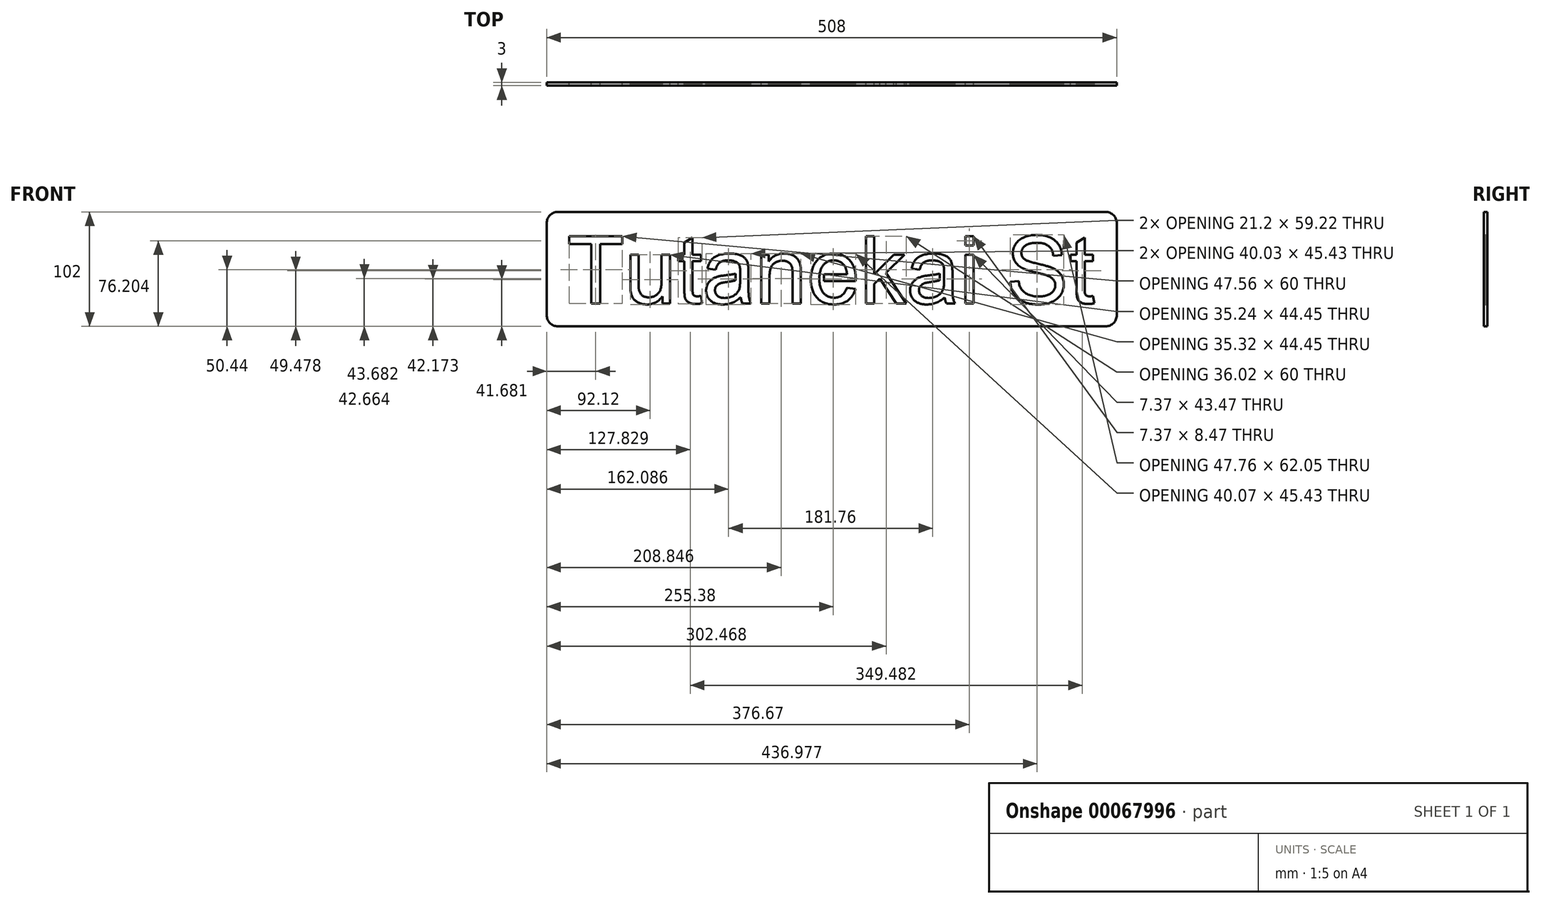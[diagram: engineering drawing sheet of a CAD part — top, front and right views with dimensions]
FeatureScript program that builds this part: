
annotation { "Feature Type Name" : "Feature", "Feature Type Description" : "" }
export const myFeature = defineFeature(function(context is Context, id is Id, definition is map)
    precondition{}
    {
        {
            var Q0;
            Q0=qCreatedBy(makeId("Front.planeOp"),FACE);
            var sketch = newSketch(context, id + "F0", { "sketchPlane" : qUnion([Q0])});
            skLineSegment(sketch, "E0", {"start": v(-254, -41) * mm, "end": v(-254, 41) * mm});
            skArc(sketch, "E1", {"start": v(-244, -51) * mm, "mid": v(-251.07, -48.07) * mm, "end": v(-254, -41) * mm});
            skLineSegment(sketch, "E2", {"start": v(244, -51) * mm, "end": v(-244, -51) * mm});
            skArc(sketch, "E3", {"start": v(254, -41) * mm, "mid": v(251.07, -48.07) * mm, "end": v(244, -51) * mm});
            skLineSegment(sketch, "E4", {"start": v(254, 41) * mm, "end": v(254, -41) * mm});
            skArc(sketch, "E5", {"start": v(244, 51) * mm, "mid": v(251.07, 48.07) * mm, "end": v(254, 41) * mm});
            skLineSegment(sketch, "E6", {"start": v(-244, 51) * mm, "end": v(244, 51) * mm});
            skArc(sketch, "E7", {"start": v(-254, 41) * mm, "mid": v(-251.07, 48.07) * mm, "end": v(-244, 51) * mm});
            skLineSegment(sketch, "E8", {"start": v(89.64, 7.79) * mm, "end": v(89, 7.78) * mm});
            skLineSegment(sketch, "E9", {"start": v(89, 7.78) * mm, "end": v(88.38, 7.76) * mm});
            skLineSegment(sketch, "E10", {"start": v(88.38, 7.76) * mm, "end": v(87.79, 7.73) * mm});
            skLineSegment(sketch, "E11", {"start": v(87.79, 7.73) * mm, "end": v(87.21, 7.68) * mm});
            skLineSegment(sketch, "E12", {"start": v(87.21, 7.68) * mm, "end": v(86.66, 7.61) * mm});
            skLineSegment(sketch, "E13", {"start": v(86.66, 7.61) * mm, "end": v(86.13, 7.53) * mm});
            skLineSegment(sketch, "E14", {"start": v(86.13, 7.53) * mm, "end": v(85.61, 7.44) * mm});
            skLineSegment(sketch, "E15", {"start": v(85.61, 7.44) * mm, "end": v(85.12, 7.33) * mm});
            skLineSegment(sketch, "E16", {"start": v(85.12, 7.33) * mm, "end": v(84.65, 7.21) * mm});
            skLineSegment(sketch, "E17", {"start": v(84.65, 7.21) * mm, "end": v(84.2, 7.08) * mm});
            skLineSegment(sketch, "E18", {"start": v(84.2, 7.08) * mm, "end": v(83.78, 6.93) * mm});
            skLineSegment(sketch, "E19", {"start": v(83.78, 6.93) * mm, "end": v(83.38, 6.76) * mm});
            skLineSegment(sketch, "E20", {"start": v(83.38, 6.76) * mm, "end": v(83, 6.59) * mm});
            skLineSegment(sketch, "E21", {"start": v(83, 6.59) * mm, "end": v(82.63, 6.4) * mm});
            skLineSegment(sketch, "E22", {"start": v(82.63, 6.4) * mm, "end": v(82.29, 6.19) * mm});
            skLineSegment(sketch, "E23", {"start": v(82.29, 6.19) * mm, "end": v(81.97, 5.97) * mm});
            skLineSegment(sketch, "E24", {"start": v(81.97, 5.97) * mm, "end": v(81.66, 5.73) * mm});
            skLineSegment(sketch, "E25", {"start": v(81.66, 5.73) * mm, "end": v(81.37, 5.47) * mm});
            skLineSegment(sketch, "E26", {"start": v(81.37, 5.47) * mm, "end": v(81.08, 5.19) * mm});
            skLineSegment(sketch, "E27", {"start": v(81.08, 5.19) * mm, "end": v(80.8, 4.88) * mm});
            skLineSegment(sketch, "E28", {"start": v(80.8, 4.88) * mm, "end": v(80.55, 4.56) * mm});
            skLineSegment(sketch, "E29", {"start": v(80.55, 4.56) * mm, "end": v(80.3, 4.2) * mm});
            skLineSegment(sketch, "E30", {"start": v(80.3, 4.2) * mm, "end": v(80.05, 3.84) * mm});
            skLineSegment(sketch, "E31", {"start": v(80.05, 3.84) * mm, "end": v(79.81, 3.45) * mm});
            skLineSegment(sketch, "E32", {"start": v(79.81, 3.45) * mm, "end": v(79.59, 3.03) * mm});
            skLineSegment(sketch, "E33", {"start": v(79.59, 3.03) * mm, "end": v(79.38, 2.6) * mm});
            skLineSegment(sketch, "E34", {"start": v(79.38, 2.6) * mm, "end": v(79.17, 2.14) * mm});
            skLineSegment(sketch, "E35", {"start": v(79.17, 2.14) * mm, "end": v(78.98, 1.66) * mm});
            skLineSegment(sketch, "E36", {"start": v(78.98, 1.66) * mm, "end": v(78.8, 1.16) * mm});
            skLineSegment(sketch, "E37", {"start": v(78.8, 1.16) * mm, "end": v(78.62, 0.63) * mm});
            skLineSegment(sketch, "E38", {"start": v(78.62, 0.63) * mm, "end": v(78.46, 0.09) * mm});
            skLineSegment(sketch, "E39", {"start": v(78.46, 0.09) * mm, "end": v(78.3, -0.48) * mm});
            skLineSegment(sketch, "E40", {"start": v(78.3, -0.48) * mm, "end": v(71.1, 0.5) * mm});
            skLineSegment(sketch, "E41", {"start": v(71.1, 0.5) * mm, "end": v(71.37, 1.63) * mm});
            skLineSegment(sketch, "E42", {"start": v(71.37, 1.63) * mm, "end": v(71.67, 2.7) * mm});
            skLineSegment(sketch, "E43", {"start": v(71.67, 2.7) * mm, "end": v(72.02, 3.72) * mm});
            skLineSegment(sketch, "E44", {"start": v(72.02, 3.72) * mm, "end": v(72.4, 4.68) * mm});
            skLineSegment(sketch, "E45", {"start": v(72.4, 4.68) * mm, "end": v(72.82, 5.59) * mm});
            skLineSegment(sketch, "E46", {"start": v(72.82, 5.59) * mm, "end": v(73.29, 6.44) * mm});
            skLineSegment(sketch, "E47", {"start": v(73.29, 6.44) * mm, "end": v(73.8, 7.23) * mm});
            skLineSegment(sketch, "E48", {"start": v(73.8, 7.23) * mm, "end": v(74.33, 7.97) * mm});
            skLineSegment(sketch, "E49", {"start": v(74.33, 7.97) * mm, "end": v(74.93, 8.66) * mm});
            skLineSegment(sketch, "E50", {"start": v(74.93, 8.66) * mm, "end": v(75.58, 9.31) * mm});
            skLineSegment(sketch, "E51", {"start": v(75.58, 9.31) * mm, "end": v(76.3, 9.92) * mm});
            skLineSegment(sketch, "E52", {"start": v(76.3, 9.92) * mm, "end": v(77.09, 10.5) * mm});
            skLineSegment(sketch, "E53", {"start": v(77.09, 10.5) * mm, "end": v(77.93, 11.02) * mm});
            skLineSegment(sketch, "E54", {"start": v(77.93, 11.02) * mm, "end": v(78.84, 11.5) * mm});
            skLineSegment(sketch, "E55", {"start": v(78.84, 11.5) * mm, "end": v(79.8, 11.95) * mm});
            skLineSegment(sketch, "E56", {"start": v(79.8, 11.95) * mm, "end": v(80.84, 12.35) * mm});
            skLineSegment(sketch, "E57", {"start": v(80.84, 12.35) * mm, "end": v(81.93, 12.71) * mm});
            skLineSegment(sketch, "E58", {"start": v(81.93, 12.71) * mm, "end": v(83.05, 13.02) * mm});
            skLineSegment(sketch, "E59", {"start": v(83.05, 13.02) * mm, "end": v(84.22, 13.29) * mm});
            skLineSegment(sketch, "E60", {"start": v(84.22, 13.29) * mm, "end": v(85.44, 13.5) * mm});
            skLineSegment(sketch, "E61", {"start": v(85.44, 13.5) * mm, "end": v(86.69, 13.67) * mm});
            skLineSegment(sketch, "E62", {"start": v(86.69, 13.67) * mm, "end": v(87.99, 13.8) * mm});
            skLineSegment(sketch, "E63", {"start": v(87.99, 13.8) * mm, "end": v(89.32, 13.86) * mm});
            skLineSegment(sketch, "E64", {"start": v(89.32, 13.86) * mm, "end": v(90.7, 13.89) * mm});
            skLineSegment(sketch, "E65", {"start": v(90.7, 13.89) * mm, "end": v(92.06, 13.87) * mm});
            skLineSegment(sketch, "E66", {"start": v(92.06, 13.87) * mm, "end": v(93.36, 13.8) * mm});
            skLineSegment(sketch, "E67", {"start": v(93.36, 13.8) * mm, "end": v(94.59, 13.7) * mm});
            skLineSegment(sketch, "E68", {"start": v(94.59, 13.7) * mm, "end": v(95.75, 13.56) * mm});
            skLineSegment(sketch, "E69", {"start": v(95.75, 13.56) * mm, "end": v(96.85, 13.38) * mm});
            skLineSegment(sketch, "E70", {"start": v(96.85, 13.38) * mm, "end": v(97.88, 13.15) * mm});
            skLineSegment(sketch, "E71", {"start": v(97.88, 13.15) * mm, "end": v(98.85, 12.88) * mm});
            skLineSegment(sketch, "E72", {"start": v(98.85, 12.88) * mm, "end": v(99.75, 12.58) * mm});
            skLineSegment(sketch, "E73", {"start": v(99.75, 12.58) * mm, "end": v(100.6, 12.24) * mm});
            skLineSegment(sketch, "E74", {"start": v(100.6, 12.24) * mm, "end": v(101.37, 11.88) * mm});
            skLineSegment(sketch, "E75", {"start": v(101.37, 11.88) * mm, "end": v(102.1, 11.5) * mm});
            skLineSegment(sketch, "E76", {"start": v(102.1, 11.5) * mm, "end": v(102.77, 11.1) * mm});
            skLineSegment(sketch, "E77", {"start": v(102.77, 11.1) * mm, "end": v(103.38, 10.68) * mm});
            skLineSegment(sketch, "E78", {"start": v(103.38, 10.68) * mm, "end": v(103.93, 10.23) * mm});
            skLineSegment(sketch, "E79", {"start": v(103.93, 10.23) * mm, "end": v(104.43, 9.77) * mm});
            skLineSegment(sketch, "E80", {"start": v(104.43, 9.77) * mm, "end": v(104.87, 9.28) * mm});
            skLineSegment(sketch, "E81", {"start": v(104.87, 9.28) * mm, "end": v(105.26, 8.77) * mm});
            skLineSegment(sketch, "E82", {"start": v(105.26, 8.77) * mm, "end": v(105.62, 8.23) * mm});
            skLineSegment(sketch, "E83", {"start": v(105.62, 8.23) * mm, "end": v(105.96, 7.65) * mm});
            skLineSegment(sketch, "E84", {"start": v(105.96, 7.65) * mm, "end": v(106.26, 7.04) * mm});
            skLineSegment(sketch, "E85", {"start": v(106.26, 7.04) * mm, "end": v(106.53, 6.4) * mm});
            skLineSegment(sketch, "E86", {"start": v(106.53, 6.4) * mm, "end": v(106.77, 5.72) * mm});
            skLineSegment(sketch, "E87", {"start": v(106.77, 5.72) * mm, "end": v(106.98, 5.01) * mm});
            skLineSegment(sketch, "E88", {"start": v(106.98, 5.01) * mm, "end": v(107.16, 4.27) * mm});
            skLineSegment(sketch, "E89", {"start": v(107.16, 4.27) * mm, "end": v(107.24, 3.75) * mm});
            skLineSegment(sketch, "E90", {"start": v(107.24, 3.75) * mm, "end": v(107.32, 3.14) * mm});
            skLineSegment(sketch, "E91", {"start": v(107.32, 3.14) * mm, "end": v(107.38, 2.43) * mm});
            skLineSegment(sketch, "E92", {"start": v(107.38, 2.43) * mm, "end": v(107.43, 1.63) * mm});
            skLineSegment(sketch, "E93", {"start": v(107.43, 1.63) * mm, "end": v(107.47, 0.73) * mm});
            skLineSegment(sketch, "E94", {"start": v(107.47, 0.73) * mm, "end": v(107.5, -0.26) * mm});
            skLineSegment(sketch, "E95", {"start": v(107.5, -0.26) * mm, "end": v(107.52, -1.34) * mm});
            skLineSegment(sketch, "E96", {"start": v(107.52, -1.34) * mm, "end": v(107.53, -2.52) * mm});
            skLineSegment(sketch, "E97", {"start": v(107.53, -2.52) * mm, "end": v(107.53, -12.35) * mm});
            skLineSegment(sketch, "E98", {"start": v(107.53, -12.35) * mm, "end": v(107.53, -13.6) * mm});
            skLineSegment(sketch, "E99", {"start": v(107.53, -13.6) * mm, "end": v(107.53, -14.8) * mm});
            skLineSegment(sketch, "E100", {"start": v(107.53, -14.8) * mm, "end": v(107.54, -15.93) * mm});
            skLineSegment(sketch, "E101", {"start": v(107.54, -15.93) * mm, "end": v(107.56, -17.01) * mm});
            skLineSegment(sketch, "E102", {"start": v(107.56, -17.01) * mm, "end": v(107.57, -18.03) * mm});
            skLineSegment(sketch, "E103", {"start": v(107.57, -18.03) * mm, "end": v(107.6, -18.99) * mm});
            skLineSegment(sketch, "E104", {"start": v(107.6, -18.99) * mm, "end": v(107.62, -19.9) * mm});
            skLineSegment(sketch, "E105", {"start": v(107.62, -19.9) * mm, "end": v(107.64, -20.73) * mm});
            skLineSegment(sketch, "E106", {"start": v(107.64, -20.73) * mm, "end": v(107.68, -21.51) * mm});
            skLineSegment(sketch, "E107", {"start": v(107.68, -21.51) * mm, "end": v(107.71, -22.24) * mm});
            skLineSegment(sketch, "E108", {"start": v(107.71, -22.24) * mm, "end": v(107.75, -22.9) * mm});
            skLineSegment(sketch, "E109", {"start": v(107.75, -22.9) * mm, "end": v(107.8, -23.5) * mm});
            skLineSegment(sketch, "E110", {"start": v(107.8, -23.5) * mm, "end": v(107.84, -24.06) * mm});
            skLineSegment(sketch, "E111", {"start": v(107.84, -24.06) * mm, "end": v(107.89, -24.54) * mm});
            skLineSegment(sketch, "E112", {"start": v(107.89, -24.54) * mm, "end": v(107.94, -24.97) * mm});
            skLineSegment(sketch, "E113", {"start": v(107.94, -24.97) * mm, "end": v(108, -25.34) * mm});
            skLineSegment(sketch, "E114", {"start": v(108, -25.34) * mm, "end": v(108.13, -26.02) * mm});
            skLineSegment(sketch, "E115", {"start": v(108.13, -26.02) * mm, "end": v(108.29, -26.69) * mm});
            skLineSegment(sketch, "E116", {"start": v(108.29, -26.69) * mm, "end": v(108.48, -27.35) * mm});
            skLineSegment(sketch, "E117", {"start": v(108.48, -27.35) * mm, "end": v(108.7, -28) * mm});
            skLineSegment(sketch, "E118", {"start": v(108.7, -28) * mm, "end": v(108.95, -28.66) * mm});
            skLineSegment(sketch, "E119", {"start": v(108.95, -28.66) * mm, "end": v(109.22, -29.3) * mm});
            skLineSegment(sketch, "E120", {"start": v(109.22, -29.3) * mm, "end": v(109.53, -29.93) * mm});
            skLineSegment(sketch, "E121", {"start": v(109.53, -29.93) * mm, "end": v(109.86, -30.56) * mm});
            skLineSegment(sketch, "E122", {"start": v(109.86, -30.56) * mm, "end": v(102.16, -30.56) * mm});
            skLineSegment(sketch, "E123", {"start": v(102.16, -30.56) * mm, "end": v(101.9, -29.97) * mm});
            skLineSegment(sketch, "E124", {"start": v(101.9, -29.97) * mm, "end": v(101.64, -29.37) * mm});
            skLineSegment(sketch, "E125", {"start": v(101.64, -29.37) * mm, "end": v(101.42, -28.73) * mm});
            skLineSegment(sketch, "E126", {"start": v(101.42, -28.73) * mm, "end": v(101.22, -28.07) * mm});
            skLineSegment(sketch, "E127", {"start": v(101.22, -28.07) * mm, "end": v(101.05, -27.4) * mm});
            skLineSegment(sketch, "E128", {"start": v(101.05, -27.4) * mm, "end": v(100.9, -26.68) * mm});
            skLineSegment(sketch, "E129", {"start": v(100.9, -26.68) * mm, "end": v(100.79, -25.95) * mm});
            skLineSegment(sketch, "E130", {"start": v(100.79, -25.95) * mm, "end": v(100.7, -25.2) * mm});
            skLineSegment(sketch, "E131", {"start": v(100.7, -25.2) * mm, "end": v(99.67, -26.04) * mm});
            skLineSegment(sketch, "E132", {"start": v(99.67, -26.04) * mm, "end": v(98.66, -26.8) * mm});
            skLineSegment(sketch, "E133", {"start": v(98.66, -26.8) * mm, "end": v(97.67, -27.52) * mm});
            skLineSegment(sketch, "E134", {"start": v(97.67, -27.52) * mm, "end": v(96.68, -28.17) * mm});
            skLineSegment(sketch, "E135", {"start": v(96.68, -28.17) * mm, "end": v(95.7, -28.75) * mm});
            skLineSegment(sketch, "E136", {"start": v(95.7, -28.75) * mm, "end": v(94.73, -29.27) * mm});
            skLineSegment(sketch, "E137", {"start": v(94.73, -29.27) * mm, "end": v(93.76, -29.72) * mm});
            skLineSegment(sketch, "E138", {"start": v(93.76, -29.72) * mm, "end": v(92.81, -30.1) * mm});
            skLineSegment(sketch, "E139", {"start": v(92.81, -30.1) * mm, "end": v(91.86, -30.45) * mm});
            skLineSegment(sketch, "E140", {"start": v(91.86, -30.45) * mm, "end": v(90.89, -30.74) * mm});
            skLineSegment(sketch, "E141", {"start": v(90.89, -30.74) * mm, "end": v(89.9, -30.98) * mm});
            skLineSegment(sketch, "E142", {"start": v(89.9, -30.98) * mm, "end": v(88.89, -31.18) * mm});
            skLineSegment(sketch, "E143", {"start": v(88.89, -31.18) * mm, "end": v(87.86, -31.34) * mm});
            skLineSegment(sketch, "E144", {"start": v(87.86, -31.34) * mm, "end": v(86.82, -31.45) * mm});
            skLineSegment(sketch, "E145", {"start": v(86.82, -31.45) * mm, "end": v(85.76, -31.52) * mm});
            skLineSegment(sketch, "E146", {"start": v(85.76, -31.52) * mm, "end": v(84.69, -31.54) * mm});
            skLineSegment(sketch, "E147", {"start": v(84.69, -31.54) * mm, "end": v(83.8, -31.53) * mm});
            skLineSegment(sketch, "E148", {"start": v(83.8, -31.53) * mm, "end": v(82.95, -31.49) * mm});
            skLineSegment(sketch, "E149", {"start": v(82.95, -31.49) * mm, "end": v(82.12, -31.42) * mm});
            skLineSegment(sketch, "E150", {"start": v(82.12, -31.42) * mm, "end": v(81.31, -31.32) * mm});
            skLineSegment(sketch, "E151", {"start": v(81.31, -31.32) * mm, "end": v(80.54, -31.2) * mm});
            skLineSegment(sketch, "E152", {"start": v(80.54, -31.2) * mm, "end": v(79.78, -31.05) * mm});
            skLineSegment(sketch, "E153", {"start": v(79.78, -31.05) * mm, "end": v(79.06, -30.87) * mm});
            skLineSegment(sketch, "E154", {"start": v(79.06, -30.87) * mm, "end": v(78.36, -30.67) * mm});
            skLineSegment(sketch, "E155", {"start": v(78.36, -30.67) * mm, "end": v(77.68, -30.44) * mm});
            skLineSegment(sketch, "E156", {"start": v(77.68, -30.44) * mm, "end": v(77.03, -30.18) * mm});
            skLineSegment(sketch, "E157", {"start": v(77.03, -30.18) * mm, "end": v(76.4, -29.89) * mm});
            skLineSegment(sketch, "E158", {"start": v(76.4, -29.89) * mm, "end": v(75.81, -29.57) * mm});
            skLineSegment(sketch, "E159", {"start": v(75.81, -29.57) * mm, "end": v(75.24, -29.23) * mm});
            skLineSegment(sketch, "E160", {"start": v(75.24, -29.23) * mm, "end": v(74.7, -28.86) * mm});
            skLineSegment(sketch, "E161", {"start": v(74.7, -28.86) * mm, "end": v(74.17, -28.47) * mm});
            skLineSegment(sketch, "E162", {"start": v(74.17, -28.47) * mm, "end": v(73.68, -28.04) * mm});
            skLineSegment(sketch, "E163", {"start": v(73.68, -28.04) * mm, "end": v(73.21, -27.6) * mm});
            skLineSegment(sketch, "E164", {"start": v(73.21, -27.6) * mm, "end": v(72.78, -27.14) * mm});
            skLineSegment(sketch, "E165", {"start": v(72.78, -27.14) * mm, "end": v(72.37, -26.66) * mm});
            skLineSegment(sketch, "E166", {"start": v(72.37, -26.66) * mm, "end": v(72, -26.17) * mm});
            skLineSegment(sketch, "E167", {"start": v(72, -26.17) * mm, "end": v(71.65, -25.67) * mm});
            skLineSegment(sketch, "E168", {"start": v(71.65, -25.67) * mm, "end": v(71.33, -25.15) * mm});
            skLineSegment(sketch, "E169", {"start": v(71.33, -25.15) * mm, "end": v(71.05, -24.6) * mm});
            skLineSegment(sketch, "E170", {"start": v(71.05, -24.6) * mm, "end": v(70.8, -24.06) * mm});
            skLineSegment(sketch, "E171", {"start": v(70.8, -24.06) * mm, "end": v(70.57, -23.5) * mm});
            skLineSegment(sketch, "E172", {"start": v(70.57, -23.5) * mm, "end": v(70.37, -22.9) * mm});
            skLineSegment(sketch, "E173", {"start": v(70.37, -22.9) * mm, "end": v(70.2, -22.31) * mm});
            skLineSegment(sketch, "E174", {"start": v(70.2, -22.31) * mm, "end": v(70.07, -21.7) * mm});
            skLineSegment(sketch, "E175", {"start": v(70.07, -21.7) * mm, "end": v(69.97, -21.07) * mm});
            skLineSegment(sketch, "E176", {"start": v(69.97, -21.07) * mm, "end": v(69.9, -20.43) * mm});
            skLineSegment(sketch, "E177", {"start": v(69.9, -20.43) * mm, "end": v(69.85, -19.77) * mm});
            skLineSegment(sketch, "E178", {"start": v(69.85, -19.77) * mm, "end": v(69.83, -19.1) * mm});
            skLineSegment(sketch, "E179", {"start": v(69.83, -19.1) * mm, "end": v(69.85, -18.31) * mm});
            skLineSegment(sketch, "E180", {"start": v(69.85, -18.31) * mm, "end": v(69.92, -17.54) * mm});
            skLineSegment(sketch, "E181", {"start": v(69.92, -17.54) * mm, "end": v(70.04, -16.78) * mm});
            skLineSegment(sketch, "E182", {"start": v(70.04, -16.78) * mm, "end": v(70.2, -16.05) * mm});
            skLineSegment(sketch, "E183", {"start": v(70.2, -16.05) * mm, "end": v(70.4, -15.33) * mm});
            skLineSegment(sketch, "E184", {"start": v(70.4, -15.33) * mm, "end": v(70.65, -14.62) * mm});
            skLineSegment(sketch, "E185", {"start": v(70.65, -14.62) * mm, "end": v(70.94, -13.94) * mm});
            skLineSegment(sketch, "E186", {"start": v(70.94, -13.94) * mm, "end": v(71.28, -13.27) * mm});
            skLineSegment(sketch, "E187", {"start": v(71.28, -13.27) * mm, "end": v(71.66, -12.62) * mm});
            skLineSegment(sketch, "E188", {"start": v(71.66, -12.62) * mm, "end": v(72.07, -12.01) * mm});
            skLineSegment(sketch, "E189", {"start": v(72.07, -12.01) * mm, "end": v(72.5, -11.43) * mm});
            skLineSegment(sketch, "E190", {"start": v(72.5, -11.43) * mm, "end": v(72.96, -10.89) * mm});
            skLineSegment(sketch, "E191", {"start": v(72.96, -10.89) * mm, "end": v(73.45, -10.38) * mm});
            skLineSegment(sketch, "E192", {"start": v(73.45, -10.38) * mm, "end": v(73.97, -9.9) * mm});
            skLineSegment(sketch, "E193", {"start": v(73.97, -9.9) * mm, "end": v(74.52, -9.45) * mm});
            skLineSegment(sketch, "E194", {"start": v(74.52, -9.45) * mm, "end": v(75.1, -9.03) * mm});
            skLineSegment(sketch, "E195", {"start": v(75.1, -9.03) * mm, "end": v(75.69, -8.65) * mm});
            skLineSegment(sketch, "E196", {"start": v(75.69, -8.65) * mm, "end": v(76.3, -8.28) * mm});
            skLineSegment(sketch, "E197", {"start": v(76.3, -8.28) * mm, "end": v(76.94, -7.94) * mm});
            skLineSegment(sketch, "E198", {"start": v(76.94, -7.94) * mm, "end": v(77.6, -7.63) * mm});
            skLineSegment(sketch, "E199", {"start": v(77.6, -7.63) * mm, "end": v(78.26, -7.34) * mm});
            skLineSegment(sketch, "E200", {"start": v(78.26, -7.34) * mm, "end": v(78.96, -7.08) * mm});
            skLineSegment(sketch, "E201", {"start": v(78.96, -7.08) * mm, "end": v(79.66, -6.83) * mm});
            skLineSegment(sketch, "E202", {"start": v(79.66, -6.83) * mm, "end": v(80.4, -6.62) * mm});
            skLineSegment(sketch, "E203", {"start": v(80.4, -6.62) * mm, "end": v(80.97, -6.47) * mm});
            skLineSegment(sketch, "E204", {"start": v(80.97, -6.47) * mm, "end": v(81.61, -6.33) * mm});
            skLineSegment(sketch, "E205", {"start": v(81.61, -6.33) * mm, "end": v(82.33, -6.2) * mm});
            skLineSegment(sketch, "E206", {"start": v(82.33, -6.2) * mm, "end": v(83.11, -6.05) * mm});
            skLineSegment(sketch, "E207", {"start": v(83.11, -6.05) * mm, "end": v(83.97, -5.92) * mm});
            skLineSegment(sketch, "E208", {"start": v(83.97, -5.92) * mm, "end": v(84.89, -5.78) * mm});
            skLineSegment(sketch, "E209", {"start": v(84.89, -5.78) * mm, "end": v(85.88, -5.65) * mm});
            skLineSegment(sketch, "E210", {"start": v(85.88, -5.65) * mm, "end": v(86.94, -5.51) * mm});
            skLineSegment(sketch, "E211", {"start": v(86.94, -5.51) * mm, "end": v(88.04, -5.38) * mm});
            skLineSegment(sketch, "E212", {"start": v(88.04, -5.38) * mm, "end": v(89.1, -5.24) * mm});
            skLineSegment(sketch, "E213", {"start": v(89.1, -5.24) * mm, "end": v(90.12, -5.1) * mm});
            skLineSegment(sketch, "E214", {"start": v(90.12, -5.1) * mm, "end": v(91.1, -4.95) * mm});
            skLineSegment(sketch, "E215", {"start": v(91.1, -4.95) * mm, "end": v(92.06, -4.8) * mm});
            skLineSegment(sketch, "E216", {"start": v(92.06, -4.8) * mm, "end": v(92.97, -4.66) * mm});
            skLineSegment(sketch, "E217", {"start": v(92.97, -4.66) * mm, "end": v(93.85, -4.5) * mm});
            skLineSegment(sketch, "E218", {"start": v(93.85, -4.5) * mm, "end": v(94.69, -4.35) * mm});
            skLineSegment(sketch, "E219", {"start": v(94.69, -4.35) * mm, "end": v(95.49, -4.19) * mm});
            skLineSegment(sketch, "E220", {"start": v(95.49, -4.19) * mm, "end": v(96.09, -4.06) * mm});
            skLineSegment(sketch, "E221", {"start": v(96.08, -10.01) * mm, "end": v(96.09, -4.06) * mm});
            skLineSegment(sketch, "E222", {"start": v(96.08, -10.01) * mm, "end": v(95.8, -10.08) * mm});
            skLineSegment(sketch, "E223", {"start": v(95.8, -10.08) * mm, "end": v(95.06, -10.26) * mm});
            skLineSegment(sketch, "E224", {"start": v(95.06, -10.26) * mm, "end": v(94.3, -10.43) * mm});
            skLineSegment(sketch, "E225", {"start": v(94.3, -10.43) * mm, "end": v(93.5, -10.6) * mm});
            skLineSegment(sketch, "E226", {"start": v(93.5, -10.6) * mm, "end": v(92.67, -10.76) * mm});
            skLineSegment(sketch, "E227", {"start": v(92.67, -10.76) * mm, "end": v(91.8, -10.92) * mm});
            skLineSegment(sketch, "E228", {"start": v(91.8, -10.92) * mm, "end": v(90.91, -11.08) * mm});
            skLineSegment(sketch, "E229", {"start": v(90.91, -11.08) * mm, "end": v(89.99, -11.23) * mm});
            skLineSegment(sketch, "E230", {"start": v(89.99, -11.23) * mm, "end": v(89.03, -11.38) * mm});
            skLineSegment(sketch, "E231", {"start": v(89.03, -11.38) * mm, "end": v(88.04, -11.53) * mm});
            skLineSegment(sketch, "E232", {"start": v(88.04, -11.53) * mm, "end": v(86.95, -11.7) * mm});
            skLineSegment(sketch, "E233", {"start": v(86.95, -11.7) * mm, "end": v(85.94, -11.87) * mm});
            skLineSegment(sketch, "E234", {"start": v(85.94, -11.87) * mm, "end": v(85.01, -12.04) * mm});
            skLineSegment(sketch, "E235", {"start": v(85.01, -12.04) * mm, "end": v(84.17, -12.22) * mm});
            skLineSegment(sketch, "E236", {"start": v(84.17, -12.22) * mm, "end": v(83.4, -12.41) * mm});
            skLineSegment(sketch, "E237", {"start": v(83.4, -12.41) * mm, "end": v(82.73, -12.6) * mm});
            skLineSegment(sketch, "E238", {"start": v(82.73, -12.6) * mm, "end": v(82.13, -12.8) * mm});
            skLineSegment(sketch, "E239", {"start": v(82.13, -12.8) * mm, "end": v(81.62, -13) * mm});
            skLineSegment(sketch, "E240", {"start": v(81.62, -13) * mm, "end": v(81.16, -13.22) * mm});
            skLineSegment(sketch, "E241", {"start": v(81.16, -13.22) * mm, "end": v(80.73, -13.46) * mm});
            skLineSegment(sketch, "E242", {"start": v(80.73, -13.46) * mm, "end": v(80.33, -13.72) * mm});
            skLineSegment(sketch, "E243", {"start": v(80.33, -13.72) * mm, "end": v(79.95, -14) * mm});
            skLineSegment(sketch, "E244", {"start": v(79.95, -14) * mm, "end": v(79.6, -14.32) * mm});
            skLineSegment(sketch, "E245", {"start": v(79.6, -14.32) * mm, "end": v(79.28, -14.66) * mm});
            skLineSegment(sketch, "E246", {"start": v(79.28, -14.66) * mm, "end": v(78.98, -15.01) * mm});
            skLineSegment(sketch, "E247", {"start": v(78.98, -15.01) * mm, "end": v(78.71, -15.4) * mm});
            skLineSegment(sketch, "E248", {"start": v(78.71, -15.4) * mm, "end": v(78.47, -15.8) * mm});
            skLineSegment(sketch, "E249", {"start": v(78.47, -15.8) * mm, "end": v(78.27, -16.2) * mm});
            skLineSegment(sketch, "E250", {"start": v(78.27, -16.2) * mm, "end": v(78.09, -16.63) * mm});
            skLineSegment(sketch, "E251", {"start": v(78.09, -16.63) * mm, "end": v(77.95, -17.06) * mm});
            skLineSegment(sketch, "E252", {"start": v(77.95, -17.06) * mm, "end": v(77.83, -17.5) * mm});
            skLineSegment(sketch, "E253", {"start": v(77.83, -17.5) * mm, "end": v(77.75, -17.96) * mm});
            skLineSegment(sketch, "E254", {"start": v(77.75, -17.96) * mm, "end": v(77.7, -18.42) * mm});
            skLineSegment(sketch, "E255", {"start": v(77.7, -18.42) * mm, "end": v(77.7, -18.9) * mm});
            skLineSegment(sketch, "E256", {"start": v(77.7, -18.9) * mm, "end": v(77.72, -19.62) * mm});
            skLineSegment(sketch, "E257", {"start": v(77.72, -19.62) * mm, "end": v(77.83, -20.3) * mm});
            skLineSegment(sketch, "E258", {"start": v(77.83, -20.3) * mm, "end": v(78, -20.97) * mm});
            skLineSegment(sketch, "E259", {"start": v(78, -20.97) * mm, "end": v(78.25, -21.6) * mm});
            skLineSegment(sketch, "E260", {"start": v(78.25, -21.6) * mm, "end": v(78.56, -22.2) * mm});
            skLineSegment(sketch, "E261", {"start": v(78.56, -22.2) * mm, "end": v(78.94, -22.76) * mm});
            skLineSegment(sketch, "E262", {"start": v(78.94, -22.76) * mm, "end": v(79.4, -23.3) * mm});
            skLineSegment(sketch, "E263", {"start": v(79.4, -23.3) * mm, "end": v(79.92, -23.8) * mm});
            skLineSegment(sketch, "E264", {"start": v(79.92, -23.8) * mm, "end": v(80.51, -24.27) * mm});
            skLineSegment(sketch, "E265", {"start": v(80.51, -24.27) * mm, "end": v(81.17, -24.67) * mm});
            skLineSegment(sketch, "E266", {"start": v(81.17, -24.67) * mm, "end": v(81.88, -25) * mm});
            skLineSegment(sketch, "E267", {"start": v(81.88, -25) * mm, "end": v(82.67, -25.28) * mm});
            skLineSegment(sketch, "E268", {"start": v(82.67, -25.28) * mm, "end": v(83.52, -25.5) * mm});
            skLineSegment(sketch, "E269", {"start": v(83.52, -25.5) * mm, "end": v(84.43, -25.65) * mm});
            skLineSegment(sketch, "E270", {"start": v(84.43, -25.65) * mm, "end": v(85.4, -25.74) * mm});
            skLineSegment(sketch, "E271", {"start": v(85.4, -25.74) * mm, "end": v(86.45, -25.77) * mm});
            skLineSegment(sketch, "E272", {"start": v(86.45, -25.77) * mm, "end": v(87.5, -25.74) * mm});
            skLineSegment(sketch, "E273", {"start": v(87.5, -25.74) * mm, "end": v(88.52, -25.66) * mm});
            skLineSegment(sketch, "E274", {"start": v(88.52, -25.66) * mm, "end": v(89.5, -25.5) * mm});
            skLineSegment(sketch, "E275", {"start": v(89.5, -25.5) * mm, "end": v(90.47, -25.3) * mm});
            skLineSegment(sketch, "E276", {"start": v(90.47, -25.3) * mm, "end": v(91.4, -25.04) * mm});
            skLineSegment(sketch, "E277", {"start": v(91.4, -25.04) * mm, "end": v(92.3, -24.72) * mm});
            skLineSegment(sketch, "E278", {"start": v(92.3, -24.72) * mm, "end": v(93.18, -24.35) * mm});
            skLineSegment(sketch, "E279", {"start": v(93.18, -24.35) * mm, "end": v(94.02, -23.9) * mm});
            skLineSegment(sketch, "E280", {"start": v(94.02, -23.9) * mm, "end": v(94.82, -23.42) * mm});
            skLineSegment(sketch, "E281", {"start": v(94.82, -23.42) * mm, "end": v(95.57, -22.9) * mm});
            skLineSegment(sketch, "E282", {"start": v(95.57, -22.9) * mm, "end": v(96.26, -22.32) * mm});
            skLineSegment(sketch, "E283", {"start": v(96.26, -22.32) * mm, "end": v(96.9, -21.7) * mm});
            skLineSegment(sketch, "E284", {"start": v(96.9, -21.7) * mm, "end": v(97.48, -21.05) * mm});
            skLineSegment(sketch, "E285", {"start": v(97.48, -21.05) * mm, "end": v(98, -20.34) * mm});
            skLineSegment(sketch, "E286", {"start": v(98, -20.34) * mm, "end": v(98.47, -19.6) * mm});
            skLineSegment(sketch, "E287", {"start": v(98.47, -19.6) * mm, "end": v(98.9, -18.81) * mm});
            skLineSegment(sketch, "E288", {"start": v(98.9, -18.81) * mm, "end": v(99.17, -18.15) * mm});
            skLineSegment(sketch, "E289", {"start": v(99.17, -18.15) * mm, "end": v(99.4, -17.42) * mm});
            skLineSegment(sketch, "E290", {"start": v(99.4, -17.42) * mm, "end": v(99.61, -16.6) * mm});
            skLineSegment(sketch, "E291", {"start": v(99.61, -16.6) * mm, "end": v(99.78, -15.72) * mm});
            skLineSegment(sketch, "E292", {"start": v(99.78, -15.72) * mm, "end": v(99.91, -14.77) * mm});
            skLineSegment(sketch, "E293", {"start": v(99.91, -14.77) * mm, "end": v(100, -13.73) * mm});
            skLineSegment(sketch, "E294", {"start": v(100, -13.73) * mm, "end": v(100.06, -12.63) * mm});
            skLineSegment(sketch, "E295", {"start": v(100.06, -12.63) * mm, "end": v(100.08, -11.45) * mm});
            skLineSegment(sketch, "E296", {"start": v(100.08, -11.45) * mm, "end": v(100.09, -2.61) * mm});
            skLineSegment(sketch, "E297", {"start": v(100.09, -2.61) * mm, "end": v(100.1, -2.29) * mm});
            skLineSegment(sketch, "E298", {"start": v(100.1, -2.29) * mm, "end": v(100.1, -2) * mm});
            skLineSegment(sketch, "E299", {"start": v(100.1, -2) * mm, "end": v(100.1, -1.74) * mm});
            skLineSegment(sketch, "E300", {"start": v(100.1, -1.74) * mm, "end": v(100.11, -1.51) * mm});
            skLineSegment(sketch, "E301", {"start": v(100.11, -1.51) * mm, "end": v(100.12, -1.32) * mm});
            skLineSegment(sketch, "E302", {"start": v(100.12, -1.32) * mm, "end": v(100.12, -1.17) * mm});
            skLineSegment(sketch, "E303", {"start": v(100.12, -1.17) * mm, "end": v(100.12, -1.05) * mm});
            skLineSegment(sketch, "E304", {"start": v(100.12, -1.05) * mm, "end": v(100.11, -0.5) * mm});
            skLineSegment(sketch, "E305", {"start": v(100.11, -0.5) * mm, "end": v(100.09, 0.03) * mm});
            skLineSegment(sketch, "E306", {"start": v(100.09, 0.03) * mm, "end": v(100.05, 0.54) * mm});
            skLineSegment(sketch, "E307", {"start": v(100.05, 0.54) * mm, "end": v(99.99, 1.03) * mm});
            skLineSegment(sketch, "E308", {"start": v(99.99, 1.03) * mm, "end": v(99.91, 1.5) * mm});
            skLineSegment(sketch, "E309", {"start": v(99.91, 1.5) * mm, "end": v(99.82, 1.95) * mm});
            skLineSegment(sketch, "E310", {"start": v(99.82, 1.95) * mm, "end": v(99.72, 2.38) * mm});
            skLineSegment(sketch, "E311", {"start": v(99.72, 2.38) * mm, "end": v(99.6, 2.79) * mm});
            skLineSegment(sketch, "E312", {"start": v(99.6, 2.79) * mm, "end": v(99.46, 3.17) * mm});
            skLineSegment(sketch, "E313", {"start": v(99.46, 3.17) * mm, "end": v(99.3, 3.54) * mm});
            skLineSegment(sketch, "E314", {"start": v(99.3, 3.54) * mm, "end": v(99.13, 3.88) * mm});
            skLineSegment(sketch, "E315", {"start": v(99.13, 3.88) * mm, "end": v(98.94, 4.2) * mm});
            skLineSegment(sketch, "E316", {"start": v(98.94, 4.2) * mm, "end": v(98.74, 4.5) * mm});
            skLineSegment(sketch, "E317", {"start": v(98.74, 4.5) * mm, "end": v(98.52, 4.8) * mm});
            skLineSegment(sketch, "E318", {"start": v(98.52, 4.8) * mm, "end": v(98.28, 5.05) * mm});
            skLineSegment(sketch, "E319", {"start": v(98.28, 5.05) * mm, "end": v(98.03, 5.3) * mm});
            skLineSegment(sketch, "E320", {"start": v(98.03, 5.3) * mm, "end": v(97.67, 5.6) * mm});
            skLineSegment(sketch, "E321", {"start": v(97.67, 5.6) * mm, "end": v(97.28, 5.88) * mm});
            skLineSegment(sketch, "E322", {"start": v(97.28, 5.88) * mm, "end": v(96.88, 6.14) * mm});
            skLineSegment(sketch, "E323", {"start": v(96.88, 6.14) * mm, "end": v(96.45, 6.38) * mm});
            skLineSegment(sketch, "E324", {"start": v(96.45, 6.38) * mm, "end": v(96, 6.6) * mm});
            skLineSegment(sketch, "E325", {"start": v(96, 6.6) * mm, "end": v(95.53, 6.81) * mm});
            skLineSegment(sketch, "E326", {"start": v(95.53, 6.81) * mm, "end": v(95.04, 7) * mm});
            skLineSegment(sketch, "E327", {"start": v(95.04, 7) * mm, "end": v(94.52, 7.17) * mm});
            skLineSegment(sketch, "E328", {"start": v(94.52, 7.17) * mm, "end": v(93.99, 7.31) * mm});
            skLineSegment(sketch, "E329", {"start": v(93.99, 7.31) * mm, "end": v(93.43, 7.44) * mm});
            skLineSegment(sketch, "E330", {"start": v(93.43, 7.44) * mm, "end": v(92.85, 7.55) * mm});
            skLineSegment(sketch, "E331", {"start": v(92.85, 7.55) * mm, "end": v(92.25, 7.63) * mm});
            skLineSegment(sketch, "E332", {"start": v(92.25, 7.63) * mm, "end": v(91.63, 7.7) * mm});
            skLineSegment(sketch, "E333", {"start": v(91.63, 7.7) * mm, "end": v(90.99, 7.75) * mm});
            skLineSegment(sketch, "E334", {"start": v(90.99, 7.75) * mm, "end": v(90.33, 7.78) * mm});
            skLineSegment(sketch, "E335", {"start": v(90.33, 7.78) * mm, "end": v(89.64, 7.79) * mm});
            skLineSegment(sketch, "E336", {"start": v(-4.54, -23.69) * mm, "end": v(-4, -24) * mm});
            skLineSegment(sketch, "E337", {"start": v(-4, -24) * mm, "end": v(-3.46, -24.28) * mm});
            skLineSegment(sketch, "E338", {"start": v(-3.46, -24.28) * mm, "end": v(-2.9, -24.53) * mm});
            skLineSegment(sketch, "E339", {"start": v(-2.9, -24.53) * mm, "end": v(-2.32, -24.76) * mm});
            skLineSegment(sketch, "E340", {"start": v(-2.32, -24.76) * mm, "end": v(-1.73, -24.95) * mm});
            skLineSegment(sketch, "E341", {"start": v(-1.73, -24.95) * mm, "end": v(-1.13, -25.11) * mm});
            skLineSegment(sketch, "E342", {"start": v(-1.13, -25.11) * mm, "end": v(-0.51, -25.25) * mm});
            skLineSegment(sketch, "E343", {"start": v(-0.51, -25.25) * mm, "end": v(0.12, -25.35) * mm});
            skLineSegment(sketch, "E344", {"start": v(0.12, -25.35) * mm, "end": v(0.76, -25.43) * mm});
            skLineSegment(sketch, "E345", {"start": v(0.76, -25.43) * mm, "end": v(1.42, -25.47) * mm});
            skLineSegment(sketch, "E346", {"start": v(1.42, -25.47) * mm, "end": v(2.1, -25.48) * mm});
            skLineSegment(sketch, "E347", {"start": v(2.1, -25.48) * mm, "end": v(3.1, -25.45) * mm});
            skLineSegment(sketch, "E348", {"start": v(3.1, -25.45) * mm, "end": v(4.05, -25.35) * mm});
            skLineSegment(sketch, "E349", {"start": v(4.05, -25.35) * mm, "end": v(4.97, -25.19) * mm});
            skLineSegment(sketch, "E350", {"start": v(4.97, -25.19) * mm, "end": v(5.85, -24.95) * mm});
            skLineSegment(sketch, "E351", {"start": v(5.85, -24.95) * mm, "end": v(6.7, -24.65) * mm});
            skLineSegment(sketch, "E352", {"start": v(6.7, -24.65) * mm, "end": v(7.5, -24.29) * mm});
            skLineSegment(sketch, "E353", {"start": v(7.5, -24.29) * mm, "end": v(8.28, -23.86) * mm});
            skLineSegment(sketch, "E354", {"start": v(8.28, -23.86) * mm, "end": v(9.01, -23.36) * mm});
            skLineSegment(sketch, "E355", {"start": v(9.01, -23.36) * mm, "end": v(9.71, -22.78) * mm});
            skLineSegment(sketch, "E356", {"start": v(9.71, -22.78) * mm, "end": v(10.37, -22.13) * mm});
            skLineSegment(sketch, "E357", {"start": v(10.37, -22.13) * mm, "end": v(11, -21.4) * mm});
            skLineSegment(sketch, "E358", {"start": v(11, -21.4) * mm, "end": v(11.58, -20.6) * mm});
            skLineSegment(sketch, "E359", {"start": v(11.58, -20.6) * mm, "end": v(12.13, -19.7) * mm});
            skLineSegment(sketch, "E360", {"start": v(12.13, -19.7) * mm, "end": v(12.64, -18.74) * mm});
            skLineSegment(sketch, "E361", {"start": v(12.64, -18.74) * mm, "end": v(13.12, -17.69) * mm});
            skLineSegment(sketch, "E362", {"start": v(13.12, -17.69) * mm, "end": v(13.56, -16.56) * mm});
            skLineSegment(sketch, "E363", {"start": v(13.56, -16.56) * mm, "end": v(21.17, -17.5) * mm});
            skLineSegment(sketch, "E364", {"start": v(21.17, -17.5) * mm, "end": v(20.93, -18.33) * mm});
            skLineSegment(sketch, "E365", {"start": v(20.93, -18.33) * mm, "end": v(20.67, -19.13) * mm});
            skLineSegment(sketch, "E366", {"start": v(20.67, -19.13) * mm, "end": v(20.39, -19.9) * mm});
            skLineSegment(sketch, "E367", {"start": v(20.39, -19.9) * mm, "end": v(20.08, -20.65) * mm});
            skLineSegment(sketch, "E368", {"start": v(20.08, -20.65) * mm, "end": v(19.74, -21.38) * mm});
            skLineSegment(sketch, "E369", {"start": v(19.74, -21.38) * mm, "end": v(19.39, -22.09) * mm});
            skLineSegment(sketch, "E370", {"start": v(19.39, -22.09) * mm, "end": v(19, -22.77) * mm});
            skLineSegment(sketch, "E371", {"start": v(19, -22.77) * mm, "end": v(18.6, -23.43) * mm});
            skLineSegment(sketch, "E372", {"start": v(18.6, -23.43) * mm, "end": v(18.17, -24.06) * mm});
            skLineSegment(sketch, "E373", {"start": v(18.17, -24.06) * mm, "end": v(17.72, -24.68) * mm});
            skLineSegment(sketch, "E374", {"start": v(17.72, -24.68) * mm, "end": v(17.24, -25.26) * mm});
            skLineSegment(sketch, "E375", {"start": v(17.24, -25.26) * mm, "end": v(16.74, -25.83) * mm});
            skLineSegment(sketch, "E376", {"start": v(16.74, -25.83) * mm, "end": v(16.22, -26.37) * mm});
            skLineSegment(sketch, "E377", {"start": v(16.22, -26.37) * mm, "end": v(15.67, -26.9) * mm});
            skLineSegment(sketch, "E378", {"start": v(15.67, -26.9) * mm, "end": v(15.1, -27.39) * mm});
            skLineSegment(sketch, "E379", {"start": v(15.1, -27.39) * mm, "end": v(14.5, -27.86) * mm});
            skLineSegment(sketch, "E380", {"start": v(14.5, -27.86) * mm, "end": v(13.88, -28.3) * mm});
            skLineSegment(sketch, "E381", {"start": v(13.88, -28.3) * mm, "end": v(13.24, -28.72) * mm});
            skLineSegment(sketch, "E382", {"start": v(13.24, -28.72) * mm, "end": v(12.58, -29.11) * mm});
            skLineSegment(sketch, "E383", {"start": v(12.58, -29.11) * mm, "end": v(11.9, -29.47) * mm});
            skLineSegment(sketch, "E384", {"start": v(11.9, -29.47) * mm, "end": v(11.19, -29.8) * mm});
            skLineSegment(sketch, "E385", {"start": v(11.19, -29.8) * mm, "end": v(10.47, -30.1) * mm});
            skLineSegment(sketch, "E386", {"start": v(10.47, -30.1) * mm, "end": v(9.72, -30.38) * mm});
            skLineSegment(sketch, "E387", {"start": v(9.72, -30.38) * mm, "end": v(8.95, -30.62) * mm});
            skLineSegment(sketch, "E388", {"start": v(8.95, -30.62) * mm, "end": v(8.16, -30.84) * mm});
            skLineSegment(sketch, "E389", {"start": v(8.16, -30.84) * mm, "end": v(7.35, -31.02) * mm});
            skLineSegment(sketch, "E390", {"start": v(7.35, -31.02) * mm, "end": v(6.52, -31.18) * mm});
            skLineSegment(sketch, "E391", {"start": v(6.52, -31.18) * mm, "end": v(5.67, -31.31) * mm});
            skLineSegment(sketch, "E392", {"start": v(5.67, -31.31) * mm, "end": v(4.8, -31.41) * mm});
            skLineSegment(sketch, "E393", {"start": v(4.8, -31.41) * mm, "end": v(3.9, -31.48) * mm});
            skLineSegment(sketch, "E394", {"start": v(3.9, -31.48) * mm, "end": v(3, -31.53) * mm});
            skLineSegment(sketch, "E395", {"start": v(3, -31.53) * mm, "end": v(2.06, -31.54) * mm});
            skLineSegment(sketch, "E396", {"start": v(2.06, -31.54) * mm, "end": v(0.88, -31.52) * mm});
            skLineSegment(sketch, "E397", {"start": v(0.88, -31.52) * mm, "end": v(-0.27, -31.45) * mm});
            skLineSegment(sketch, "E398", {"start": v(-0.27, -31.45) * mm, "end": v(-1.38, -31.34) * mm});
            skLineSegment(sketch, "E399", {"start": v(-1.38, -31.34) * mm, "end": v(-2.47, -31.18) * mm});
            skLineSegment(sketch, "E400", {"start": v(-2.47, -31.18) * mm, "end": v(-3.52, -30.97) * mm});
            skLineSegment(sketch, "E401", {"start": v(-3.52, -30.97) * mm, "end": v(-4.54, -30.72) * mm});
            skLineSegment(sketch, "E402", {"start": v(-4.54, -30.72) * mm, "end": v(-5.53, -30.42) * mm});
            skLineSegment(sketch, "E403", {"start": v(-5.53, -30.42) * mm, "end": v(-6.5, -30.07) * mm});
            skLineSegment(sketch, "E404", {"start": v(-6.5, -30.07) * mm, "end": v(-7.42, -29.68) * mm});
            skLineSegment(sketch, "E405", {"start": v(-7.42, -29.68) * mm, "end": v(-8.32, -29.25) * mm});
            skLineSegment(sketch, "E406", {"start": v(-8.32, -29.25) * mm, "end": v(-9.19, -28.77) * mm});
            skLineSegment(sketch, "E407", {"start": v(-9.19, -28.77) * mm, "end": v(-10.03, -28.24) * mm});
            skLineSegment(sketch, "E408", {"start": v(-10.03, -28.24) * mm, "end": v(-10.83, -27.67) * mm});
            skLineSegment(sketch, "E409", {"start": v(-10.83, -27.67) * mm, "end": v(-11.6, -27.05) * mm});
            skLineSegment(sketch, "E410", {"start": v(-11.6, -27.05) * mm, "end": v(-12.35, -26.38) * mm});
            skLineSegment(sketch, "E411", {"start": v(-12.35, -26.38) * mm, "end": v(-13.07, -25.67) * mm});
            skLineSegment(sketch, "E412", {"start": v(-13.07, -25.67) * mm, "end": v(-13.74, -24.92) * mm});
            skLineSegment(sketch, "E413", {"start": v(-13.74, -24.92) * mm, "end": v(-14.38, -24.13) * mm});
            skLineSegment(sketch, "E414", {"start": v(-14.38, -24.13) * mm, "end": v(-14.97, -23.3) * mm});
            skLineSegment(sketch, "E415", {"start": v(-14.97, -23.3) * mm, "end": v(-15.51, -22.44) * mm});
            skLineSegment(sketch, "E416", {"start": v(-15.51, -22.44) * mm, "end": v(-16.01, -21.54) * mm});
            skLineSegment(sketch, "E417", {"start": v(-16.01, -21.54) * mm, "end": v(-16.47, -20.6) * mm});
            skLineSegment(sketch, "E418", {"start": v(-16.47, -20.6) * mm, "end": v(-16.89, -19.63) * mm});
            skLineSegment(sketch, "E419", {"start": v(-16.89, -19.63) * mm, "end": v(-17.26, -18.61) * mm});
            skLineSegment(sketch, "E420", {"start": v(-17.26, -18.61) * mm, "end": v(-17.58, -17.57) * mm});
            skLineSegment(sketch, "E421", {"start": v(-17.58, -17.57) * mm, "end": v(-17.87, -16.48) * mm});
            skLineSegment(sketch, "E422", {"start": v(-17.87, -16.48) * mm, "end": v(-18.1, -15.36) * mm});
            skLineSegment(sketch, "E423", {"start": v(-18.1, -15.36) * mm, "end": v(-18.3, -14.2) * mm});
            skLineSegment(sketch, "E424", {"start": v(-18.3, -14.2) * mm, "end": v(-18.46, -13) * mm});
            skLineSegment(sketch, "E425", {"start": v(-18.46, -13) * mm, "end": v(-18.57, -11.77) * mm});
            skLineSegment(sketch, "E426", {"start": v(-18.57, -11.77) * mm, "end": v(-18.63, -10.5) * mm});
            skLineSegment(sketch, "E427", {"start": v(-18.63, -10.5) * mm, "end": v(-18.65, -9.2) * mm});
            skLineSegment(sketch, "E428", {"start": v(-18.65, -9.2) * mm, "end": v(-18.63, -7.84) * mm});
            skLineSegment(sketch, "E429", {"start": v(-18.63, -7.84) * mm, "end": v(-18.57, -6.53) * mm});
            skLineSegment(sketch, "E430", {"start": v(-18.57, -6.53) * mm, "end": v(-18.46, -5.26) * mm});
            skLineSegment(sketch, "E431", {"start": v(-18.46, -5.26) * mm, "end": v(-18.3, -4.02) * mm});
            skLineSegment(sketch, "E432", {"start": v(-18.3, -4.02) * mm, "end": v(-18.1, -2.82) * mm});
            skLineSegment(sketch, "E433", {"start": v(-18.1, -2.82) * mm, "end": v(-17.86, -1.66) * mm});
            skLineSegment(sketch, "E434", {"start": v(-17.86, -1.66) * mm, "end": v(-17.57, -0.54) * mm});
            skLineSegment(sketch, "E435", {"start": v(-17.57, -0.54) * mm, "end": v(-17.24, 0.55) * mm});
            skLineSegment(sketch, "E436", {"start": v(-17.24, 0.55) * mm, "end": v(-16.87, 1.6) * mm});
            skLineSegment(sketch, "E437", {"start": v(-16.87, 1.6) * mm, "end": v(-16.45, 2.6) * mm});
            skLineSegment(sketch, "E438", {"start": v(-16.45, 2.6) * mm, "end": v(-15.98, 3.56) * mm});
            skLineSegment(sketch, "E439", {"start": v(-15.98, 3.56) * mm, "end": v(-15.48, 4.5) * mm});
            skLineSegment(sketch, "E440", {"start": v(-15.48, 4.5) * mm, "end": v(-14.93, 5.39) * mm});
            skLineSegment(sketch, "E441", {"start": v(-14.93, 5.39) * mm, "end": v(-14.33, 6.24) * mm});
            skLineSegment(sketch, "E442", {"start": v(-14.33, 6.24) * mm, "end": v(-13.69, 7.05) * mm});
            skLineSegment(sketch, "E443", {"start": v(-13.69, 7.05) * mm, "end": v(-13, 7.83) * mm});
            skLineSegment(sketch, "E444", {"start": v(-13, 7.83) * mm, "end": v(-12.29, 8.56) * mm});
            skLineSegment(sketch, "E445", {"start": v(-12.29, 8.56) * mm, "end": v(-11.54, 9.25) * mm});
            skLineSegment(sketch, "E446", {"start": v(-11.54, 9.25) * mm, "end": v(-10.77, 9.89) * mm});
            skLineSegment(sketch, "E447", {"start": v(-10.77, 9.89) * mm, "end": v(-9.97, 10.48) * mm});
            skLineSegment(sketch, "E448", {"start": v(-9.97, 10.48) * mm, "end": v(-9.15, 11.02) * mm});
            skLineSegment(sketch, "E449", {"start": v(-9.15, 11.02) * mm, "end": v(-8.3, 11.52) * mm});
            skLineSegment(sketch, "E450", {"start": v(-8.3, 11.52) * mm, "end": v(-7.42, 11.97) * mm});
            skLineSegment(sketch, "E451", {"start": v(-7.42, 11.97) * mm, "end": v(-6.52, 12.37) * mm});
            skLineSegment(sketch, "E452", {"start": v(-6.52, 12.37) * mm, "end": v(-5.59, 12.73) * mm});
            skLineSegment(sketch, "E453", {"start": v(-5.59, 12.73) * mm, "end": v(-4.63, 13.04) * mm});
            skLineSegment(sketch, "E454", {"start": v(-4.63, 13.04) * mm, "end": v(-3.65, 13.3) * mm});
            skLineSegment(sketch, "E455", {"start": v(-3.65, 13.3) * mm, "end": v(-2.65, 13.5) * mm});
            skLineSegment(sketch, "E456", {"start": v(-2.65, 13.5) * mm, "end": v(-1.61, 13.67) * mm});
            skLineSegment(sketch, "E457", {"start": v(-1.61, 13.67) * mm, "end": v(-0.55, 13.8) * mm});
            skLineSegment(sketch, "E458", {"start": v(-0.55, 13.8) * mm, "end": v(0.53, 13.86) * mm});
            skLineSegment(sketch, "E459", {"start": v(0.53, 13.86) * mm, "end": v(1.65, 13.89) * mm});
            skLineSegment(sketch, "E460", {"start": v(1.65, 13.89) * mm, "end": v(2.72, 13.86) * mm});
            skLineSegment(sketch, "E461", {"start": v(2.72, 13.86) * mm, "end": v(3.78, 13.8) * mm});
            skLineSegment(sketch, "E462", {"start": v(3.78, 13.8) * mm, "end": v(4.8, 13.68) * mm});
            skLineSegment(sketch, "E463", {"start": v(4.8, 13.68) * mm, "end": v(5.8, 13.52) * mm});
            skLineSegment(sketch, "E464", {"start": v(5.8, 13.52) * mm, "end": v(6.78, 13.3) * mm});
            skLineSegment(sketch, "E465", {"start": v(6.78, 13.3) * mm, "end": v(7.74, 13.05) * mm});
            skLineSegment(sketch, "E466", {"start": v(7.74, 13.05) * mm, "end": v(8.66, 12.75) * mm});
            skLineSegment(sketch, "E467", {"start": v(8.66, 12.75) * mm, "end": v(9.57, 12.4) * mm});
            skLineSegment(sketch, "E468", {"start": v(9.57, 12.4) * mm, "end": v(10.44, 12) * mm});
            skLineSegment(sketch, "E469", {"start": v(10.44, 12) * mm, "end": v(11.3, 11.57) * mm});
            skLineSegment(sketch, "E470", {"start": v(11.3, 11.57) * mm, "end": v(12.12, 11.08) * mm});
            skLineSegment(sketch, "E471", {"start": v(12.12, 11.08) * mm, "end": v(12.93, 10.55) * mm});
            skLineSegment(sketch, "E472", {"start": v(12.93, 10.55) * mm, "end": v(13.7, 9.97) * mm});
            skLineSegment(sketch, "E473", {"start": v(13.7, 9.97) * mm, "end": v(14.46, 9.34) * mm});
            skLineSegment(sketch, "E474", {"start": v(14.46, 9.34) * mm, "end": v(15.19, 8.67) * mm});
            skLineSegment(sketch, "E475", {"start": v(15.19, 8.67) * mm, "end": v(15.89, 7.95) * mm});
            skLineSegment(sketch, "E476", {"start": v(15.89, 7.95) * mm, "end": v(16.56, 7.2) * mm});
            skLineSegment(sketch, "E477", {"start": v(16.56, 7.2) * mm, "end": v(17.18, 6.4) * mm});
            skLineSegment(sketch, "E478", {"start": v(17.18, 6.4) * mm, "end": v(17.77, 5.56) * mm});
            skLineSegment(sketch, "E479", {"start": v(17.77, 5.56) * mm, "end": v(18.3, 4.68) * mm});
            skLineSegment(sketch, "E480", {"start": v(18.3, 4.68) * mm, "end": v(18.8, 3.77) * mm});
            skLineSegment(sketch, "E481", {"start": v(18.8, 3.77) * mm, "end": v(19.26, 2.82) * mm});
            skLineSegment(sketch, "E482", {"start": v(19.26, 2.82) * mm, "end": v(19.67, 1.84) * mm});
            skLineSegment(sketch, "E483", {"start": v(19.67, 1.84) * mm, "end": v(20.03, 0.81) * mm});
            skLineSegment(sketch, "E484", {"start": v(20.03, 0.81) * mm, "end": v(20.36, -0.25) * mm});
            skLineSegment(sketch, "E485", {"start": v(20.36, -0.25) * mm, "end": v(20.64, -1.35) * mm});
            skLineSegment(sketch, "E486", {"start": v(20.64, -1.35) * mm, "end": v(20.87, -2.49) * mm});
            skLineSegment(sketch, "E487", {"start": v(20.87, -2.49) * mm, "end": v(21.07, -3.67) * mm});
            skLineSegment(sketch, "E488", {"start": v(21.07, -3.67) * mm, "end": v(21.22, -4.88) * mm});
            skLineSegment(sketch, "E489", {"start": v(21.22, -4.88) * mm, "end": v(21.33, -6.13) * mm});
            skLineSegment(sketch, "E490", {"start": v(21.33, -6.13) * mm, "end": v(21.4, -7.42) * mm});
            skLineSegment(sketch, "E491", {"start": v(21.4, -7.42) * mm, "end": v(21.41, -8.75) * mm});
            skLineSegment(sketch, "E492", {"start": v(21.41, -8.75) * mm, "end": v(21.41, -9.11) * mm});
            skLineSegment(sketch, "E493", {"start": v(21.41, -9.11) * mm, "end": v(21.4, -9.56) * mm});
            skLineSegment(sketch, "E494", {"start": v(21.4, -9.56) * mm, "end": v(21.4, -10.1) * mm});
            skLineSegment(sketch, "E495", {"start": v(21.4, -10.1) * mm, "end": v(21.37, -10.71) * mm});
            skLineSegment(sketch, "E496", {"start": v(21.37, -10.71) * mm, "end": v(-7.03, -10.71) * mm});
            skArc(sketch, "E497", {"start": v(-6.74, -4.65) * mm, "mid": v(-7.08, -7.67) * mm, "end": v(-7.03, -10.71) * mm});
            skLineSegment(sketch, "E498", {"start": v(-6.74, -4.65) * mm, "end": v(13.64, -4.65) * mm});
            skLineSegment(sketch, "E499", {"start": v(13.64, -4.65) * mm, "end": v(13.57, -3.98) * mm});
            skLineSegment(sketch, "E500", {"start": v(13.57, -3.98) * mm, "end": v(13.49, -3.32) * mm});
            skLineSegment(sketch, "E501", {"start": v(13.49, -3.32) * mm, "end": v(13.4, -2.7) * mm});
            skLineSegment(sketch, "E502", {"start": v(13.4, -2.7) * mm, "end": v(13.28, -2.08) * mm});
            skLineSegment(sketch, "E503", {"start": v(13.28, -2.08) * mm, "end": v(13.16, -1.5) * mm});
            skLineSegment(sketch, "E504", {"start": v(13.16, -1.5) * mm, "end": v(13.02, -0.93) * mm});
            skLineSegment(sketch, "E505", {"start": v(13.02, -0.93) * mm, "end": v(12.86, -0.38) * mm});
            skLineSegment(sketch, "E506", {"start": v(12.86, -0.38) * mm, "end": v(12.7, 0.15) * mm});
            skLineSegment(sketch, "E507", {"start": v(12.7, 0.15) * mm, "end": v(12.52, 0.65) * mm});
            skLineSegment(sketch, "E508", {"start": v(12.52, 0.65) * mm, "end": v(12.32, 1.13) * mm});
            skLineSegment(sketch, "E509", {"start": v(12.32, 1.13) * mm, "end": v(12.11, 1.6) * mm});
            skLineSegment(sketch, "E510", {"start": v(12.11, 1.6) * mm, "end": v(11.89, 2.03) * mm});
            skLineSegment(sketch, "E511", {"start": v(11.89, 2.03) * mm, "end": v(11.65, 2.45) * mm});
            skLineSegment(sketch, "E512", {"start": v(11.65, 2.45) * mm, "end": v(11.4, 2.85) * mm});
            skLineSegment(sketch, "E513", {"start": v(11.4, 2.85) * mm, "end": v(11.13, 3.22) * mm});
            skLineSegment(sketch, "E514", {"start": v(11.13, 3.22) * mm, "end": v(10.86, 3.57) * mm});
            skLineSegment(sketch, "E515", {"start": v(10.86, 3.57) * mm, "end": v(10.4, 4.09) * mm});
            skLineSegment(sketch, "E516", {"start": v(10.4, 4.09) * mm, "end": v(9.94, 4.57) * mm});
            skLineSegment(sketch, "E517", {"start": v(9.94, 4.57) * mm, "end": v(9.46, 5.02) * mm});
            skLineSegment(sketch, "E518", {"start": v(9.46, 5.02) * mm, "end": v(8.96, 5.44) * mm});
            skLineSegment(sketch, "E519", {"start": v(8.96, 5.44) * mm, "end": v(8.45, 5.82) * mm});
            skLineSegment(sketch, "E520", {"start": v(8.45, 5.82) * mm, "end": v(7.92, 6.17) * mm});
            skLineSegment(sketch, "E521", {"start": v(7.92, 6.17) * mm, "end": v(7.38, 6.48) * mm});
            skLineSegment(sketch, "E522", {"start": v(7.38, 6.48) * mm, "end": v(6.81, 6.77) * mm});
            skLineSegment(sketch, "E523", {"start": v(6.81, 6.77) * mm, "end": v(6.24, 7.02) * mm});
            skLineSegment(sketch, "E524", {"start": v(6.24, 7.02) * mm, "end": v(5.64, 7.23) * mm});
            skLineSegment(sketch, "E525", {"start": v(5.64, 7.23) * mm, "end": v(5.03, 7.41) * mm});
            skLineSegment(sketch, "E526", {"start": v(5.03, 7.41) * mm, "end": v(4.4, 7.56) * mm});
            skLineSegment(sketch, "E527", {"start": v(4.4, 7.56) * mm, "end": v(3.76, 7.68) * mm});
            skLineSegment(sketch, "E528", {"start": v(3.76, 7.68) * mm, "end": v(3.1, 7.76) * mm});
            skLineSegment(sketch, "E529", {"start": v(3.1, 7.76) * mm, "end": v(2.42, 7.81) * mm});
            skLineSegment(sketch, "E530", {"start": v(2.42, 7.81) * mm, "end": v(1.73, 7.83) * mm});
            skLineSegment(sketch, "E531", {"start": v(1.73, 7.83) * mm, "end": v(1.1, 7.82) * mm});
            skLineSegment(sketch, "E532", {"start": v(1.1, 7.82) * mm, "end": v(0.48, 7.78) * mm});
            skLineSegment(sketch, "E533", {"start": v(0.48, 7.78) * mm, "end": v(-0.12, 7.71) * mm});
            skLineSegment(sketch, "E534", {"start": v(-0.12, 7.71) * mm, "end": v(-0.7, 7.62) * mm});
            skLineSegment(sketch, "E535", {"start": v(-0.7, 7.62) * mm, "end": v(-1.29, 7.5) * mm});
            skLineSegment(sketch, "E536", {"start": v(-1.29, 7.5) * mm, "end": v(-1.85, 7.35) * mm});
            skLineSegment(sketch, "E537", {"start": v(-1.85, 7.35) * mm, "end": v(-2.4, 7.18) * mm});
            skLineSegment(sketch, "E538", {"start": v(-2.4, 7.18) * mm, "end": v(-2.94, 6.98) * mm});
            skLineSegment(sketch, "E539", {"start": v(-2.94, 6.98) * mm, "end": v(-3.47, 6.76) * mm});
            skLineSegment(sketch, "E540", {"start": v(-3.47, 6.76) * mm, "end": v(-3.98, 6.5) * mm});
            skLineSegment(sketch, "E541", {"start": v(-3.98, 6.5) * mm, "end": v(-4.49, 6.22) * mm});
            skLineSegment(sketch, "E542", {"start": v(-4.49, 6.22) * mm, "end": v(-4.97, 5.92) * mm});
            skLineSegment(sketch, "E543", {"start": v(-4.97, 5.92) * mm, "end": v(-5.45, 5.59) * mm});
            skLineSegment(sketch, "E544", {"start": v(-5.45, 5.59) * mm, "end": v(-5.92, 5.23) * mm});
            skLineSegment(sketch, "E545", {"start": v(-5.92, 5.23) * mm, "end": v(-6.37, 4.84) * mm});
            skLineSegment(sketch, "E546", {"start": v(-6.37, 4.84) * mm, "end": v(-6.8, 4.43) * mm});
            skLineSegment(sketch, "E547", {"start": v(-6.8, 4.43) * mm, "end": v(-7.23, 4) * mm});
            skLineSegment(sketch, "E548", {"start": v(-7.23, 4) * mm, "end": v(-7.62, 3.55) * mm});
            skLineSegment(sketch, "E549", {"start": v(-7.62, 3.55) * mm, "end": v(-8, 3.08) * mm});
            skLineSegment(sketch, "E550", {"start": v(-8, 3.08) * mm, "end": v(-8.34, 2.6) * mm});
            skLineSegment(sketch, "E551", {"start": v(-8.34, 2.6) * mm, "end": v(-8.66, 2.09) * mm});
            skLineSegment(sketch, "E552", {"start": v(-8.66, 2.09) * mm, "end": v(-8.96, 1.56) * mm});
            skLineSegment(sketch, "E553", {"start": v(-8.96, 1.56) * mm, "end": v(-9.24, 1.02) * mm});
            skLineSegment(sketch, "E554", {"start": v(-9.24, 1.02) * mm, "end": v(-9.5, 0.46) * mm});
            skLineSegment(sketch, "E555", {"start": v(-9.5, 0.46) * mm, "end": v(-9.72, -0.11) * mm});
            skLineSegment(sketch, "E556", {"start": v(-9.72, -0.11) * mm, "end": v(-9.92, -0.7) * mm});
            skLineSegment(sketch, "E557", {"start": v(-9.92, -0.7) * mm, "end": v(-10.1, -1.32) * mm});
            skLineSegment(sketch, "E558", {"start": v(-10.1, -1.32) * mm, "end": v(-10.25, -1.95) * mm});
            skArc(sketch, "E559", {"start": v(-10.25, -1.95) * mm, "mid": v(-11.1, -8.78) * mm, "end": v(-10.28, -15.6) * mm});
            skLineSegment(sketch, "E560", {"start": v(-10.28, -15.6) * mm, "end": v(-9.82, -17.03) * mm});
            skLineSegment(sketch, "E561", {"start": v(-9.82, -17.03) * mm, "end": v(-9.56, -17.7) * mm});
            skLineSegment(sketch, "E562", {"start": v(-9.56, -17.7) * mm, "end": v(-9.27, -18.35) * mm});
            skLineSegment(sketch, "E563", {"start": v(-9.27, -18.35) * mm, "end": v(-8.95, -18.97) * mm});
            skLineSegment(sketch, "E564", {"start": v(-8.95, -18.97) * mm, "end": v(-8.6, -19.57) * mm});
            skLineSegment(sketch, "E565", {"start": v(-8.6, -19.57) * mm, "end": v(-8.24, -20.13) * mm});
            skLineSegment(sketch, "E566", {"start": v(-8.24, -20.13) * mm, "end": v(-7.85, -20.67) * mm});
            skLineSegment(sketch, "E567", {"start": v(-7.85, -20.67) * mm, "end": v(-7.43, -21.19) * mm});
            skLineSegment(sketch, "E568", {"start": v(-7.43, -21.19) * mm, "end": v(-6.99, -21.68) * mm});
            skLineSegment(sketch, "E569", {"start": v(-6.99, -21.68) * mm, "end": v(-6.53, -22.14) * mm});
            skLineSegment(sketch, "E570", {"start": v(-6.53, -22.14) * mm, "end": v(-6.05, -22.57) * mm});
            skLineSegment(sketch, "E571", {"start": v(-6.05, -22.57) * mm, "end": v(-5.56, -22.97) * mm});
            skLineSegment(sketch, "E572", {"start": v(-5.56, -22.97) * mm, "end": v(-5.06, -23.34) * mm});
            skLineSegment(sketch, "E573", {"start": v(-5.06, -23.34) * mm, "end": v(-4.54, -23.69) * mm});
            skLineSegment(sketch, "E574", {"start": v(-97.98, 6.93) * mm, "end": v(-98.38, 6.76) * mm});
            skLineSegment(sketch, "E575", {"start": v(-98.38, 6.76) * mm, "end": v(-98.77, 6.59) * mm});
            skLineSegment(sketch, "E576", {"start": v(-98.77, 6.59) * mm, "end": v(-99.13, 6.4) * mm});
            skLineSegment(sketch, "E577", {"start": v(-99.13, 6.4) * mm, "end": v(-99.47, 6.19) * mm});
            skLineSegment(sketch, "E578", {"start": v(-99.47, 6.19) * mm, "end": v(-99.8, 5.97) * mm});
            skLineSegment(sketch, "E579", {"start": v(-99.8, 5.97) * mm, "end": v(-100.1, 5.73) * mm});
            skLineSegment(sketch, "E580", {"start": v(-100.1, 5.73) * mm, "end": v(-100.4, 5.47) * mm});
            skLineSegment(sketch, "E581", {"start": v(-100.4, 5.47) * mm, "end": v(-100.68, 5.19) * mm});
            skLineSegment(sketch, "E582", {"start": v(-100.68, 5.19) * mm, "end": v(-100.95, 4.88) * mm});
            skLineSegment(sketch, "E583", {"start": v(-100.95, 4.88) * mm, "end": v(-101.21, 4.56) * mm});
            skLineSegment(sketch, "E584", {"start": v(-101.21, 4.56) * mm, "end": v(-101.47, 4.2) * mm});
            skLineSegment(sketch, "E585", {"start": v(-101.47, 4.2) * mm, "end": v(-101.71, 3.84) * mm});
            skLineSegment(sketch, "E586", {"start": v(-101.71, 3.84) * mm, "end": v(-101.95, 3.45) * mm});
            skLineSegment(sketch, "E587", {"start": v(-101.95, 3.45) * mm, "end": v(-102.17, 3.03) * mm});
            skLineSegment(sketch, "E588", {"start": v(-102.17, 3.03) * mm, "end": v(-102.38, 2.6) * mm});
            skLineSegment(sketch, "E589", {"start": v(-102.38, 2.6) * mm, "end": v(-102.59, 2.14) * mm});
            skLineSegment(sketch, "E590", {"start": v(-102.59, 2.14) * mm, "end": v(-102.78, 1.66) * mm});
            skLineSegment(sketch, "E591", {"start": v(-102.78, 1.66) * mm, "end": v(-102.97, 1.16) * mm});
            skLineSegment(sketch, "E592", {"start": v(-102.97, 1.16) * mm, "end": v(-103.14, 0.63) * mm});
            skLineSegment(sketch, "E593", {"start": v(-103.14, 0.63) * mm, "end": v(-103.3, 0.09) * mm});
            skLineSegment(sketch, "E594", {"start": v(-103.3, 0.09) * mm, "end": v(-103.46, -0.48) * mm});
            skLineSegment(sketch, "E595", {"start": v(-103.46, -0.48) * mm, "end": v(-110.66, 0.5) * mm});
            skLineSegment(sketch, "E596", {"start": v(-110.66, 0.5) * mm, "end": v(-110.4, 1.63) * mm});
            skLineSegment(sketch, "E597", {"start": v(-110.4, 1.63) * mm, "end": v(-110.09, 2.7) * mm});
            skLineSegment(sketch, "E598", {"start": v(-110.09, 2.7) * mm, "end": v(-109.74, 3.72) * mm});
            skLineSegment(sketch, "E599", {"start": v(-109.74, 3.72) * mm, "end": v(-109.36, 4.68) * mm});
            skLineSegment(sketch, "E600", {"start": v(-109.36, 4.68) * mm, "end": v(-108.94, 5.59) * mm});
            skLineSegment(sketch, "E601", {"start": v(-108.94, 5.59) * mm, "end": v(-108.47, 6.44) * mm});
            skLineSegment(sketch, "E602", {"start": v(-108.47, 6.44) * mm, "end": v(-107.97, 7.23) * mm});
            skLineSegment(sketch, "E603", {"start": v(-107.97, 7.23) * mm, "end": v(-107.43, 7.97) * mm});
            skLineSegment(sketch, "E604", {"start": v(-107.43, 7.97) * mm, "end": v(-106.83, 8.66) * mm});
            skLineSegment(sketch, "E605", {"start": v(-106.83, 8.66) * mm, "end": v(-106.17, 9.31) * mm});
            skLineSegment(sketch, "E606", {"start": v(-106.17, 9.31) * mm, "end": v(-105.46, 9.92) * mm});
            skLineSegment(sketch, "E607", {"start": v(-105.46, 9.92) * mm, "end": v(-104.67, 10.5) * mm});
            skLineSegment(sketch, "E608", {"start": v(-104.67, 10.5) * mm, "end": v(-103.83, 11.02) * mm});
            skLineSegment(sketch, "E609", {"start": v(-103.83, 11.02) * mm, "end": v(-102.92, 11.5) * mm});
            skLineSegment(sketch, "E610", {"start": v(-102.92, 11.5) * mm, "end": v(-101.95, 11.95) * mm});
            skLineSegment(sketch, "E611", {"start": v(-101.95, 11.95) * mm, "end": v(-100.92, 12.35) * mm});
            skLineSegment(sketch, "E612", {"start": v(-100.92, 12.35) * mm, "end": v(-99.83, 12.71) * mm});
            skLineSegment(sketch, "E613", {"start": v(-99.83, 12.71) * mm, "end": v(-98.7, 13.02) * mm});
            skLineSegment(sketch, "E614", {"start": v(-98.7, 13.02) * mm, "end": v(-97.54, 13.29) * mm});
            skLineSegment(sketch, "E615", {"start": v(-97.54, 13.29) * mm, "end": v(-96.32, 13.5) * mm});
            skLineSegment(sketch, "E616", {"start": v(-96.32, 13.5) * mm, "end": v(-95.07, 13.67) * mm});
            skLineSegment(sketch, "E617", {"start": v(-95.07, 13.67) * mm, "end": v(-93.77, 13.8) * mm});
            skLineSegment(sketch, "E618", {"start": v(-93.77, 13.8) * mm, "end": v(-92.44, 13.86) * mm});
            skLineSegment(sketch, "E619", {"start": v(-92.44, 13.86) * mm, "end": v(-91.05, 13.89) * mm});
            skLineSegment(sketch, "E620", {"start": v(-91.05, 13.89) * mm, "end": v(-89.7, 13.87) * mm});
            skLineSegment(sketch, "E621", {"start": v(-89.7, 13.87) * mm, "end": v(-88.4, 13.8) * mm});
            skLineSegment(sketch, "E622", {"start": v(-88.4, 13.8) * mm, "end": v(-87.17, 13.7) * mm});
            skLineSegment(sketch, "E623", {"start": v(-87.17, 13.7) * mm, "end": v(-86.01, 13.56) * mm});
            skLineSegment(sketch, "E624", {"start": v(-86.01, 13.56) * mm, "end": v(-84.91, 13.38) * mm});
            skLineSegment(sketch, "E625", {"start": v(-84.91, 13.38) * mm, "end": v(-83.88, 13.15) * mm});
            skLineSegment(sketch, "E626", {"start": v(-83.88, 13.15) * mm, "end": v(-82.91, 12.88) * mm});
            skLineSegment(sketch, "E627", {"start": v(-82.91, 12.88) * mm, "end": v(-82, 12.58) * mm});
            skLineSegment(sketch, "E628", {"start": v(-82, 12.58) * mm, "end": v(-81.17, 12.24) * mm});
            skLineSegment(sketch, "E629", {"start": v(-81.17, 12.24) * mm, "end": v(-80.39, 11.88) * mm});
            skLineSegment(sketch, "E630", {"start": v(-80.39, 11.88) * mm, "end": v(-79.66, 11.5) * mm});
            skLineSegment(sketch, "E631", {"start": v(-79.66, 11.5) * mm, "end": v(-79, 11.1) * mm});
            skLineSegment(sketch, "E632", {"start": v(-79, 11.1) * mm, "end": v(-78.38, 10.68) * mm});
            skLineSegment(sketch, "E633", {"start": v(-78.38, 10.68) * mm, "end": v(-77.83, 10.23) * mm});
            skLineSegment(sketch, "E634", {"start": v(-77.83, 10.23) * mm, "end": v(-77.33, 9.77) * mm});
            skLineSegment(sketch, "E635", {"start": v(-77.33, 9.77) * mm, "end": v(-76.9, 9.28) * mm});
            skLineSegment(sketch, "E636", {"start": v(-76.9, 9.28) * mm, "end": v(-76.5, 8.77) * mm});
            skLineSegment(sketch, "E637", {"start": v(-76.5, 8.77) * mm, "end": v(-76.14, 8.23) * mm});
            skLineSegment(sketch, "E638", {"start": v(-76.14, 8.23) * mm, "end": v(-75.8, 7.65) * mm});
            skLineSegment(sketch, "E639", {"start": v(-75.8, 7.65) * mm, "end": v(-75.5, 7.04) * mm});
            skLineSegment(sketch, "E640", {"start": v(-75.5, 7.04) * mm, "end": v(-75.23, 6.4) * mm});
            skLineSegment(sketch, "E641", {"start": v(-75.23, 6.4) * mm, "end": v(-75, 5.72) * mm});
            skLineSegment(sketch, "E642", {"start": v(-75, 5.72) * mm, "end": v(-74.78, 5.01) * mm});
            skLineSegment(sketch, "E643", {"start": v(-74.78, 5.01) * mm, "end": v(-74.6, 4.27) * mm});
            skLineSegment(sketch, "E644", {"start": v(-74.6, 4.27) * mm, "end": v(-74.52, 3.75) * mm});
            skLineSegment(sketch, "E645", {"start": v(-74.52, 3.75) * mm, "end": v(-74.44, 3.14) * mm});
            skLineSegment(sketch, "E646", {"start": v(-74.44, 3.14) * mm, "end": v(-74.38, 2.43) * mm});
            skLineSegment(sketch, "E647", {"start": v(-74.38, 2.43) * mm, "end": v(-74.33, 1.63) * mm});
            skLineSegment(sketch, "E648", {"start": v(-74.33, 1.63) * mm, "end": v(-74.29, 0.73) * mm});
            skLineSegment(sketch, "E649", {"start": v(-74.29, 0.73) * mm, "end": v(-74.26, -0.26) * mm});
            skLineSegment(sketch, "E650", {"start": v(-74.26, -0.26) * mm, "end": v(-74.24, -1.34) * mm});
            skLineSegment(sketch, "E651", {"start": v(-74.24, -1.34) * mm, "end": v(-74.23, -2.52) * mm});
            skLineSegment(sketch, "E652", {"start": v(-74.23, -2.52) * mm, "end": v(-74.23, -12.35) * mm});
            skLineSegment(sketch, "E653", {"start": v(-74.23, -12.35) * mm, "end": v(-74.23, -13.6) * mm});
            skLineSegment(sketch, "E654", {"start": v(-74.23, -13.6) * mm, "end": v(-74.23, -14.8) * mm});
            skLineSegment(sketch, "E655", {"start": v(-74.23, -14.8) * mm, "end": v(-74.22, -15.93) * mm});
            skLineSegment(sketch, "E656", {"start": v(-74.22, -15.93) * mm, "end": v(-74.2, -17.01) * mm});
            skLineSegment(sketch, "E657", {"start": v(-74.2, -17.01) * mm, "end": v(-74.19, -18.03) * mm});
            skLineSegment(sketch, "E658", {"start": v(-74.19, -18.03) * mm, "end": v(-74.17, -18.99) * mm});
            skLineSegment(sketch, "E659", {"start": v(-74.17, -18.99) * mm, "end": v(-74.14, -19.9) * mm});
            skLineSegment(sketch, "E660", {"start": v(-74.14, -19.9) * mm, "end": v(-74.12, -20.73) * mm});
            skLineSegment(sketch, "E661", {"start": v(-74.12, -20.73) * mm, "end": v(-74.08, -21.51) * mm});
            skLineSegment(sketch, "E662", {"start": v(-74.08, -21.51) * mm, "end": v(-74.05, -22.24) * mm});
            skLineSegment(sketch, "E663", {"start": v(-74.05, -22.24) * mm, "end": v(-74.01, -22.9) * mm});
            skLineSegment(sketch, "E664", {"start": v(-74.01, -22.9) * mm, "end": v(-73.97, -23.5) * mm});
            skLineSegment(sketch, "E665", {"start": v(-73.97, -23.5) * mm, "end": v(-73.92, -24.06) * mm});
            skLineSegment(sketch, "E666", {"start": v(-73.92, -24.06) * mm, "end": v(-73.87, -24.54) * mm});
            skLineSegment(sketch, "E667", {"start": v(-73.87, -24.54) * mm, "end": v(-73.82, -24.97) * mm});
            skLineSegment(sketch, "E668", {"start": v(-73.82, -24.97) * mm, "end": v(-73.76, -25.34) * mm});
            skLineSegment(sketch, "E669", {"start": v(-73.76, -25.34) * mm, "end": v(-73.63, -26.02) * mm});
            skLineSegment(sketch, "E670", {"start": v(-73.63, -26.02) * mm, "end": v(-73.47, -26.69) * mm});
            skLineSegment(sketch, "E671", {"start": v(-73.47, -26.69) * mm, "end": v(-73.28, -27.35) * mm});
            skLineSegment(sketch, "E672", {"start": v(-73.28, -27.35) * mm, "end": v(-73.06, -28) * mm});
            skLineSegment(sketch, "E673", {"start": v(-73.06, -28) * mm, "end": v(-72.81, -28.66) * mm});
            skLineSegment(sketch, "E674", {"start": v(-72.81, -28.66) * mm, "end": v(-72.54, -29.3) * mm});
            skLineSegment(sketch, "E675", {"start": v(-72.54, -29.3) * mm, "end": v(-72.23, -29.93) * mm});
            skLineSegment(sketch, "E676", {"start": v(-72.23, -29.93) * mm, "end": v(-71.9, -30.56) * mm});
            skLineSegment(sketch, "E677", {"start": v(-71.9, -30.56) * mm, "end": v(-79.6, -30.56) * mm});
            skLineSegment(sketch, "E678", {"start": v(-79.6, -30.56) * mm, "end": v(-79.87, -29.97) * mm});
            skLineSegment(sketch, "E679", {"start": v(-79.87, -29.97) * mm, "end": v(-80.12, -29.37) * mm});
            skLineSegment(sketch, "E680", {"start": v(-80.12, -29.37) * mm, "end": v(-80.34, -28.73) * mm});
            skLineSegment(sketch, "E681", {"start": v(-80.34, -28.73) * mm, "end": v(-80.54, -28.07) * mm});
            skLineSegment(sketch, "E682", {"start": v(-80.54, -28.07) * mm, "end": v(-80.7, -27.4) * mm});
            skLineSegment(sketch, "E683", {"start": v(-80.7, -27.4) * mm, "end": v(-80.85, -26.68) * mm});
            skLineSegment(sketch, "E684", {"start": v(-80.85, -26.68) * mm, "end": v(-80.97, -25.95) * mm});
            skLineSegment(sketch, "E685", {"start": v(-80.97, -25.95) * mm, "end": v(-81.07, -25.2) * mm});
            skLineSegment(sketch, "E686", {"start": v(-81.07, -25.2) * mm, "end": v(-82.09, -26.04) * mm});
            skLineSegment(sketch, "E687", {"start": v(-82.09, -26.04) * mm, "end": v(-83.1, -26.8) * mm});
            skLineSegment(sketch, "E688", {"start": v(-83.1, -26.8) * mm, "end": v(-84.1, -27.52) * mm});
            skLineSegment(sketch, "E689", {"start": v(-84.1, -27.52) * mm, "end": v(-85.08, -28.17) * mm});
            skLineSegment(sketch, "E690", {"start": v(-85.08, -28.17) * mm, "end": v(-86.06, -28.75) * mm});
            skLineSegment(sketch, "E691", {"start": v(-86.06, -28.75) * mm, "end": v(-87.03, -29.27) * mm});
            skLineSegment(sketch, "E692", {"start": v(-87.03, -29.27) * mm, "end": v(-88, -29.72) * mm});
            skLineSegment(sketch, "E693", {"start": v(-88, -29.72) * mm, "end": v(-88.95, -30.1) * mm});
            skLineSegment(sketch, "E694", {"start": v(-88.95, -30.1) * mm, "end": v(-89.9, -30.45) * mm});
            skLineSegment(sketch, "E695", {"start": v(-89.9, -30.45) * mm, "end": v(-90.87, -30.74) * mm});
            skLineSegment(sketch, "E696", {"start": v(-90.87, -30.74) * mm, "end": v(-91.86, -30.98) * mm});
            skLineSegment(sketch, "E697", {"start": v(-91.86, -30.98) * mm, "end": v(-92.87, -31.18) * mm});
            skLineSegment(sketch, "E698", {"start": v(-92.87, -31.18) * mm, "end": v(-93.9, -31.34) * mm});
            skLineSegment(sketch, "E699", {"start": v(-93.9, -31.34) * mm, "end": v(-94.94, -31.45) * mm});
            skLineSegment(sketch, "E700", {"start": v(-94.94, -31.45) * mm, "end": v(-96, -31.52) * mm});
            skLineSegment(sketch, "E701", {"start": v(-96, -31.52) * mm, "end": v(-97.07, -31.54) * mm});
            skLineSegment(sketch, "E702", {"start": v(-97.07, -31.54) * mm, "end": v(-97.95, -31.53) * mm});
            skLineSegment(sketch, "E703", {"start": v(-97.95, -31.53) * mm, "end": v(-98.8, -31.49) * mm});
            skLineSegment(sketch, "E704", {"start": v(-98.8, -31.49) * mm, "end": v(-99.64, -31.42) * mm});
            skLineSegment(sketch, "E705", {"start": v(-99.64, -31.42) * mm, "end": v(-100.45, -31.32) * mm});
            skLineSegment(sketch, "E706", {"start": v(-100.45, -31.32) * mm, "end": v(-101.22, -31.2) * mm});
            skLineSegment(sketch, "E707", {"start": v(-101.22, -31.2) * mm, "end": v(-101.98, -31.05) * mm});
            skLineSegment(sketch, "E708", {"start": v(-101.98, -31.05) * mm, "end": v(-102.7, -30.87) * mm});
            skLineSegment(sketch, "E709", {"start": v(-102.7, -30.87) * mm, "end": v(-103.4, -30.67) * mm});
            skLineSegment(sketch, "E710", {"start": v(-103.4, -30.67) * mm, "end": v(-104.08, -30.44) * mm});
            skLineSegment(sketch, "E711", {"start": v(-104.08, -30.44) * mm, "end": v(-104.73, -30.18) * mm});
            skLineSegment(sketch, "E712", {"start": v(-104.73, -30.18) * mm, "end": v(-105.35, -29.89) * mm});
            skLineSegment(sketch, "E713", {"start": v(-105.35, -29.89) * mm, "end": v(-105.95, -29.57) * mm});
            skLineSegment(sketch, "E714", {"start": v(-105.95, -29.57) * mm, "end": v(-106.52, -29.23) * mm});
            skLineSegment(sketch, "E715", {"start": v(-106.52, -29.23) * mm, "end": v(-107.07, -28.86) * mm});
            skLineSegment(sketch, "E716", {"start": v(-107.07, -28.86) * mm, "end": v(-107.59, -28.47) * mm});
            skLineSegment(sketch, "E717", {"start": v(-107.59, -28.47) * mm, "end": v(-108.08, -28.04) * mm});
            skLineSegment(sketch, "E718", {"start": v(-108.08, -28.04) * mm, "end": v(-108.55, -27.6) * mm});
            skLineSegment(sketch, "E719", {"start": v(-108.55, -27.6) * mm, "end": v(-108.98, -27.14) * mm});
            skLineSegment(sketch, "E720", {"start": v(-108.98, -27.14) * mm, "end": v(-109.39, -26.66) * mm});
            skLineSegment(sketch, "E721", {"start": v(-109.39, -26.66) * mm, "end": v(-109.76, -26.17) * mm});
            skLineSegment(sketch, "E722", {"start": v(-109.76, -26.17) * mm, "end": v(-110.1, -25.67) * mm});
            skLineSegment(sketch, "E723", {"start": v(-110.1, -25.67) * mm, "end": v(-110.43, -25.15) * mm});
            skLineSegment(sketch, "E724", {"start": v(-110.43, -25.15) * mm, "end": v(-110.71, -24.6) * mm});
            skLineSegment(sketch, "E725", {"start": v(-110.71, -24.6) * mm, "end": v(-110.97, -24.06) * mm});
            skLineSegment(sketch, "E726", {"start": v(-110.97, -24.06) * mm, "end": v(-111.2, -23.5) * mm});
            skLineSegment(sketch, "E727", {"start": v(-111.2, -23.5) * mm, "end": v(-111.39, -22.9) * mm});
            skLineSegment(sketch, "E728", {"start": v(-111.39, -22.9) * mm, "end": v(-111.55, -22.31) * mm});
            skLineSegment(sketch, "E729", {"start": v(-111.55, -22.31) * mm, "end": v(-111.69, -21.7) * mm});
            skLineSegment(sketch, "E730", {"start": v(-111.69, -21.7) * mm, "end": v(-111.8, -21.07) * mm});
            skLineSegment(sketch, "E731", {"start": v(-111.8, -21.07) * mm, "end": v(-111.87, -20.43) * mm});
            skLineSegment(sketch, "E732", {"start": v(-111.87, -20.43) * mm, "end": v(-111.91, -19.77) * mm});
            skLineSegment(sketch, "E733", {"start": v(-111.91, -19.77) * mm, "end": v(-111.93, -19.1) * mm});
            skLineSegment(sketch, "E734", {"start": v(-111.93, -19.1) * mm, "end": v(-111.9, -18.31) * mm});
            skLineSegment(sketch, "E735", {"start": v(-111.9, -18.31) * mm, "end": v(-111.84, -17.54) * mm});
            skLineSegment(sketch, "E736", {"start": v(-111.84, -17.54) * mm, "end": v(-111.72, -16.78) * mm});
            skLineSegment(sketch, "E737", {"start": v(-111.72, -16.78) * mm, "end": v(-111.56, -16.05) * mm});
            skLineSegment(sketch, "E738", {"start": v(-111.56, -16.05) * mm, "end": v(-111.36, -15.33) * mm});
            skLineSegment(sketch, "E739", {"start": v(-111.36, -15.33) * mm, "end": v(-111.11, -14.62) * mm});
            skLineSegment(sketch, "E740", {"start": v(-111.11, -14.62) * mm, "end": v(-110.82, -13.94) * mm});
            skLineSegment(sketch, "E741", {"start": v(-110.82, -13.94) * mm, "end": v(-110.47, -13.27) * mm});
            skLineSegment(sketch, "E742", {"start": v(-110.47, -13.27) * mm, "end": v(-110.1, -12.62) * mm});
            skLineSegment(sketch, "E743", {"start": v(-110.1, -12.62) * mm, "end": v(-109.7, -12.01) * mm});
            skLineSegment(sketch, "E744", {"start": v(-109.7, -12.01) * mm, "end": v(-109.26, -11.43) * mm});
            skLineSegment(sketch, "E745", {"start": v(-109.26, -11.43) * mm, "end": v(-108.8, -10.89) * mm});
            skLineSegment(sketch, "E746", {"start": v(-108.8, -10.89) * mm, "end": v(-108.3, -10.38) * mm});
            skLineSegment(sketch, "E747", {"start": v(-108.3, -10.38) * mm, "end": v(-107.79, -9.9) * mm});
            skLineSegment(sketch, "E748", {"start": v(-107.79, -9.9) * mm, "end": v(-107.24, -9.45) * mm});
            skLineSegment(sketch, "E749", {"start": v(-107.24, -9.45) * mm, "end": v(-106.67, -9.03) * mm});
            skLineSegment(sketch, "E750", {"start": v(-106.67, -9.03) * mm, "end": v(-106.07, -8.65) * mm});
            skLineSegment(sketch, "E751", {"start": v(-106.07, -8.65) * mm, "end": v(-105.45, -8.28) * mm});
            skLineSegment(sketch, "E752", {"start": v(-105.45, -8.28) * mm, "end": v(-104.82, -7.94) * mm});
            skLineSegment(sketch, "E753", {"start": v(-104.82, -7.94) * mm, "end": v(-104.17, -7.63) * mm});
            skLineSegment(sketch, "E754", {"start": v(-104.17, -7.63) * mm, "end": v(-103.5, -7.34) * mm});
            skLineSegment(sketch, "E755", {"start": v(-103.5, -7.34) * mm, "end": v(-102.8, -7.08) * mm});
            skLineSegment(sketch, "E756", {"start": v(-102.8, -7.08) * mm, "end": v(-102.1, -6.83) * mm});
            skLineSegment(sketch, "E757", {"start": v(-102.1, -6.83) * mm, "end": v(-101.37, -6.62) * mm});
            skLineSegment(sketch, "E758", {"start": v(-101.37, -6.62) * mm, "end": v(-100.8, -6.47) * mm});
            skLineSegment(sketch, "E759", {"start": v(-100.8, -6.47) * mm, "end": v(-100.15, -6.33) * mm});
            skLineSegment(sketch, "E760", {"start": v(-100.15, -6.33) * mm, "end": v(-99.43, -6.2) * mm});
            skLineSegment(sketch, "E761", {"start": v(-99.43, -6.2) * mm, "end": v(-98.65, -6.05) * mm});
            skLineSegment(sketch, "E762", {"start": v(-98.65, -6.05) * mm, "end": v(-97.8, -5.92) * mm});
            skLineSegment(sketch, "E763", {"start": v(-97.8, -5.92) * mm, "end": v(-96.87, -5.78) * mm});
            skLineSegment(sketch, "E764", {"start": v(-96.87, -5.78) * mm, "end": v(-95.88, -5.65) * mm});
            skLineSegment(sketch, "E765", {"start": v(-95.88, -5.65) * mm, "end": v(-94.82, -5.51) * mm});
            skLineSegment(sketch, "E766", {"start": v(-94.82, -5.51) * mm, "end": v(-93.72, -5.38) * mm});
            skLineSegment(sketch, "E767", {"start": v(-93.72, -5.38) * mm, "end": v(-92.66, -5.24) * mm});
            skLineSegment(sketch, "E768", {"start": v(-92.66, -5.24) * mm, "end": v(-91.64, -5.1) * mm});
            skLineSegment(sketch, "E769", {"start": v(-91.64, -5.1) * mm, "end": v(-90.65, -4.95) * mm});
            skLineSegment(sketch, "E770", {"start": v(-90.65, -4.95) * mm, "end": v(-89.7, -4.8) * mm});
            skLineSegment(sketch, "E771", {"start": v(-89.7, -4.8) * mm, "end": v(-88.8, -4.66) * mm});
            skLineSegment(sketch, "E772", {"start": v(-88.8, -4.66) * mm, "end": v(-87.91, -4.5) * mm});
            skLineSegment(sketch, "E773", {"start": v(-87.91, -4.5) * mm, "end": v(-87.07, -4.35) * mm});
            skLineSegment(sketch, "E774", {"start": v(-87.07, -4.35) * mm, "end": v(-86.27, -4.19) * mm});
            skLineSegment(sketch, "E775", {"start": v(-86.27, -4.19) * mm, "end": v(-85.67, -4.06) * mm});
            skLineSegment(sketch, "E776", {"start": v(-85.68, -10.01) * mm, "end": v(-85.67, -4.06) * mm});
            skLineSegment(sketch, "E777", {"start": v(-85.68, -10.01) * mm, "end": v(-85.96, -10.08) * mm});
            skLineSegment(sketch, "E778", {"start": v(-85.96, -10.08) * mm, "end": v(-86.7, -10.26) * mm});
            skLineSegment(sketch, "E779", {"start": v(-86.7, -10.26) * mm, "end": v(-87.46, -10.43) * mm});
            skLineSegment(sketch, "E780", {"start": v(-87.46, -10.43) * mm, "end": v(-88.26, -10.6) * mm});
            skLineSegment(sketch, "E781", {"start": v(-88.26, -10.6) * mm, "end": v(-89.1, -10.76) * mm});
            skLineSegment(sketch, "E782", {"start": v(-89.1, -10.76) * mm, "end": v(-89.95, -10.92) * mm});
            skLineSegment(sketch, "E783", {"start": v(-89.95, -10.92) * mm, "end": v(-90.85, -11.08) * mm});
            skLineSegment(sketch, "E784", {"start": v(-90.85, -11.08) * mm, "end": v(-91.77, -11.23) * mm});
            skLineSegment(sketch, "E785", {"start": v(-91.77, -11.23) * mm, "end": v(-92.73, -11.38) * mm});
            skLineSegment(sketch, "E786", {"start": v(-92.73, -11.38) * mm, "end": v(-93.72, -11.53) * mm});
            skLineSegment(sketch, "E787", {"start": v(-93.72, -11.53) * mm, "end": v(-94.8, -11.7) * mm});
            skLineSegment(sketch, "E788", {"start": v(-94.8, -11.7) * mm, "end": v(-95.82, -11.87) * mm});
            skLineSegment(sketch, "E789", {"start": v(-95.82, -11.87) * mm, "end": v(-96.75, -12.04) * mm});
            skLineSegment(sketch, "E790", {"start": v(-96.75, -12.04) * mm, "end": v(-97.6, -12.22) * mm});
            skLineSegment(sketch, "E791", {"start": v(-97.6, -12.22) * mm, "end": v(-98.35, -12.41) * mm});
            skLineSegment(sketch, "E792", {"start": v(-98.35, -12.41) * mm, "end": v(-99.03, -12.6) * mm});
            skLineSegment(sketch, "E793", {"start": v(-99.03, -12.6) * mm, "end": v(-99.63, -12.8) * mm});
            skLineSegment(sketch, "E794", {"start": v(-99.63, -12.8) * mm, "end": v(-100.14, -13) * mm});
            skLineSegment(sketch, "E795", {"start": v(-100.14, -13) * mm, "end": v(-100.6, -13.22) * mm});
            skLineSegment(sketch, "E796", {"start": v(-100.6, -13.22) * mm, "end": v(-101.03, -13.46) * mm});
            skLineSegment(sketch, "E797", {"start": v(-101.03, -13.46) * mm, "end": v(-101.43, -13.72) * mm});
            skLineSegment(sketch, "E798", {"start": v(-101.43, -13.72) * mm, "end": v(-101.8, -14) * mm});
            skLineSegment(sketch, "E799", {"start": v(-101.8, -14) * mm, "end": v(-102.16, -14.32) * mm});
            skLineSegment(sketch, "E800", {"start": v(-102.16, -14.32) * mm, "end": v(-102.48, -14.66) * mm});
            skLineSegment(sketch, "E801", {"start": v(-102.48, -14.66) * mm, "end": v(-102.78, -15.01) * mm});
            skLineSegment(sketch, "E802", {"start": v(-102.78, -15.01) * mm, "end": v(-103.05, -15.4) * mm});
            skLineSegment(sketch, "E803", {"start": v(-103.05, -15.4) * mm, "end": v(-103.29, -15.8) * mm});
            skLineSegment(sketch, "E804", {"start": v(-103.29, -15.8) * mm, "end": v(-103.5, -16.2) * mm});
            skLineSegment(sketch, "E805", {"start": v(-103.5, -16.2) * mm, "end": v(-103.67, -16.63) * mm});
            skLineSegment(sketch, "E806", {"start": v(-103.67, -16.63) * mm, "end": v(-103.81, -17.06) * mm});
            skLineSegment(sketch, "E807", {"start": v(-103.81, -17.06) * mm, "end": v(-103.93, -17.5) * mm});
            skLineSegment(sketch, "E808", {"start": v(-103.93, -17.5) * mm, "end": v(-104, -17.96) * mm});
            skLineSegment(sketch, "E809", {"start": v(-104, -17.96) * mm, "end": v(-104.05, -18.42) * mm});
            skLineSegment(sketch, "E810", {"start": v(-104.05, -18.42) * mm, "end": v(-104.07, -18.9) * mm});
            skLineSegment(sketch, "E811", {"start": v(-104.07, -18.9) * mm, "end": v(-104.03, -19.62) * mm});
            skLineSegment(sketch, "E812", {"start": v(-104.03, -19.62) * mm, "end": v(-103.93, -20.3) * mm});
            skLineSegment(sketch, "E813", {"start": v(-103.93, -20.3) * mm, "end": v(-103.76, -20.97) * mm});
            skLineSegment(sketch, "E814", {"start": v(-103.76, -20.97) * mm, "end": v(-103.51, -21.6) * mm});
            skLineSegment(sketch, "E815", {"start": v(-103.51, -21.6) * mm, "end": v(-103.2, -22.2) * mm});
            skLineSegment(sketch, "E816", {"start": v(-103.2, -22.2) * mm, "end": v(-102.82, -22.76) * mm});
            skLineSegment(sketch, "E817", {"start": v(-102.82, -22.76) * mm, "end": v(-102.36, -23.3) * mm});
            skLineSegment(sketch, "E818", {"start": v(-102.36, -23.3) * mm, "end": v(-101.84, -23.8) * mm});
            skLineSegment(sketch, "E819", {"start": v(-101.84, -23.8) * mm, "end": v(-101.25, -24.27) * mm});
            skLineSegment(sketch, "E820", {"start": v(-101.25, -24.27) * mm, "end": v(-100.6, -24.67) * mm});
            skLineSegment(sketch, "E821", {"start": v(-100.6, -24.67) * mm, "end": v(-99.88, -25) * mm});
            skLineSegment(sketch, "E822", {"start": v(-99.88, -25) * mm, "end": v(-99.1, -25.28) * mm});
            skLineSegment(sketch, "E823", {"start": v(-99.1, -25.28) * mm, "end": v(-98.24, -25.5) * mm});
            skLineSegment(sketch, "E824", {"start": v(-98.24, -25.5) * mm, "end": v(-97.33, -25.65) * mm});
            skLineSegment(sketch, "E825", {"start": v(-97.33, -25.65) * mm, "end": v(-96.35, -25.74) * mm});
            skLineSegment(sketch, "E826", {"start": v(-96.35, -25.74) * mm, "end": v(-95.31, -25.77) * mm});
            skLineSegment(sketch, "E827", {"start": v(-95.31, -25.77) * mm, "end": v(-94.26, -25.74) * mm});
            skLineSegment(sketch, "E828", {"start": v(-94.26, -25.74) * mm, "end": v(-93.24, -25.66) * mm});
            skLineSegment(sketch, "E829", {"start": v(-93.24, -25.66) * mm, "end": v(-92.25, -25.5) * mm});
            skLineSegment(sketch, "E830", {"start": v(-92.25, -25.5) * mm, "end": v(-91.3, -25.3) * mm});
            skLineSegment(sketch, "E831", {"start": v(-91.3, -25.3) * mm, "end": v(-90.36, -25.04) * mm});
            skLineSegment(sketch, "E832", {"start": v(-90.36, -25.04) * mm, "end": v(-89.46, -24.72) * mm});
            skLineSegment(sketch, "E833", {"start": v(-89.46, -24.72) * mm, "end": v(-88.58, -24.35) * mm});
            skLineSegment(sketch, "E834", {"start": v(-88.58, -24.35) * mm, "end": v(-87.74, -23.9) * mm});
            skLineSegment(sketch, "E835", {"start": v(-87.74, -23.9) * mm, "end": v(-86.94, -23.42) * mm});
            skLineSegment(sketch, "E836", {"start": v(-86.94, -23.42) * mm, "end": v(-86.2, -22.9) * mm});
            skLineSegment(sketch, "E837", {"start": v(-86.2, -22.9) * mm, "end": v(-85.5, -22.32) * mm});
            skLineSegment(sketch, "E838", {"start": v(-85.5, -22.32) * mm, "end": v(-84.86, -21.7) * mm});
            skLineSegment(sketch, "E839", {"start": v(-84.86, -21.7) * mm, "end": v(-84.28, -21.05) * mm});
            skLineSegment(sketch, "E840", {"start": v(-84.28, -21.05) * mm, "end": v(-83.76, -20.34) * mm});
            skLineSegment(sketch, "E841", {"start": v(-83.76, -20.34) * mm, "end": v(-83.29, -19.6) * mm});
            skLineSegment(sketch, "E842", {"start": v(-83.29, -19.6) * mm, "end": v(-82.87, -18.81) * mm});
            skLineSegment(sketch, "E843", {"start": v(-82.87, -18.81) * mm, "end": v(-82.6, -18.15) * mm});
            skLineSegment(sketch, "E844", {"start": v(-82.6, -18.15) * mm, "end": v(-82.35, -17.42) * mm});
            skLineSegment(sketch, "E845", {"start": v(-82.35, -17.42) * mm, "end": v(-82.15, -16.6) * mm});
            skLineSegment(sketch, "E846", {"start": v(-82.15, -16.6) * mm, "end": v(-81.98, -15.72) * mm});
            skLineSegment(sketch, "E847", {"start": v(-81.98, -15.72) * mm, "end": v(-81.85, -14.77) * mm});
            skLineSegment(sketch, "E848", {"start": v(-81.85, -14.77) * mm, "end": v(-81.76, -13.73) * mm});
            skLineSegment(sketch, "E849", {"start": v(-81.76, -13.73) * mm, "end": v(-81.7, -12.63) * mm});
            skLineSegment(sketch, "E850", {"start": v(-81.7, -12.63) * mm, "end": v(-81.68, -11.45) * mm});
            skLineSegment(sketch, "E851", {"start": v(-81.68, -11.45) * mm, "end": v(-81.68, -8.75) * mm});
            skLineSegment(sketch, "E852", {"start": v(-81.68, -8.75) * mm, "end": v(-81.67, -2.61) * mm});
            skLineSegment(sketch, "E853", {"start": v(-81.67, -2.61) * mm, "end": v(-81.66, -2.29) * mm});
            skLineSegment(sketch, "E854", {"start": v(-81.66, -2.29) * mm, "end": v(-81.66, -2) * mm});
            skLineSegment(sketch, "E855", {"start": v(-81.66, -2) * mm, "end": v(-81.65, -1.74) * mm});
            skLineSegment(sketch, "E856", {"start": v(-81.65, -1.74) * mm, "end": v(-81.65, -1.51) * mm});
            skLineSegment(sketch, "E857", {"start": v(-81.65, -1.51) * mm, "end": v(-81.64, -1.32) * mm});
            skLineSegment(sketch, "E858", {"start": v(-81.64, -1.32) * mm, "end": v(-81.64, -1.17) * mm});
            skLineSegment(sketch, "E859", {"start": v(-81.64, -1.17) * mm, "end": v(-81.64, -1.05) * mm});
            skLineSegment(sketch, "E860", {"start": v(-81.64, -1.05) * mm, "end": v(-81.65, -0.5) * mm});
            skLineSegment(sketch, "E861", {"start": v(-81.65, -0.5) * mm, "end": v(-81.67, 0.03) * mm});
            skLineSegment(sketch, "E862", {"start": v(-81.67, 0.03) * mm, "end": v(-81.71, 0.54) * mm});
            skLineSegment(sketch, "E863", {"start": v(-81.71, 0.54) * mm, "end": v(-81.77, 1.03) * mm});
            skLineSegment(sketch, "E864", {"start": v(-81.77, 1.03) * mm, "end": v(-81.85, 1.5) * mm});
            skLineSegment(sketch, "E865", {"start": v(-81.85, 1.5) * mm, "end": v(-81.93, 1.95) * mm});
            skLineSegment(sketch, "E866", {"start": v(-81.93, 1.95) * mm, "end": v(-82.04, 2.38) * mm});
            skLineSegment(sketch, "E867", {"start": v(-82.04, 2.38) * mm, "end": v(-82.16, 2.79) * mm});
            skLineSegment(sketch, "E868", {"start": v(-82.16, 2.79) * mm, "end": v(-82.3, 3.17) * mm});
            skLineSegment(sketch, "E869", {"start": v(-82.3, 3.17) * mm, "end": v(-82.46, 3.54) * mm});
            skLineSegment(sketch, "E870", {"start": v(-82.46, 3.54) * mm, "end": v(-82.63, 3.88) * mm});
            skLineSegment(sketch, "E871", {"start": v(-82.63, 3.88) * mm, "end": v(-82.82, 4.2) * mm});
            skLineSegment(sketch, "E872", {"start": v(-82.82, 4.2) * mm, "end": v(-83.02, 4.5) * mm});
            skLineSegment(sketch, "E873", {"start": v(-83.02, 4.5) * mm, "end": v(-83.24, 4.8) * mm});
            skLineSegment(sketch, "E874", {"start": v(-83.24, 4.8) * mm, "end": v(-83.48, 5.05) * mm});
            skLineSegment(sketch, "E875", {"start": v(-83.48, 5.05) * mm, "end": v(-83.73, 5.3) * mm});
            skLineSegment(sketch, "E876", {"start": v(-83.73, 5.3) * mm, "end": v(-84.1, 5.6) * mm});
            skLineSegment(sketch, "E877", {"start": v(-84.1, 5.6) * mm, "end": v(-84.48, 5.88) * mm});
            skLineSegment(sketch, "E878", {"start": v(-84.48, 5.88) * mm, "end": v(-84.88, 6.14) * mm});
            skLineSegment(sketch, "E879", {"start": v(-84.88, 6.14) * mm, "end": v(-85.31, 6.38) * mm});
            skLineSegment(sketch, "E880", {"start": v(-85.31, 6.38) * mm, "end": v(-85.76, 6.6) * mm});
            skLineSegment(sketch, "E881", {"start": v(-85.76, 6.6) * mm, "end": v(-86.23, 6.81) * mm});
            skLineSegment(sketch, "E882", {"start": v(-86.23, 6.81) * mm, "end": v(-86.72, 7) * mm});
            skLineSegment(sketch, "E883", {"start": v(-86.72, 7) * mm, "end": v(-87.24, 7.17) * mm});
            skLineSegment(sketch, "E884", {"start": v(-87.24, 7.17) * mm, "end": v(-87.77, 7.31) * mm});
            skLineSegment(sketch, "E885", {"start": v(-87.77, 7.31) * mm, "end": v(-88.33, 7.44) * mm});
            skLineSegment(sketch, "E886", {"start": v(-88.33, 7.44) * mm, "end": v(-88.9, 7.55) * mm});
            skLineSegment(sketch, "E887", {"start": v(-88.9, 7.55) * mm, "end": v(-89.5, 7.63) * mm});
            skLineSegment(sketch, "E888", {"start": v(-89.5, 7.63) * mm, "end": v(-90.13, 7.7) * mm});
            skLineSegment(sketch, "E889", {"start": v(-90.13, 7.7) * mm, "end": v(-90.77, 7.75) * mm});
            skLineSegment(sketch, "E890", {"start": v(-90.77, 7.75) * mm, "end": v(-91.43, 7.78) * mm});
            skLineSegment(sketch, "E891", {"start": v(-91.43, 7.78) * mm, "end": v(-92.12, 7.79) * mm});
            skLineSegment(sketch, "E892", {"start": v(-92.12, 7.79) * mm, "end": v(-92.76, 7.78) * mm});
            skLineSegment(sketch, "E893", {"start": v(-92.76, 7.78) * mm, "end": v(-93.38, 7.76) * mm});
            skLineSegment(sketch, "E894", {"start": v(-93.38, 7.76) * mm, "end": v(-93.97, 7.73) * mm});
            skLineSegment(sketch, "E895", {"start": v(-93.97, 7.73) * mm, "end": v(-94.55, 7.68) * mm});
            skLineSegment(sketch, "E896", {"start": v(-94.55, 7.68) * mm, "end": v(-95.1, 7.61) * mm});
            skLineSegment(sketch, "E897", {"start": v(-95.1, 7.61) * mm, "end": v(-95.63, 7.53) * mm});
            skLineSegment(sketch, "E898", {"start": v(-95.63, 7.53) * mm, "end": v(-96.15, 7.44) * mm});
            skLineSegment(sketch, "E899", {"start": v(-96.15, 7.44) * mm, "end": v(-96.64, 7.33) * mm});
            skLineSegment(sketch, "E900", {"start": v(-96.64, 7.33) * mm, "end": v(-97.1, 7.21) * mm});
            skLineSegment(sketch, "E901", {"start": v(-97.1, 7.21) * mm, "end": v(-97.55, 7.08) * mm});
            skLineSegment(sketch, "E902", {"start": v(-97.55, 7.08) * mm, "end": v(-97.98, 6.93) * mm});
            skLineSegment(sketch, "E903", {"start": v(232.36, -24.04) * mm, "end": v(232.85, -23.97) * mm});
            skLineSegment(sketch, "E904", {"start": v(232.85, -23.97) * mm, "end": v(233.91, -30.48) * mm});
            skLineSegment(sketch, "E905", {"start": v(233.91, -30.48) * mm, "end": v(233.14, -30.63) * mm});
            skLineSegment(sketch, "E906", {"start": v(233.14, -30.63) * mm, "end": v(232.4, -30.76) * mm});
            skLineSegment(sketch, "E907", {"start": v(232.4, -30.76) * mm, "end": v(231.67, -30.88) * mm});
            skLineSegment(sketch, "E908", {"start": v(231.67, -30.88) * mm, "end": v(230.96, -30.97) * mm});
            skLineSegment(sketch, "E909", {"start": v(230.96, -30.97) * mm, "end": v(230.28, -31.04) * mm});
            skLineSegment(sketch, "E910", {"start": v(230.28, -31.04) * mm, "end": v(229.61, -31.1) * mm});
            skLineSegment(sketch, "E911", {"start": v(229.61, -31.1) * mm, "end": v(228.97, -31.12) * mm});
            skLineSegment(sketch, "E912", {"start": v(228.97, -31.12) * mm, "end": v(228.34, -31.13) * mm});
            skLineSegment(sketch, "E913", {"start": v(228.34, -31.13) * mm, "end": v(227.37, -31.11) * mm});
            skLineSegment(sketch, "E914", {"start": v(227.37, -31.11) * mm, "end": v(226.45, -31.05) * mm});
            skLineSegment(sketch, "E915", {"start": v(226.45, -31.05) * mm, "end": v(225.6, -30.95) * mm});
            skLineSegment(sketch, "E916", {"start": v(225.6, -30.95) * mm, "end": v(224.78, -30.82) * mm});
            skLineSegment(sketch, "E917", {"start": v(224.78, -30.82) * mm, "end": v(224.03, -30.64) * mm});
            skLineSegment(sketch, "E918", {"start": v(224.03, -30.64) * mm, "end": v(223.34, -30.42) * mm});
            skLineSegment(sketch, "E919", {"start": v(223.34, -30.42) * mm, "end": v(222.7, -30.16) * mm});
            skLineSegment(sketch, "E920", {"start": v(222.7, -30.16) * mm, "end": v(222.12, -29.86) * mm});
            skLineSegment(sketch, "E921", {"start": v(222.12, -29.86) * mm, "end": v(221.6, -29.53) * mm});
            skLineSegment(sketch, "E922", {"start": v(221.6, -29.53) * mm, "end": v(221.1, -29.18) * mm});
            skLineSegment(sketch, "E923", {"start": v(221.1, -29.18) * mm, "end": v(220.65, -28.8) * mm});
            skLineSegment(sketch, "E924", {"start": v(220.65, -28.8) * mm, "end": v(220.24, -28.4) * mm});
            skLineSegment(sketch, "E925", {"start": v(220.24, -28.4) * mm, "end": v(219.87, -27.97) * mm});
            skLineSegment(sketch, "E926", {"start": v(219.87, -27.97) * mm, "end": v(219.55, -27.51) * mm});
            skLineSegment(sketch, "E927", {"start": v(219.55, -27.51) * mm, "end": v(219.26, -27.03) * mm});
            skLineSegment(sketch, "E928", {"start": v(219.26, -27.03) * mm, "end": v(219.01, -26.53) * mm});
            skLineSegment(sketch, "E929", {"start": v(219.01, -26.53) * mm, "end": v(218.9, -26.25) * mm});
            skLineSegment(sketch, "E930", {"start": v(218.9, -26.25) * mm, "end": v(218.8, -25.94) * mm});
            skLineSegment(sketch, "E931", {"start": v(218.8, -25.94) * mm, "end": v(218.7, -25.6) * mm});
            skLineSegment(sketch, "E932", {"start": v(218.7, -25.6) * mm, "end": v(218.62, -25.2) * mm});
            skLineSegment(sketch, "E933", {"start": v(218.62, -25.2) * mm, "end": v(218.54, -24.8) * mm});
            skLineSegment(sketch, "E934", {"start": v(218.54, -24.8) * mm, "end": v(218.46, -24.34) * mm});
            skLineSegment(sketch, "E935", {"start": v(218.46, -24.34) * mm, "end": v(218.4, -23.85) * mm});
            skLineSegment(sketch, "E936", {"start": v(218.4, -23.85) * mm, "end": v(218.34, -23.32) * mm});
            skLineSegment(sketch, "E937", {"start": v(218.34, -23.32) * mm, "end": v(218.29, -22.76) * mm});
            skLineSegment(sketch, "E938", {"start": v(218.29, -22.76) * mm, "end": v(218.24, -22.16) * mm});
            skLineSegment(sketch, "E939", {"start": v(218.24, -22.16) * mm, "end": v(218.2, -21.53) * mm});
            skLineSegment(sketch, "E940", {"start": v(218.2, -21.53) * mm, "end": v(218.17, -20.86) * mm});
            skLineSegment(sketch, "E941", {"start": v(218.17, -20.86) * mm, "end": v(218.14, -20.16) * mm});
            skLineSegment(sketch, "E942", {"start": v(218.14, -20.16) * mm, "end": v(218.13, -19.42) * mm});
            skLineSegment(sketch, "E943", {"start": v(218.13, -19.42) * mm, "end": v(218.12, -18.64) * mm});
            skLineSegment(sketch, "E944", {"start": v(218.12, -18.64) * mm, "end": v(218.11, -17.83) * mm});
            skLineSegment(sketch, "E945", {"start": v(218.11, -17.83) * mm, "end": v(218.11, 7.18) * mm});
            skLineSegment(sketch, "E946", {"start": v(218.11, 7.18) * mm, "end": v(212.71, 7.18) * mm});
            skLineSegment(sketch, "E947", {"start": v(212.71, 7.18) * mm, "end": v(212.71, 12.9) * mm});
            skLineSegment(sketch, "E948", {"start": v(212.71, 12.9) * mm, "end": v(218.11, 12.9) * mm});
            skLineSegment(sketch, "E949", {"start": v(218.11, 12.9) * mm, "end": v(218.11, 23.67) * mm});
            skLineSegment(sketch, "E950", {"start": v(218.11, 23.67) * mm, "end": v(225.44, 28.09) * mm});
            skLineSegment(sketch, "E951", {"start": v(225.44, 28.09) * mm, "end": v(225.44, 12.9) * mm});
            skLineSegment(sketch, "E952", {"start": v(225.44, 12.9) * mm, "end": v(232.85, 12.9) * mm});
            skLineSegment(sketch, "E953", {"start": v(232.85, 12.9) * mm, "end": v(232.85, 7.18) * mm});
            skLineSegment(sketch, "E954", {"start": v(232.85, 7.18) * mm, "end": v(225.44, 7.18) * mm});
            skLineSegment(sketch, "E955", {"start": v(225.44, 7.18) * mm, "end": v(225.44, -18.24) * mm});
            skLineSegment(sketch, "E956", {"start": v(225.44, -18.24) * mm, "end": v(225.45, -19) * mm});
            skLineSegment(sketch, "E957", {"start": v(225.45, -19) * mm, "end": v(225.46, -19.68) * mm});
            skLineSegment(sketch, "E958", {"start": v(225.46, -19.68) * mm, "end": v(225.5, -20.29) * mm});
            skLineSegment(sketch, "E959", {"start": v(225.5, -20.29) * mm, "end": v(225.54, -20.83) * mm});
            skLineSegment(sketch, "E960", {"start": v(225.54, -20.83) * mm, "end": v(225.6, -21.3) * mm});
            skLineSegment(sketch, "E961", {"start": v(225.6, -21.3) * mm, "end": v(225.66, -21.7) * mm});
            skLineSegment(sketch, "E962", {"start": v(225.66, -21.7) * mm, "end": v(225.74, -22.03) * mm});
            skLineSegment(sketch, "E963", {"start": v(225.74, -22.03) * mm, "end": v(225.83, -22.3) * mm});
            skLineSegment(sketch, "E964", {"start": v(225.83, -22.3) * mm, "end": v(226.05, -22.72) * mm});
            skLineSegment(sketch, "E965", {"start": v(226.05, -22.72) * mm, "end": v(226.34, -23.1) * mm});
            skLineSegment(sketch, "E966", {"start": v(226.34, -23.1) * mm, "end": v(226.69, -23.44) * mm});
            skLineSegment(sketch, "E967", {"start": v(226.69, -23.44) * mm, "end": v(227.1, -23.73) * mm});
            skLineSegment(sketch, "E968", {"start": v(227.1, -23.73) * mm, "end": v(227.33, -23.85) * mm});
            skLineSegment(sketch, "E969", {"start": v(227.33, -23.85) * mm, "end": v(227.58, -23.96) * mm});
            skLineSegment(sketch, "E970", {"start": v(227.58, -23.96) * mm, "end": v(227.86, -24.05) * mm});
            skLineSegment(sketch, "E971", {"start": v(227.86, -24.05) * mm, "end": v(228.17, -24.12) * mm});
            skLineSegment(sketch, "E972", {"start": v(228.17, -24.12) * mm, "end": v(228.5, -24.18) * mm});
            skLineSegment(sketch, "E973", {"start": v(228.5, -24.18) * mm, "end": v(228.84, -24.22) * mm});
            skLineSegment(sketch, "E974", {"start": v(228.84, -24.22) * mm, "end": v(229.22, -24.25) * mm});
            skLineSegment(sketch, "E975", {"start": v(229.22, -24.25) * mm, "end": v(229.61, -24.26) * mm});
            skLineSegment(sketch, "E976", {"start": v(229.61, -24.26) * mm, "end": v(229.93, -24.25) * mm});
            skLineSegment(sketch, "E977", {"start": v(229.93, -24.25) * mm, "end": v(230.28, -24.24) * mm});
            skLineSegment(sketch, "E978", {"start": v(230.28, -24.24) * mm, "end": v(230.64, -24.22) * mm});
            skLineSegment(sketch, "E979", {"start": v(230.64, -24.22) * mm, "end": v(231.04, -24.19) * mm});
            skLineSegment(sketch, "E980", {"start": v(231.04, -24.19) * mm, "end": v(231.45, -24.15) * mm});
            skLineSegment(sketch, "E981", {"start": v(231.45, -24.15) * mm, "end": v(231.9, -24.1) * mm});
            skLineSegment(sketch, "E982", {"start": v(231.9, -24.1) * mm, "end": v(232.36, -24.04) * mm});
            skLineSegment(sketch, "E983", {"start": v(159.13, -12.03) * mm, "end": v(159.1, -11.28) * mm});
            skLineSegment(sketch, "E984", {"start": v(159.1, -11.28) * mm, "end": v(166.59, -10.63) * mm});
            skLineSegment(sketch, "E985", {"start": v(166.59, -10.63) * mm, "end": v(166.74, -11.73) * mm});
            skLineSegment(sketch, "E986", {"start": v(166.74, -11.73) * mm, "end": v(166.94, -12.78) * mm});
            skLineSegment(sketch, "E987", {"start": v(166.94, -12.78) * mm, "end": v(167.18, -13.78) * mm});
            skLineSegment(sketch, "E988", {"start": v(167.18, -13.78) * mm, "end": v(167.47, -14.73) * mm});
            skLineSegment(sketch, "E989", {"start": v(167.47, -14.73) * mm, "end": v(167.8, -15.62) * mm});
            skLineSegment(sketch, "E990", {"start": v(167.8, -15.62) * mm, "end": v(168.18, -16.47) * mm});
            skLineSegment(sketch, "E991", {"start": v(168.18, -16.47) * mm, "end": v(168.6, -17.27) * mm});
            skLineSegment(sketch, "E992", {"start": v(168.6, -17.27) * mm, "end": v(169.06, -18.02) * mm});
            skLineSegment(sketch, "E993", {"start": v(169.06, -18.02) * mm, "end": v(169.58, -18.72) * mm});
            skLineSegment(sketch, "E994", {"start": v(169.58, -18.72) * mm, "end": v(170.17, -19.39) * mm});
            skLineSegment(sketch, "E995", {"start": v(170.17, -19.39) * mm, "end": v(170.82, -20.02) * mm});
            skLineSegment(sketch, "E996", {"start": v(170.82, -20.02) * mm, "end": v(171.54, -20.62) * mm});
            skLineSegment(sketch, "E997", {"start": v(171.54, -20.62) * mm, "end": v(172.33, -21.2) * mm});
            skLineSegment(sketch, "E998", {"start": v(172.33, -21.2) * mm, "end": v(173.19, -21.72) * mm});
            skLineSegment(sketch, "E999", {"start": v(173.19, -21.72) * mm, "end": v(174.1, -22.22) * mm});
            skLineSegment(sketch, "E1000", {"start": v(174.1, -22.22) * mm, "end": v(175.1, -22.68) * mm});
            skLineSegment(sketch, "E1001", {"start": v(175.1, -22.68) * mm, "end": v(176.14, -23.1) * mm});
            skLineSegment(sketch, "E1002", {"start": v(176.14, -23.1) * mm, "end": v(177.2, -23.46) * mm});
            skLineSegment(sketch, "E1003", {"start": v(177.2, -23.46) * mm, "end": v(178.31, -23.77) * mm});
            skLineSegment(sketch, "E1004", {"start": v(178.31, -23.77) * mm, "end": v(179.45, -24.02) * mm});
            skLineSegment(sketch, "E1005", {"start": v(179.45, -24.02) * mm, "end": v(180.61, -24.21) * mm});
            skLineSegment(sketch, "E1006", {"start": v(180.61, -24.21) * mm, "end": v(181.81, -24.35) * mm});
            skLineSegment(sketch, "E1007", {"start": v(181.81, -24.35) * mm, "end": v(183.04, -24.43) * mm});
            skLineSegment(sketch, "E1008", {"start": v(183.04, -24.43) * mm, "end": v(184.3, -24.46) * mm});
            skLineSegment(sketch, "E1009", {"start": v(184.3, -24.46) * mm, "end": v(185.43, -24.44) * mm});
            skLineSegment(sketch, "E1010", {"start": v(185.43, -24.44) * mm, "end": v(186.51, -24.38) * mm});
            skLineSegment(sketch, "E1011", {"start": v(186.51, -24.38) * mm, "end": v(187.56, -24.27) * mm});
            skLineSegment(sketch, "E1012", {"start": v(187.56, -24.27) * mm, "end": v(188.58, -24.12) * mm});
            skLineSegment(sketch, "E1013", {"start": v(188.58, -24.12) * mm, "end": v(189.57, -23.93) * mm});
            skLineSegment(sketch, "E1014", {"start": v(189.57, -23.93) * mm, "end": v(190.52, -23.7) * mm});
            skLineSegment(sketch, "E1015", {"start": v(190.52, -23.7) * mm, "end": v(191.44, -23.43) * mm});
            skLineSegment(sketch, "E1016", {"start": v(191.44, -23.43) * mm, "end": v(192.33, -23.11) * mm});
            skLineSegment(sketch, "E1017", {"start": v(192.33, -23.11) * mm, "end": v(193.17, -22.76) * mm});
            skLineSegment(sketch, "E1018", {"start": v(193.17, -22.76) * mm, "end": v(193.96, -22.37) * mm});
            skLineSegment(sketch, "E1019", {"start": v(193.96, -22.37) * mm, "end": v(194.69, -21.96) * mm});
            skLineSegment(sketch, "E1020", {"start": v(194.69, -21.96) * mm, "end": v(195.36, -21.5) * mm});
            skLineSegment(sketch, "E1021", {"start": v(195.36, -21.5) * mm, "end": v(195.98, -21.03) * mm});
            skLineSegment(sketch, "E1022", {"start": v(195.98, -21.03) * mm, "end": v(196.55, -20.52) * mm});
            skLineSegment(sketch, "E1023", {"start": v(196.55, -20.52) * mm, "end": v(197.05, -19.98) * mm});
            skLineSegment(sketch, "E1024", {"start": v(197.05, -19.98) * mm, "end": v(197.5, -19.4) * mm});
            skLineSegment(sketch, "E1025", {"start": v(197.5, -19.4) * mm, "end": v(197.9, -18.81) * mm});
            skLineSegment(sketch, "E1026", {"start": v(197.9, -18.81) * mm, "end": v(198.25, -18.2) * mm});
            skLineSegment(sketch, "E1027", {"start": v(198.25, -18.2) * mm, "end": v(198.54, -17.58) * mm});
            skLineSegment(sketch, "E1028", {"start": v(198.54, -17.58) * mm, "end": v(198.78, -16.95) * mm});
            skLineSegment(sketch, "E1029", {"start": v(198.78, -16.95) * mm, "end": v(198.97, -16.3) * mm});
            skLineSegment(sketch, "E1030", {"start": v(198.97, -16.3) * mm, "end": v(199.1, -15.64) * mm});
            skLineSegment(sketch, "E1031", {"start": v(199.1, -15.64) * mm, "end": v(199.18, -14.96) * mm});
            skLineSegment(sketch, "E1032", {"start": v(199.18, -14.96) * mm, "end": v(199.2, -14.27) * mm});
            skLineSegment(sketch, "E1033", {"start": v(199.2, -14.27) * mm, "end": v(199.18, -13.58) * mm});
            skLineSegment(sketch, "E1034", {"start": v(199.18, -13.58) * mm, "end": v(199.1, -12.9) * mm});
            skLineSegment(sketch, "E1035", {"start": v(199.1, -12.9) * mm, "end": v(198.97, -12.25) * mm});
            skLineSegment(sketch, "E1036", {"start": v(198.97, -12.25) * mm, "end": v(198.8, -11.63) * mm});
            skLineSegment(sketch, "E1037", {"start": v(198.8, -11.63) * mm, "end": v(198.56, -11.02) * mm});
            skLineSegment(sketch, "E1038", {"start": v(198.56, -11.02) * mm, "end": v(198.28, -10.44) * mm});
            skLineSegment(sketch, "E1039", {"start": v(198.28, -10.44) * mm, "end": v(197.95, -9.88) * mm});
            skLineSegment(sketch, "E1040", {"start": v(197.95, -9.88) * mm, "end": v(197.57, -9.34) * mm});
            skLineSegment(sketch, "E1041", {"start": v(197.57, -9.34) * mm, "end": v(197.12, -8.82) * mm});
            skLineSegment(sketch, "E1042", {"start": v(197.12, -8.82) * mm, "end": v(196.62, -8.33) * mm});
            skLineSegment(sketch, "E1043", {"start": v(196.62, -8.33) * mm, "end": v(196.04, -7.85) * mm});
            skLineSegment(sketch, "E1044", {"start": v(196.04, -7.85) * mm, "end": v(195.4, -7.4) * mm});
            skLineSegment(sketch, "E1045", {"start": v(195.4, -7.4) * mm, "end": v(194.69, -6.97) * mm});
            skLineSegment(sketch, "E1046", {"start": v(194.69, -6.97) * mm, "end": v(193.91, -6.56) * mm});
            skLineSegment(sketch, "E1047", {"start": v(193.91, -6.56) * mm, "end": v(193.07, -6.17) * mm});
            skLineSegment(sketch, "E1048", {"start": v(193.07, -6.17) * mm, "end": v(192.16, -5.8) * mm});
            skLineSegment(sketch, "E1049", {"start": v(192.16, -5.8) * mm, "end": v(191.84, -5.68) * mm});
            skLineSegment(sketch, "E1050", {"start": v(191.84, -5.68) * mm, "end": v(191.47, -5.55) * mm});
            skLineSegment(sketch, "E1051", {"start": v(191.47, -5.55) * mm, "end": v(191.05, -5.4) * mm});
            skLineSegment(sketch, "E1052", {"start": v(191.05, -5.4) * mm, "end": v(190.6, -5.26) * mm});
            skLineSegment(sketch, "E1053", {"start": v(190.6, -5.26) * mm, "end": v(190.08, -5.1) * mm});
            skLineSegment(sketch, "E1054", {"start": v(190.08, -5.1) * mm, "end": v(189.53, -4.95) * mm});
            skLineSegment(sketch, "E1055", {"start": v(189.53, -4.95) * mm, "end": v(188.93, -4.78) * mm});
            skLineSegment(sketch, "E1056", {"start": v(188.93, -4.78) * mm, "end": v(188.29, -4.6) * mm});
            skLineSegment(sketch, "E1057", {"start": v(188.29, -4.6) * mm, "end": v(187.6, -4.4) * mm});
            skLineSegment(sketch, "E1058", {"start": v(187.6, -4.4) * mm, "end": v(186.86, -4.21) * mm});
            skLineSegment(sketch, "E1059", {"start": v(186.86, -4.21) * mm, "end": v(186.08, -4.01) * mm});
            skLineSegment(sketch, "E1060", {"start": v(186.08, -4.01) * mm, "end": v(185.25, -3.8) * mm});
            skLineSegment(sketch, "E1061", {"start": v(185.25, -3.8) * mm, "end": v(184.38, -3.58) * mm});
            skLineSegment(sketch, "E1062", {"start": v(184.38, -3.58) * mm, "end": v(183.46, -3.35) * mm});
            skLineSegment(sketch, "E1063", {"start": v(183.46, -3.35) * mm, "end": v(182.5, -3.12) * mm});
            skLineSegment(sketch, "E1064", {"start": v(182.5, -3.12) * mm, "end": v(181.48, -2.87) * mm});
            skLineSegment(sketch, "E1065", {"start": v(181.48, -2.87) * mm, "end": v(180.47, -2.63) * mm});
            skLineSegment(sketch, "E1066", {"start": v(180.47, -2.63) * mm, "end": v(179.5, -2.38) * mm});
            skLineSegment(sketch, "E1067", {"start": v(179.5, -2.38) * mm, "end": v(178.56, -2.14) * mm});
            skLineSegment(sketch, "E1068", {"start": v(178.56, -2.14) * mm, "end": v(177.66, -1.9) * mm});
            skLineSegment(sketch, "E1069", {"start": v(177.66, -1.9) * mm, "end": v(176.8, -1.65) * mm});
            skLineSegment(sketch, "E1070", {"start": v(176.8, -1.65) * mm, "end": v(175.98, -1.42) * mm});
            skLineSegment(sketch, "E1071", {"start": v(175.98, -1.42) * mm, "end": v(175.2, -1.18) * mm});
            skLineSegment(sketch, "E1072", {"start": v(175.2, -1.18) * mm, "end": v(174.45, -0.94) * mm});
            skLineSegment(sketch, "E1073", {"start": v(174.45, -0.94) * mm, "end": v(173.75, -0.71) * mm});
            skLineSegment(sketch, "E1074", {"start": v(173.75, -0.71) * mm, "end": v(173.08, -0.48) * mm});
            skLineSegment(sketch, "E1075", {"start": v(173.08, -0.48) * mm, "end": v(172.46, -0.25) * mm});
            skLineSegment(sketch, "E1076", {"start": v(172.46, -0.25) * mm, "end": v(171.87, -0.02) * mm});
            skLineSegment(sketch, "E1077", {"start": v(171.87, -0.02) * mm, "end": v(171.32, 0.2) * mm});
            skLineSegment(sketch, "E1078", {"start": v(171.32, 0.2) * mm, "end": v(170.8, 0.43) * mm});
            skLineSegment(sketch, "E1079", {"start": v(170.8, 0.43) * mm, "end": v(170.33, 0.65) * mm});
            skLineSegment(sketch, "E1080", {"start": v(170.33, 0.65) * mm, "end": v(169.9, 0.87) * mm});
            skLineSegment(sketch, "E1081", {"start": v(169.9, 0.87) * mm, "end": v(168.86, 1.45) * mm});
            skLineSegment(sketch, "E1082", {"start": v(168.86, 1.45) * mm, "end": v(167.89, 2.07) * mm});
            skLineSegment(sketch, "E1083", {"start": v(167.89, 2.07) * mm, "end": v(166.99, 2.71) * mm});
            skLineSegment(sketch, "E1084", {"start": v(166.99, 2.71) * mm, "end": v(166.15, 3.4) * mm});
            skLineSegment(sketch, "E1085", {"start": v(166.15, 3.4) * mm, "end": v(165.38, 4.1) * mm});
            skLineSegment(sketch, "E1086", {"start": v(165.38, 4.1) * mm, "end": v(164.69, 4.86) * mm});
            skLineSegment(sketch, "E1087", {"start": v(164.69, 4.86) * mm, "end": v(164.06, 5.64) * mm});
            skLineSegment(sketch, "E1088", {"start": v(164.06, 5.64) * mm, "end": v(163.5, 6.46) * mm});
            skLineSegment(sketch, "E1089", {"start": v(163.5, 6.46) * mm, "end": v(163, 7.3) * mm});
            skLineSegment(sketch, "E1090", {"start": v(163, 7.3) * mm, "end": v(162.57, 8.18) * mm});
            skLineSegment(sketch, "E1091", {"start": v(162.57, 8.18) * mm, "end": v(162.21, 9.07) * mm});
            skLineSegment(sketch, "E1092", {"start": v(162.21, 9.07) * mm, "end": v(161.91, 10) * mm});
            skLineSegment(sketch, "E1093", {"start": v(161.91, 10) * mm, "end": v(161.68, 10.94) * mm});
            skLineSegment(sketch, "E1094", {"start": v(161.68, 10.94) * mm, "end": v(161.52, 11.91) * mm});
            skLineSegment(sketch, "E1095", {"start": v(161.52, 11.91) * mm, "end": v(161.42, 12.9) * mm});
            skLineSegment(sketch, "E1096", {"start": v(161.42, 12.9) * mm, "end": v(161.39, 13.93) * mm});
            skLineSegment(sketch, "E1097", {"start": v(161.39, 13.93) * mm, "end": v(161.43, 15.05) * mm});
            skLineSegment(sketch, "E1098", {"start": v(161.43, 15.05) * mm, "end": v(161.55, 16.16) * mm});
            skLineSegment(sketch, "E1099", {"start": v(161.55, 16.16) * mm, "end": v(161.75, 17.25) * mm});
            skLineSegment(sketch, "E1100", {"start": v(161.75, 17.25) * mm, "end": v(162.03, 18.32) * mm});
            skLineSegment(sketch, "E1101", {"start": v(162.03, 18.32) * mm, "end": v(162.4, 19.38) * mm});
            skLineSegment(sketch, "E1102", {"start": v(162.4, 19.38) * mm, "end": v(162.84, 20.4) * mm});
            skLineSegment(sketch, "E1103", {"start": v(162.84, 20.4) * mm, "end": v(163.36, 21.42) * mm});
            skLineSegment(sketch, "E1104", {"start": v(163.36, 21.42) * mm, "end": v(163.97, 22.42) * mm});
            skLineSegment(sketch, "E1105", {"start": v(163.97, 22.42) * mm, "end": v(164.65, 23.38) * mm});
            skLineSegment(sketch, "E1106", {"start": v(164.65, 23.38) * mm, "end": v(165.4, 24.28) * mm});
            skLineSegment(sketch, "E1107", {"start": v(165.4, 24.28) * mm, "end": v(166.23, 25.12) * mm});
            skLineSegment(sketch, "E1108", {"start": v(166.23, 25.12) * mm, "end": v(167.14, 25.9) * mm});
            skLineSegment(sketch, "E1109", {"start": v(167.14, 25.9) * mm, "end": v(168.12, 26.61) * mm});
            skLineSegment(sketch, "E1110", {"start": v(168.12, 26.61) * mm, "end": v(169.17, 27.27) * mm});
            skLineSegment(sketch, "E1111", {"start": v(169.17, 27.27) * mm, "end": v(170.3, 27.88) * mm});
            skLineSegment(sketch, "E1112", {"start": v(170.3, 27.88) * mm, "end": v(171.5, 28.42) * mm});
            skLineSegment(sketch, "E1113", {"start": v(171.5, 28.42) * mm, "end": v(172.75, 28.9) * mm});
            skLineSegment(sketch, "E1114", {"start": v(172.75, 28.9) * mm, "end": v(174.04, 29.31) * mm});
            skLineSegment(sketch, "E1115", {"start": v(174.04, 29.31) * mm, "end": v(175.37, 29.66) * mm});
            skLineSegment(sketch, "E1116", {"start": v(175.37, 29.66) * mm, "end": v(176.72, 29.95) * mm});
            skLineSegment(sketch, "E1117", {"start": v(176.72, 29.95) * mm, "end": v(178.12, 30.18) * mm});
            skLineSegment(sketch, "E1118", {"start": v(178.12, 30.18) * mm, "end": v(179.55, 30.34) * mm});
            skLineSegment(sketch, "E1119", {"start": v(179.55, 30.34) * mm, "end": v(181, 30.43) * mm});
            skLineSegment(sketch, "E1120", {"start": v(181, 30.43) * mm, "end": v(182.5, 30.46) * mm});
            skLineSegment(sketch, "E1121", {"start": v(182.5, 30.46) * mm, "end": v(184.15, 30.43) * mm});
            skLineSegment(sketch, "E1122", {"start": v(184.15, 30.43) * mm, "end": v(185.74, 30.33) * mm});
            skLineSegment(sketch, "E1123", {"start": v(185.74, 30.33) * mm, "end": v(187.29, 30.16) * mm});
            skLineSegment(sketch, "E1124", {"start": v(187.29, 30.16) * mm, "end": v(188.78, 29.93) * mm});
            skLineSegment(sketch, "E1125", {"start": v(188.78, 29.93) * mm, "end": v(190.23, 29.62) * mm});
            skLineSegment(sketch, "E1126", {"start": v(190.23, 29.62) * mm, "end": v(191.63, 29.25) * mm});
            skLineSegment(sketch, "E1127", {"start": v(191.63, 29.25) * mm, "end": v(192.97, 28.82) * mm});
            skLineSegment(sketch, "E1128", {"start": v(192.97, 28.82) * mm, "end": v(194.27, 28.31) * mm});
            skLineSegment(sketch, "E1129", {"start": v(194.27, 28.31) * mm, "end": v(194.9, 28.04) * mm});
            skLineSegment(sketch, "E1130", {"start": v(194.9, 28.04) * mm, "end": v(195.5, 27.75) * mm});
            skLineSegment(sketch, "E1131", {"start": v(195.5, 27.75) * mm, "end": v(196.1, 27.44) * mm});
            skLineSegment(sketch, "E1132", {"start": v(196.1, 27.44) * mm, "end": v(196.67, 27.11) * mm});
            skLineSegment(sketch, "E1133", {"start": v(196.67, 27.11) * mm, "end": v(197.23, 26.77) * mm});
            skLineSegment(sketch, "E1134", {"start": v(197.23, 26.77) * mm, "end": v(197.76, 26.42) * mm});
            skLineSegment(sketch, "E1135", {"start": v(197.76, 26.42) * mm, "end": v(198.28, 26.05) * mm});
            skLineSegment(sketch, "E1136", {"start": v(198.28, 26.05) * mm, "end": v(198.78, 25.66) * mm});
            skLineSegment(sketch, "E1137", {"start": v(198.78, 25.66) * mm, "end": v(199.26, 25.26) * mm});
            skLineSegment(sketch, "E1138", {"start": v(199.26, 25.26) * mm, "end": v(199.72, 24.84) * mm});
            skLineSegment(sketch, "E1139", {"start": v(199.72, 24.84) * mm, "end": v(200.17, 24.4) * mm});
            skLineSegment(sketch, "E1140", {"start": v(200.17, 24.4) * mm, "end": v(200.6, 23.95) * mm});
            skLineSegment(sketch, "E1141", {"start": v(200.6, 23.95) * mm, "end": v(201, 23.49) * mm});
            skLineSegment(sketch, "E1142", {"start": v(201, 23.49) * mm, "end": v(201.39, 23) * mm});
            skLineSegment(sketch, "E1143", {"start": v(201.39, 23) * mm, "end": v(201.76, 22.5) * mm});
            skLineSegment(sketch, "E1144", {"start": v(201.76, 22.5) * mm, "end": v(202.11, 22) * mm});
            skLineSegment(sketch, "E1145", {"start": v(202.11, 22) * mm, "end": v(202.76, 20.93) * mm});
            skLineSegment(sketch, "E1146", {"start": v(202.76, 20.93) * mm, "end": v(203.32, 19.83) * mm});
            skLineSegment(sketch, "E1147", {"start": v(203.32, 19.83) * mm, "end": v(203.81, 18.7) * mm});
            skLineSegment(sketch, "E1148", {"start": v(203.81, 18.7) * mm, "end": v(204.22, 17.54) * mm});
            skLineSegment(sketch, "E1149", {"start": v(204.22, 17.54) * mm, "end": v(204.55, 16.34) * mm});
            skLineSegment(sketch, "E1150", {"start": v(204.55, 16.34) * mm, "end": v(204.8, 15.1) * mm});
            skLineSegment(sketch, "E1151", {"start": v(204.8, 15.1) * mm, "end": v(204.97, 13.84) * mm});
            skLineSegment(sketch, "E1152", {"start": v(204.97, 13.84) * mm, "end": v(205.06, 12.54) * mm});
            skLineSegment(sketch, "E1153", {"start": v(205.06, 12.54) * mm, "end": v(197.44, 11.96) * mm});
            skLineSegment(sketch, "E1154", {"start": v(197.44, 11.96) * mm, "end": v(197.36, 12.66) * mm});
            skLineSegment(sketch, "E1155", {"start": v(197.36, 12.66) * mm, "end": v(197.25, 13.34) * mm});
            skLineSegment(sketch, "E1156", {"start": v(197.25, 13.34) * mm, "end": v(197.11, 14) * mm});
            skLineSegment(sketch, "E1157", {"start": v(197.11, 14) * mm, "end": v(196.95, 14.63) * mm});
            skLineSegment(sketch, "E1158", {"start": v(196.95, 14.63) * mm, "end": v(196.78, 15.25) * mm});
            skLineSegment(sketch, "E1159", {"start": v(196.78, 15.25) * mm, "end": v(196.57, 15.84) * mm});
            skLineSegment(sketch, "E1160", {"start": v(196.57, 15.84) * mm, "end": v(196.35, 16.4) * mm});
            skLineSegment(sketch, "E1161", {"start": v(196.35, 16.4) * mm, "end": v(196.1, 16.96) * mm});
            skLineSegment(sketch, "E1162", {"start": v(196.1, 16.96) * mm, "end": v(195.83, 17.48) * mm});
            skLineSegment(sketch, "E1163", {"start": v(195.83, 17.48) * mm, "end": v(195.53, 17.99) * mm});
            skLineSegment(sketch, "E1164", {"start": v(195.53, 17.99) * mm, "end": v(195.22, 18.47) * mm});
            skLineSegment(sketch, "E1165", {"start": v(195.22, 18.47) * mm, "end": v(194.88, 18.93) * mm});
            skLineSegment(sketch, "E1166", {"start": v(194.88, 18.93) * mm, "end": v(194.52, 19.37) * mm});
            skLineSegment(sketch, "E1167", {"start": v(194.52, 19.37) * mm, "end": v(194.13, 19.79) * mm});
            skLineSegment(sketch, "E1168", {"start": v(194.13, 19.79) * mm, "end": v(193.72, 20.18) * mm});
            skLineSegment(sketch, "E1169", {"start": v(193.72, 20.18) * mm, "end": v(193.3, 20.56) * mm});
            skLineSegment(sketch, "E1170", {"start": v(193.3, 20.56) * mm, "end": v(192.83, 20.91) * mm});
            skLineSegment(sketch, "E1171", {"start": v(192.83, 20.91) * mm, "end": v(192.35, 21.24) * mm});
            skLineSegment(sketch, "E1172", {"start": v(192.35, 21.24) * mm, "end": v(191.84, 21.55) * mm});
            skLineSegment(sketch, "E1173", {"start": v(191.84, 21.55) * mm, "end": v(191.3, 21.83) * mm});
            skLineSegment(sketch, "E1174", {"start": v(191.3, 21.83) * mm, "end": v(190.75, 22.1) * mm});
            skLineSegment(sketch, "E1175", {"start": v(190.75, 22.1) * mm, "end": v(190.16, 22.33) * mm});
            skLineSegment(sketch, "E1176", {"start": v(190.16, 22.33) * mm, "end": v(189.55, 22.55) * mm});
            skLineSegment(sketch, "E1177", {"start": v(189.55, 22.55) * mm, "end": v(188.9, 22.74) * mm});
            skLineSegment(sketch, "E1178", {"start": v(188.9, 22.74) * mm, "end": v(188.24, 22.9) * mm});
            skLineSegment(sketch, "E1179", {"start": v(188.24, 22.9) * mm, "end": v(187.55, 23.06) * mm});
            skLineSegment(sketch, "E1180", {"start": v(187.55, 23.06) * mm, "end": v(186.83, 23.18) * mm});
            skLineSegment(sketch, "E1181", {"start": v(186.83, 23.18) * mm, "end": v(186.08, 23.28) * mm});
            skLineSegment(sketch, "E1182", {"start": v(186.08, 23.28) * mm, "end": v(185.3, 23.36) * mm});
            skLineSegment(sketch, "E1183", {"start": v(185.3, 23.36) * mm, "end": v(184.5, 23.42) * mm});
            skLineSegment(sketch, "E1184", {"start": v(184.5, 23.42) * mm, "end": v(183.68, 23.45) * mm});
            skLineSegment(sketch, "E1185", {"start": v(183.68, 23.45) * mm, "end": v(182.83, 23.46) * mm});
            skLineSegment(sketch, "E1186", {"start": v(182.83, 23.46) * mm, "end": v(181.95, 23.45) * mm});
            skLineSegment(sketch, "E1187", {"start": v(181.95, 23.45) * mm, "end": v(181.1, 23.42) * mm});
            skLineSegment(sketch, "E1188", {"start": v(181.1, 23.42) * mm, "end": v(180.27, 23.37) * mm});
            skLineSegment(sketch, "E1189", {"start": v(180.27, 23.37) * mm, "end": v(179.48, 23.3) * mm});
            skLineSegment(sketch, "E1190", {"start": v(179.48, 23.3) * mm, "end": v(178.71, 23.2) * mm});
            skLineSegment(sketch, "E1191", {"start": v(178.71, 23.2) * mm, "end": v(177.98, 23.1) * mm});
            skLineSegment(sketch, "E1192", {"start": v(177.98, 23.1) * mm, "end": v(177.28, 22.96) * mm});
            skLineSegment(sketch, "E1193", {"start": v(177.28, 22.96) * mm, "end": v(176.6, 22.8) * mm});
            skLineSegment(sketch, "E1194", {"start": v(176.6, 22.8) * mm, "end": v(175.97, 22.63) * mm});
            skLineSegment(sketch, "E1195", {"start": v(175.97, 22.63) * mm, "end": v(175.36, 22.43) * mm});
            skLineSegment(sketch, "E1196", {"start": v(175.36, 22.43) * mm, "end": v(174.78, 22.22) * mm});
            skLineSegment(sketch, "E1197", {"start": v(174.78, 22.22) * mm, "end": v(174.23, 21.98) * mm});
            skLineSegment(sketch, "E1198", {"start": v(174.23, 21.98) * mm, "end": v(173.7, 21.72) * mm});
            skLineSegment(sketch, "E1199", {"start": v(173.7, 21.72) * mm, "end": v(173.22, 21.44) * mm});
            skLineSegment(sketch, "E1200", {"start": v(173.22, 21.44) * mm, "end": v(172.76, 21.14) * mm});
            skLineSegment(sketch, "E1201", {"start": v(172.76, 21.14) * mm, "end": v(172.34, 20.82) * mm});
            skLineSegment(sketch, "E1202", {"start": v(172.34, 20.82) * mm, "end": v(171.94, 20.5) * mm});
            skLineSegment(sketch, "E1203", {"start": v(171.94, 20.5) * mm, "end": v(171.56, 20.15) * mm});
            skLineSegment(sketch, "E1204", {"start": v(171.56, 20.15) * mm, "end": v(171.22, 19.8) * mm});
            skLineSegment(sketch, "E1205", {"start": v(171.22, 19.8) * mm, "end": v(170.9, 19.44) * mm});
            skLineSegment(sketch, "E1206", {"start": v(170.9, 19.44) * mm, "end": v(170.6, 19.07) * mm});
            skLineSegment(sketch, "E1207", {"start": v(170.6, 19.07) * mm, "end": v(170.33, 18.7) * mm});
            skLineSegment(sketch, "E1208", {"start": v(170.33, 18.7) * mm, "end": v(170.08, 18.3) * mm});
            skLineSegment(sketch, "E1209", {"start": v(170.08, 18.3) * mm, "end": v(169.86, 17.91) * mm});
            skLineSegment(sketch, "E1210", {"start": v(169.86, 17.91) * mm, "end": v(169.67, 17.51) * mm});
            skLineSegment(sketch, "E1211", {"start": v(169.67, 17.51) * mm, "end": v(169.5, 17.1) * mm});
            skLineSegment(sketch, "E1212", {"start": v(169.5, 17.1) * mm, "end": v(169.36, 16.68) * mm});
            skLineSegment(sketch, "E1213", {"start": v(169.36, 16.68) * mm, "end": v(169.25, 16.25) * mm});
            skLineSegment(sketch, "E1214", {"start": v(169.25, 16.25) * mm, "end": v(169.16, 15.82) * mm});
            skLineSegment(sketch, "E1215", {"start": v(169.16, 15.82) * mm, "end": v(169.1, 15.37) * mm});
            skLineSegment(sketch, "E1216", {"start": v(169.1, 15.37) * mm, "end": v(169.05, 14.92) * mm});
            skLineSegment(sketch, "E1217", {"start": v(169.05, 14.92) * mm, "end": v(169.04, 14.46) * mm});
            skLineSegment(sketch, "E1218", {"start": v(169.04, 14.46) * mm, "end": v(169.08, 13.67) * mm});
            skLineSegment(sketch, "E1219", {"start": v(169.08, 13.67) * mm, "end": v(169.19, 12.92) * mm});
            skLineSegment(sketch, "E1220", {"start": v(169.19, 12.92) * mm, "end": v(169.37, 12.2) * mm});
            skLineSegment(sketch, "E1221", {"start": v(169.37, 12.2) * mm, "end": v(169.62, 11.51) * mm});
            skLineSegment(sketch, "E1222", {"start": v(169.62, 11.51) * mm, "end": v(169.95, 10.87) * mm});
            skLineSegment(sketch, "E1223", {"start": v(169.95, 10.87) * mm, "end": v(170.35, 10.26) * mm});
            skLineSegment(sketch, "E1224", {"start": v(170.35, 10.26) * mm, "end": v(170.83, 9.68) * mm});
            skLineSegment(sketch, "E1225", {"start": v(170.83, 9.68) * mm, "end": v(171.37, 9.14) * mm});
            skLineSegment(sketch, "E1226", {"start": v(171.37, 9.14) * mm, "end": v(171.69, 8.88) * mm});
            skLineSegment(sketch, "E1227", {"start": v(171.69, 8.88) * mm, "end": v(172.06, 8.62) * mm});
            skLineSegment(sketch, "E1228", {"start": v(172.06, 8.62) * mm, "end": v(172.5, 8.35) * mm});
            skLineSegment(sketch, "E1229", {"start": v(172.5, 8.35) * mm, "end": v(172.98, 8.09) * mm});
            skLineSegment(sketch, "E1230", {"start": v(172.98, 8.09) * mm, "end": v(173.53, 7.83) * mm});
            skLineSegment(sketch, "E1231", {"start": v(173.53, 7.83) * mm, "end": v(174.13, 7.56) * mm});
            skLineSegment(sketch, "E1232", {"start": v(174.13, 7.56) * mm, "end": v(174.8, 7.3) * mm});
            skLineSegment(sketch, "E1233", {"start": v(174.8, 7.3) * mm, "end": v(175.51, 7.03) * mm});
            skLineSegment(sketch, "E1234", {"start": v(175.51, 7.03) * mm, "end": v(176.29, 6.76) * mm});
            skLineSegment(sketch, "E1235", {"start": v(176.29, 6.76) * mm, "end": v(177.12, 6.5) * mm});
            skLineSegment(sketch, "E1236", {"start": v(177.12, 6.5) * mm, "end": v(178.02, 6.22) * mm});
            skLineSegment(sketch, "E1237", {"start": v(178.02, 6.22) * mm, "end": v(178.97, 5.95) * mm});
            skLineSegment(sketch, "E1238", {"start": v(178.97, 5.95) * mm, "end": v(179.97, 5.68) * mm});
            skLineSegment(sketch, "E1239", {"start": v(179.97, 5.68) * mm, "end": v(181.04, 5.4) * mm});
            skLineSegment(sketch, "E1240", {"start": v(181.04, 5.4) * mm, "end": v(182.16, 5.14) * mm});
            skLineSegment(sketch, "E1241", {"start": v(182.16, 5.14) * mm, "end": v(183.34, 4.86) * mm});
            skLineSegment(sketch, "E1242", {"start": v(183.34, 4.86) * mm, "end": v(184.53, 4.6) * mm});
            skLineSegment(sketch, "E1243", {"start": v(184.53, 4.6) * mm, "end": v(185.67, 4.32) * mm});
            skLineSegment(sketch, "E1244", {"start": v(185.67, 4.32) * mm, "end": v(186.76, 4.06) * mm});
            skLineSegment(sketch, "E1245", {"start": v(186.76, 4.06) * mm, "end": v(187.8, 3.8) * mm});
            skLineSegment(sketch, "E1246", {"start": v(187.8, 3.8) * mm, "end": v(188.8, 3.55) * mm});
            skLineSegment(sketch, "E1247", {"start": v(188.8, 3.55) * mm, "end": v(189.75, 3.3) * mm});
            skLineSegment(sketch, "E1248", {"start": v(189.75, 3.3) * mm, "end": v(190.65, 3.05) * mm});
            skLineSegment(sketch, "E1249", {"start": v(190.65, 3.05) * mm, "end": v(191.5, 2.81) * mm});
            skLineSegment(sketch, "E1250", {"start": v(191.5, 2.81) * mm, "end": v(192.31, 2.57) * mm});
            skLineSegment(sketch, "E1251", {"start": v(192.31, 2.57) * mm, "end": v(193.07, 2.34) * mm});
            skLineSegment(sketch, "E1252", {"start": v(193.07, 2.34) * mm, "end": v(193.78, 2.11) * mm});
            skLineSegment(sketch, "E1253", {"start": v(193.78, 2.11) * mm, "end": v(194.45, 1.89) * mm});
            skLineSegment(sketch, "E1254", {"start": v(194.45, 1.89) * mm, "end": v(195.06, 1.67) * mm});
            skLineSegment(sketch, "E1255", {"start": v(195.06, 1.67) * mm, "end": v(195.63, 1.45) * mm});
            skLineSegment(sketch, "E1256", {"start": v(195.63, 1.45) * mm, "end": v(196.15, 1.24) * mm});
            skLineSegment(sketch, "E1257", {"start": v(196.15, 1.24) * mm, "end": v(196.63, 1.04) * mm});
            skLineSegment(sketch, "E1258", {"start": v(196.63, 1.04) * mm, "end": v(197.9, 0.41) * mm});
            skLineSegment(sketch, "E1259", {"start": v(197.9, 0.41) * mm, "end": v(199.07, -0.25) * mm});
            skLineSegment(sketch, "E1260", {"start": v(199.07, -0.25) * mm, "end": v(200.17, -0.96) * mm});
            skLineSegment(sketch, "E1261", {"start": v(200.17, -0.96) * mm, "end": v(201.18, -1.7) * mm});
            skLineSegment(sketch, "E1262", {"start": v(201.18, -1.7) * mm, "end": v(202.1, -2.49) * mm});
            skLineSegment(sketch, "E1263", {"start": v(202.1, -2.49) * mm, "end": v(202.94, -3.31) * mm});
            skLineSegment(sketch, "E1264", {"start": v(202.94, -3.31) * mm, "end": v(203.7, -4.18) * mm});
            skLineSegment(sketch, "E1265", {"start": v(203.7, -4.18) * mm, "end": v(204.36, -5.08) * mm});
            skLineSegment(sketch, "E1266", {"start": v(204.36, -5.08) * mm, "end": v(204.95, -6.03) * mm});
            skLineSegment(sketch, "E1267", {"start": v(204.95, -6.03) * mm, "end": v(205.45, -7) * mm});
            skLineSegment(sketch, "E1268", {"start": v(205.45, -7) * mm, "end": v(205.88, -8.02) * mm});
            skLineSegment(sketch, "E1269", {"start": v(205.88, -8.02) * mm, "end": v(206.23, -9.07) * mm});
            skLineSegment(sketch, "E1270", {"start": v(206.23, -9.07) * mm, "end": v(206.5, -10.15) * mm});
            skLineSegment(sketch, "E1271", {"start": v(206.5, -10.15) * mm, "end": v(206.7, -11.27) * mm});
            skLineSegment(sketch, "E1272", {"start": v(206.7, -11.27) * mm, "end": v(206.82, -12.43) * mm});
            skLineSegment(sketch, "E1273", {"start": v(206.82, -12.43) * mm, "end": v(206.86, -13.62) * mm});
            skLineSegment(sketch, "E1274", {"start": v(206.86, -13.62) * mm, "end": v(206.82, -14.8) * mm});
            skLineSegment(sketch, "E1275", {"start": v(206.82, -14.8) * mm, "end": v(206.69, -15.98) * mm});
            skLineSegment(sketch, "E1276", {"start": v(206.69, -15.98) * mm, "end": v(206.47, -17.13) * mm});
            skLineSegment(sketch, "E1277", {"start": v(206.47, -17.13) * mm, "end": v(206.17, -18.27) * mm});
            skLineSegment(sketch, "E1278", {"start": v(206.17, -18.27) * mm, "end": v(205.79, -19.39) * mm});
            skLineSegment(sketch, "E1279", {"start": v(205.79, -19.39) * mm, "end": v(205.32, -20.49) * mm});
            skLineSegment(sketch, "E1280", {"start": v(205.32, -20.49) * mm, "end": v(204.76, -21.57) * mm});
            skLineSegment(sketch, "E1281", {"start": v(204.76, -21.57) * mm, "end": v(204.12, -22.64) * mm});
            skLineSegment(sketch, "E1282", {"start": v(204.12, -22.64) * mm, "end": v(203.4, -23.67) * mm});
            skLineSegment(sketch, "E1283", {"start": v(203.4, -23.67) * mm, "end": v(202.6, -24.64) * mm});
            skLineSegment(sketch, "E1284", {"start": v(202.6, -24.64) * mm, "end": v(201.72, -25.55) * mm});
            skLineSegment(sketch, "E1285", {"start": v(201.72, -25.55) * mm, "end": v(200.78, -26.4) * mm});
            skLineSegment(sketch, "E1286", {"start": v(200.78, -26.4) * mm, "end": v(199.75, -27.2) * mm});
            skLineSegment(sketch, "E1287", {"start": v(199.75, -27.2) * mm, "end": v(198.66, -27.94) * mm});
            skLineSegment(sketch, "E1288", {"start": v(198.66, -27.94) * mm, "end": v(197.48, -28.61) * mm});
            skLineSegment(sketch, "E1289", {"start": v(197.48, -28.61) * mm, "end": v(196.24, -29.23) * mm});
            skLineSegment(sketch, "E1290", {"start": v(196.24, -29.23) * mm, "end": v(194.93, -29.78) * mm});
            skLineSegment(sketch, "E1291", {"start": v(194.93, -29.78) * mm, "end": v(193.59, -30.26) * mm});
            skLineSegment(sketch, "E1292", {"start": v(193.59, -30.26) * mm, "end": v(192.2, -30.66) * mm});
            skLineSegment(sketch, "E1293", {"start": v(192.2, -30.66) * mm, "end": v(190.78, -31) * mm});
            skLineSegment(sketch, "E1294", {"start": v(190.78, -31) * mm, "end": v(189.31, -31.25) * mm});
            skLineSegment(sketch, "E1295", {"start": v(189.31, -31.25) * mm, "end": v(187.8, -31.44) * mm});
            skLineSegment(sketch, "E1296", {"start": v(187.8, -31.44) * mm, "end": v(186.26, -31.55) * mm});
            skLineSegment(sketch, "E1297", {"start": v(186.26, -31.55) * mm, "end": v(184.68, -31.58) * mm});
            skLineSegment(sketch, "E1298", {"start": v(184.68, -31.58) * mm, "end": v(183.67, -31.57) * mm});
            skLineSegment(sketch, "E1299", {"start": v(183.67, -31.57) * mm, "end": v(182.68, -31.55) * mm});
            skLineSegment(sketch, "E1300", {"start": v(182.68, -31.55) * mm, "end": v(181.71, -31.5) * mm});
            skLineSegment(sketch, "E1301", {"start": v(181.71, -31.5) * mm, "end": v(180.77, -31.43) * mm});
            skLineSegment(sketch, "E1302", {"start": v(180.77, -31.43) * mm, "end": v(179.84, -31.35) * mm});
            skLineSegment(sketch, "E1303", {"start": v(179.84, -31.35) * mm, "end": v(178.94, -31.25) * mm});
            skLineSegment(sketch, "E1304", {"start": v(178.94, -31.25) * mm, "end": v(178.05, -31.13) * mm});
            skLineSegment(sketch, "E1305", {"start": v(178.05, -31.13) * mm, "end": v(177.2, -30.99) * mm});
            skLineSegment(sketch, "E1306", {"start": v(177.2, -30.99) * mm, "end": v(176.35, -30.83) * mm});
            skLineSegment(sketch, "E1307", {"start": v(176.35, -30.83) * mm, "end": v(175.53, -30.66) * mm});
            skLineSegment(sketch, "E1308", {"start": v(175.53, -30.66) * mm, "end": v(174.72, -30.46) * mm});
            skLineSegment(sketch, "E1309", {"start": v(174.72, -30.46) * mm, "end": v(173.94, -30.25) * mm});
            skLineSegment(sketch, "E1310", {"start": v(173.94, -30.25) * mm, "end": v(173.18, -30.02) * mm});
            skLineSegment(sketch, "E1311", {"start": v(173.18, -30.02) * mm, "end": v(172.44, -29.77) * mm});
            skLineSegment(sketch, "E1312", {"start": v(172.44, -29.77) * mm, "end": v(171.72, -29.5) * mm});
            skLineSegment(sketch, "E1313", {"start": v(171.72, -29.5) * mm, "end": v(171.03, -29.2) * mm});
            skLineSegment(sketch, "E1314", {"start": v(171.03, -29.2) * mm, "end": v(170.35, -28.9) * mm});
            skLineSegment(sketch, "E1315", {"start": v(170.35, -28.9) * mm, "end": v(169.69, -28.58) * mm});
            skLineSegment(sketch, "E1316", {"start": v(169.69, -28.58) * mm, "end": v(169.04, -28.24) * mm});
            skLineSegment(sketch, "E1317", {"start": v(169.04, -28.24) * mm, "end": v(168.42, -27.87) * mm});
            skLineSegment(sketch, "E1318", {"start": v(168.42, -27.87) * mm, "end": v(167.82, -27.5) * mm});
            skLineSegment(sketch, "E1319", {"start": v(167.82, -27.5) * mm, "end": v(167.23, -27.1) * mm});
            skLineSegment(sketch, "E1320", {"start": v(167.23, -27.1) * mm, "end": v(166.66, -26.67) * mm});
            skLineSegment(sketch, "E1321", {"start": v(166.66, -26.67) * mm, "end": v(166.11, -26.24) * mm});
            skLineSegment(sketch, "E1322", {"start": v(166.11, -26.24) * mm, "end": v(165.58, -25.78) * mm});
            skLineSegment(sketch, "E1323", {"start": v(165.58, -25.78) * mm, "end": v(165.07, -25.3) * mm});
            skLineSegment(sketch, "E1324", {"start": v(165.07, -25.3) * mm, "end": v(164.58, -24.81) * mm});
            skLineSegment(sketch, "E1325", {"start": v(164.58, -24.81) * mm, "end": v(164.1, -24.3) * mm});
            skLineSegment(sketch, "E1326", {"start": v(164.1, -24.3) * mm, "end": v(163.65, -23.77) * mm});
            skLineSegment(sketch, "E1327", {"start": v(163.65, -23.77) * mm, "end": v(163.2, -23.22) * mm});
            skLineSegment(sketch, "E1328", {"start": v(163.2, -23.22) * mm, "end": v(162.8, -22.65) * mm});
            skLineSegment(sketch, "E1329", {"start": v(162.8, -22.65) * mm, "end": v(162.39, -22.07) * mm});
            skLineSegment(sketch, "E1330", {"start": v(162.39, -22.07) * mm, "end": v(162.01, -21.47) * mm});
            skLineSegment(sketch, "E1331", {"start": v(162.01, -21.47) * mm, "end": v(161.65, -20.86) * mm});
            skLineSegment(sketch, "E1332", {"start": v(161.65, -20.86) * mm, "end": v(161.32, -20.24) * mm});
            skLineSegment(sketch, "E1333", {"start": v(161.32, -20.24) * mm, "end": v(161, -19.6) * mm});
            skLineSegment(sketch, "E1334", {"start": v(161, -19.6) * mm, "end": v(160.72, -18.97) * mm});
            skLineSegment(sketch, "E1335", {"start": v(160.72, -18.97) * mm, "end": v(160.46, -18.32) * mm});
            skLineSegment(sketch, "E1336", {"start": v(160.46, -18.32) * mm, "end": v(160.22, -17.66) * mm});
            skLineSegment(sketch, "E1337", {"start": v(160.22, -17.66) * mm, "end": v(160, -16.99) * mm});
            skLineSegment(sketch, "E1338", {"start": v(160, -16.99) * mm, "end": v(159.8, -16.3) * mm});
            skLineSegment(sketch, "E1339", {"start": v(159.8, -16.3) * mm, "end": v(159.64, -15.62) * mm});
            skLineSegment(sketch, "E1340", {"start": v(159.64, -15.62) * mm, "end": v(159.49, -14.92) * mm});
            skLineSegment(sketch, "E1341", {"start": v(159.49, -14.92) * mm, "end": v(159.36, -14.21) * mm});
            skLineSegment(sketch, "E1342", {"start": v(159.36, -14.21) * mm, "end": v(159.26, -13.5) * mm});
            skLineSegment(sketch, "E1343", {"start": v(159.26, -13.5) * mm, "end": v(159.18, -12.77) * mm});
            skLineSegment(sketch, "E1344", {"start": v(159.18, -12.77) * mm, "end": v(159.13, -12.03) * mm});
            skLineSegment(sketch, "E1345", {"start": v(126.35, 20.97) * mm, "end": v(118.99, 20.97) * mm});
            skLineSegment(sketch, "E1346", {"start": v(118.99, 20.97) * mm, "end": v(118.99, 29.44) * mm});
            skLineSegment(sketch, "E1347", {"start": v(118.99, 29.44) * mm, "end": v(126.35, 29.44) * mm});
            skLineSegment(sketch, "E1348", {"start": v(126.35, 29.44) * mm, "end": v(126.35, 20.97) * mm});
            skLineSegment(sketch, "E1349", {"start": v(126.35, -30.56) * mm, "end": v(118.99, -30.56) * mm});
            skLineSegment(sketch, "E1350", {"start": v(118.99, -30.56) * mm, "end": v(118.99, 12.9) * mm});
            skLineSegment(sketch, "E1351", {"start": v(118.99, 12.9) * mm, "end": v(126.35, 12.9) * mm});
            skLineSegment(sketch, "E1352", {"start": v(126.35, 12.9) * mm, "end": v(126.35, -30.56) * mm});
            skLineSegment(sketch, "E1353", {"start": v(37.83, -30.56) * mm, "end": v(30.46, -30.56) * mm});
            skLineSegment(sketch, "E1354", {"start": v(30.46, -30.56) * mm, "end": v(30.46, 29.44) * mm});
            skLineSegment(sketch, "E1355", {"start": v(30.46, 29.44) * mm, "end": v(37.83, 29.44) * mm});
            skLineSegment(sketch, "E1356", {"start": v(37.83, 29.44) * mm, "end": v(37.83, -4.78) * mm});
            skLineSegment(sketch, "E1357", {"start": v(37.83, -4.78) * mm, "end": v(55.26, 12.9) * mm});
            skLineSegment(sketch, "E1358", {"start": v(55.26, 12.9) * mm, "end": v(64.8, 12.9) * mm});
            skLineSegment(sketch, "E1359", {"start": v(64.8, 12.9) * mm, "end": v(48.18, -3.22) * mm});
            skLineSegment(sketch, "E1360", {"start": v(48.18, -3.22) * mm, "end": v(66.48, -30.56) * mm});
            skLineSegment(sketch, "E1361", {"start": v(66.48, -30.56) * mm, "end": v(57.39, -30.56) * mm});
            skLineSegment(sketch, "E1362", {"start": v(57.39, -30.56) * mm, "end": v(43.02, -8.34) * mm});
            skLineSegment(sketch, "E1363", {"start": v(43.02, -8.34) * mm, "end": v(37.83, -13.33) * mm});
            skLineSegment(sketch, "E1364", {"start": v(37.83, -13.33) * mm, "end": v(37.83, -30.56) * mm});
            skLineSegment(sketch, "E1365", {"start": v(-55.45, -30.56) * mm, "end": v(-62.81, -30.56) * mm});
            skLineSegment(sketch, "E1366", {"start": v(-62.81, -30.56) * mm, "end": v(-62.81, 12.9) * mm});
            skLineSegment(sketch, "E1367", {"start": v(-62.81, 12.9) * mm, "end": v(-56.18, 12.9) * mm});
            skLineSegment(sketch, "E1368", {"start": v(-56.18, 12.9) * mm, "end": v(-56.18, 6.73) * mm});
            skLineSegment(sketch, "E1369", {"start": v(-56.18, 6.73) * mm, "end": v(-55.57, 7.6) * mm});
            skLineSegment(sketch, "E1370", {"start": v(-55.57, 7.6) * mm, "end": v(-54.92, 8.4) * mm});
            skLineSegment(sketch, "E1371", {"start": v(-54.92, 8.4) * mm, "end": v(-54.24, 9.16) * mm});
            skLineSegment(sketch, "E1372", {"start": v(-54.24, 9.16) * mm, "end": v(-53.52, 9.86) * mm});
            skLineSegment(sketch, "E1373", {"start": v(-53.52, 9.86) * mm, "end": v(-52.78, 10.5) * mm});
            skLineSegment(sketch, "E1374", {"start": v(-52.78, 10.5) * mm, "end": v(-52, 11.09) * mm});
            skLineSegment(sketch, "E1375", {"start": v(-52, 11.09) * mm, "end": v(-51.18, 11.62) * mm});
            skLineSegment(sketch, "E1376", {"start": v(-51.18, 11.62) * mm, "end": v(-50.33, 12.1) * mm});
            skLineSegment(sketch, "E1377", {"start": v(-50.33, 12.1) * mm, "end": v(-49.45, 12.52) * mm});
            skLineSegment(sketch, "E1378", {"start": v(-49.45, 12.52) * mm, "end": v(-48.54, 12.88) * mm});
            skLineSegment(sketch, "E1379", {"start": v(-48.54, 12.88) * mm, "end": v(-47.59, 13.19) * mm});
            skLineSegment(sketch, "E1380", {"start": v(-47.59, 13.19) * mm, "end": v(-46.6, 13.44) * mm});
            skLineSegment(sketch, "E1381", {"start": v(-46.6, 13.44) * mm, "end": v(-45.6, 13.64) * mm});
            skLineSegment(sketch, "E1382", {"start": v(-45.6, 13.64) * mm, "end": v(-44.55, 13.78) * mm});
            skLineSegment(sketch, "E1383", {"start": v(-44.55, 13.78) * mm, "end": v(-43.46, 13.86) * mm});
            skLineSegment(sketch, "E1384", {"start": v(-43.46, 13.86) * mm, "end": v(-42.35, 13.89) * mm});
            skLineSegment(sketch, "E1385", {"start": v(-42.35, 13.89) * mm, "end": v(-41.38, 13.87) * mm});
            skLineSegment(sketch, "E1386", {"start": v(-41.38, 13.87) * mm, "end": v(-40.43, 13.8) * mm});
            skLineSegment(sketch, "E1387", {"start": v(-40.43, 13.8) * mm, "end": v(-39.5, 13.69) * mm});
            skLineSegment(sketch, "E1388", {"start": v(-39.5, 13.69) * mm, "end": v(-38.58, 13.53) * mm});
            skLineSegment(sketch, "E1389", {"start": v(-38.58, 13.53) * mm, "end": v(-37.69, 13.34) * mm});
            skLineSegment(sketch, "E1390", {"start": v(-37.69, 13.34) * mm, "end": v(-36.81, 13.1) * mm});
            skLineSegment(sketch, "E1391", {"start": v(-36.81, 13.1) * mm, "end": v(-35.96, 12.8) * mm});
            skLineSegment(sketch, "E1392", {"start": v(-35.96, 12.8) * mm, "end": v(-35.13, 12.48) * mm});
            skLineSegment(sketch, "E1393", {"start": v(-35.13, 12.48) * mm, "end": v(-34.33, 12.1) * mm});
            skLineSegment(sketch, "E1394", {"start": v(-34.33, 12.1) * mm, "end": v(-33.58, 11.71) * mm});
            skLineSegment(sketch, "E1395", {"start": v(-33.58, 11.71) * mm, "end": v(-32.89, 11.3) * mm});
            skLineSegment(sketch, "E1396", {"start": v(-32.89, 11.3) * mm, "end": v(-32.25, 10.84) * mm});
            skLineSegment(sketch, "E1397", {"start": v(-32.25, 10.84) * mm, "end": v(-31.66, 10.37) * mm});
            skLineSegment(sketch, "E1398", {"start": v(-31.66, 10.37) * mm, "end": v(-31.12, 9.86) * mm});
            skLineSegment(sketch, "E1399", {"start": v(-31.12, 9.86) * mm, "end": v(-30.63, 9.33) * mm});
            skLineSegment(sketch, "E1400", {"start": v(-30.63, 9.33) * mm, "end": v(-30.2, 8.77) * mm});
            skLineSegment(sketch, "E1401", {"start": v(-30.2, 8.77) * mm, "end": v(-29.8, 8.19) * mm});
            skLineSegment(sketch, "E1402", {"start": v(-29.8, 8.19) * mm, "end": v(-29.44, 7.57) * mm});
            skLineSegment(sketch, "E1403", {"start": v(-29.44, 7.57) * mm, "end": v(-29.1, 6.93) * mm});
            skLineSegment(sketch, "E1404", {"start": v(-29.1, 6.93) * mm, "end": v(-28.8, 6.26) * mm});
            skLineSegment(sketch, "E1405", {"start": v(-28.8, 6.26) * mm, "end": v(-28.53, 5.57) * mm});
            skLineSegment(sketch, "E1406", {"start": v(-28.53, 5.57) * mm, "end": v(-28.3, 4.85) * mm});
            skLineSegment(sketch, "E1407", {"start": v(-28.3, 4.85) * mm, "end": v(-28.08, 4.1) * mm});
            skLineSegment(sketch, "E1408", {"start": v(-28.08, 4.1) * mm, "end": v(-27.9, 3.33) * mm});
            skLineSegment(sketch, "E1409", {"start": v(-27.9, 3.33) * mm, "end": v(-27.85, 3.06) * mm});
            skLineSegment(sketch, "E1410", {"start": v(-27.85, 3.06) * mm, "end": v(-27.8, 2.77) * mm});
            skLineSegment(sketch, "E1411", {"start": v(-27.8, 2.77) * mm, "end": v(-27.76, 2.45) * mm});
            skLineSegment(sketch, "E1412", {"start": v(-27.76, 2.45) * mm, "end": v(-27.72, 2.11) * mm});
            skLineSegment(sketch, "E1413", {"start": v(-27.72, 2.11) * mm, "end": v(-27.69, 1.75) * mm});
            skLineSegment(sketch, "E1414", {"start": v(-27.69, 1.75) * mm, "end": v(-27.65, 1.36) * mm});
            skLineSegment(sketch, "E1415", {"start": v(-27.65, 1.36) * mm, "end": v(-27.62, 0.95) * mm});
            skLineSegment(sketch, "E1416", {"start": v(-27.62, 0.95) * mm, "end": v(-27.6, 0.51) * mm});
            skLineSegment(sketch, "E1417", {"start": v(-27.6, 0.51) * mm, "end": v(-27.57, 0.05) * mm});
            skLineSegment(sketch, "E1418", {"start": v(-27.57, 0.05) * mm, "end": v(-27.55, -0.43) * mm});
            skLineSegment(sketch, "E1419", {"start": v(-27.55, -0.43) * mm, "end": v(-27.53, -0.94) * mm});
            skLineSegment(sketch, "E1420", {"start": v(-27.53, -0.94) * mm, "end": v(-27.52, -1.47) * mm});
            skLineSegment(sketch, "E1421", {"start": v(-27.52, -1.47) * mm, "end": v(-27.5, -2.02) * mm});
            skLineSegment(sketch, "E1422", {"start": v(-27.5, -2.02) * mm, "end": v(-27.5, -2.6) * mm});
            skLineSegment(sketch, "E1423", {"start": v(-27.5, -2.6) * mm, "end": v(-27.5, -3.2) * mm});
            skLineSegment(sketch, "E1424", {"start": v(-27.5, -3.2) * mm, "end": v(-27.5, -3.83) * mm});
            skLineSegment(sketch, "E1425", {"start": v(-27.5, -3.83) * mm, "end": v(-27.5, -30.56) * mm});
            skLineSegment(sketch, "E1426", {"start": v(-27.5, -30.56) * mm, "end": v(-34.86, -30.56) * mm});
            skLineSegment(sketch, "E1427", {"start": v(-34.86, -30.56) * mm, "end": v(-34.86, -4.12) * mm});
            skLineSegment(sketch, "E1428", {"start": v(-34.86, -4.12) * mm, "end": v(-34.87, -3.03) * mm});
            skLineSegment(sketch, "E1429", {"start": v(-34.87, -3.03) * mm, "end": v(-34.91, -2.01) * mm});
            skLineSegment(sketch, "E1430", {"start": v(-34.91, -2.01) * mm, "end": v(-34.98, -1.06) * mm});
            skLineSegment(sketch, "E1431", {"start": v(-34.98, -1.06) * mm, "end": v(-35.08, -0.19) * mm});
            skLineSegment(sketch, "E1432", {"start": v(-35.08, -0.19) * mm, "end": v(-35.2, 0.62) * mm});
            skLineSegment(sketch, "E1433", {"start": v(-35.2, 0.62) * mm, "end": v(-35.34, 1.35) * mm});
            skLineSegment(sketch, "E1434", {"start": v(-35.34, 1.35) * mm, "end": v(-35.52, 2.02) * mm});
            skLineSegment(sketch, "E1435", {"start": v(-35.52, 2.02) * mm, "end": v(-35.72, 2.61) * mm});
            skLineSegment(sketch, "E1436", {"start": v(-35.72, 2.61) * mm, "end": v(-35.96, 3.16) * mm});
            skLineSegment(sketch, "E1437", {"start": v(-35.96, 3.16) * mm, "end": v(-36.23, 3.67) * mm});
            skLineSegment(sketch, "E1438", {"start": v(-36.23, 3.67) * mm, "end": v(-36.55, 4.16) * mm});
            skLineSegment(sketch, "E1439", {"start": v(-36.55, 4.16) * mm, "end": v(-36.91, 4.62) * mm});
            skLineSegment(sketch, "E1440", {"start": v(-36.91, 4.62) * mm, "end": v(-37.31, 5.05) * mm});
            skLineSegment(sketch, "E1441", {"start": v(-37.31, 5.05) * mm, "end": v(-37.76, 5.45) * mm});
            skLineSegment(sketch, "E1442", {"start": v(-37.76, 5.45) * mm, "end": v(-38.24, 5.83) * mm});
            skLineSegment(sketch, "E1443", {"start": v(-38.24, 5.83) * mm, "end": v(-38.77, 6.17) * mm});
            skLineSegment(sketch, "E1444", {"start": v(-38.77, 6.17) * mm, "end": v(-39.33, 6.48) * mm});
            skLineSegment(sketch, "E1445", {"start": v(-39.33, 6.48) * mm, "end": v(-39.91, 6.75) * mm});
            skLineSegment(sketch, "E1446", {"start": v(-39.91, 6.75) * mm, "end": v(-40.52, 6.98) * mm});
            skLineSegment(sketch, "E1447", {"start": v(-40.52, 6.98) * mm, "end": v(-41.15, 7.17) * mm});
            skLineSegment(sketch, "E1448", {"start": v(-41.15, 7.17) * mm, "end": v(-41.8, 7.32) * mm});
            skLineSegment(sketch, "E1449", {"start": v(-41.8, 7.32) * mm, "end": v(-42.48, 7.42) * mm});
            skLineSegment(sketch, "E1450", {"start": v(-42.48, 7.42) * mm, "end": v(-43.18, 7.48) * mm});
            skLineSegment(sketch, "E1451", {"start": v(-43.18, 7.48) * mm, "end": v(-43.9, 7.5) * mm});
            skLineSegment(sketch, "E1452", {"start": v(-43.9, 7.5) * mm, "end": v(-44.49, 7.5) * mm});
            skLineSegment(sketch, "E1453", {"start": v(-44.49, 7.5) * mm, "end": v(-45.06, 7.46) * mm});
            skLineSegment(sketch, "E1454", {"start": v(-45.06, 7.46) * mm, "end": v(-45.63, 7.4) * mm});
            skLineSegment(sketch, "E1455", {"start": v(-45.63, 7.4) * mm, "end": v(-46.18, 7.32) * mm});
            skLineSegment(sketch, "E1456", {"start": v(-46.18, 7.32) * mm, "end": v(-46.72, 7.21) * mm});
            skLineSegment(sketch, "E1457", {"start": v(-46.72, 7.21) * mm, "end": v(-47.25, 7.08) * mm});
            skLineSegment(sketch, "E1458", {"start": v(-47.25, 7.08) * mm, "end": v(-47.78, 6.93) * mm});
            skLineSegment(sketch, "E1459", {"start": v(-47.78, 6.93) * mm, "end": v(-48.3, 6.76) * mm});
            skLineSegment(sketch, "E1460", {"start": v(-48.3, 6.76) * mm, "end": v(-48.8, 6.56) * mm});
            skLineSegment(sketch, "E1461", {"start": v(-48.8, 6.56) * mm, "end": v(-49.29, 6.34) * mm});
            skLineSegment(sketch, "E1462", {"start": v(-49.29, 6.34) * mm, "end": v(-49.77, 6.1) * mm});
            skLineSegment(sketch, "E1463", {"start": v(-49.77, 6.1) * mm, "end": v(-50.24, 5.82) * mm});
            skLineSegment(sketch, "E1464", {"start": v(-50.24, 5.82) * mm, "end": v(-50.7, 5.53) * mm});
            skLineSegment(sketch, "E1465", {"start": v(-50.7, 5.53) * mm, "end": v(-51.16, 5.22) * mm});
            skLineSegment(sketch, "E1466", {"start": v(-51.16, 5.22) * mm, "end": v(-51.6, 4.88) * mm});
            skLineSegment(sketch, "E1467", {"start": v(-51.6, 4.88) * mm, "end": v(-52.03, 4.52) * mm});
            skLineSegment(sketch, "E1468", {"start": v(-52.03, 4.52) * mm, "end": v(-52.44, 4.12) * mm});
            skLineSegment(sketch, "E1469", {"start": v(-52.44, 4.12) * mm, "end": v(-52.83, 3.68) * mm});
            skLineSegment(sketch, "E1470", {"start": v(-52.83, 3.68) * mm, "end": v(-53.2, 3.2) * mm});
            skLineSegment(sketch, "E1471", {"start": v(-53.2, 3.2) * mm, "end": v(-53.53, 2.69) * mm});
            skLineSegment(sketch, "E1472", {"start": v(-53.53, 2.69) * mm, "end": v(-53.83, 2.12) * mm});
            skLineSegment(sketch, "E1473", {"start": v(-53.83, 2.12) * mm, "end": v(-54.11, 1.52) * mm});
            skLineSegment(sketch, "E1474", {"start": v(-54.11, 1.52) * mm, "end": v(-54.37, 0.87) * mm});
            skLineSegment(sketch, "E1475", {"start": v(-54.37, 0.87) * mm, "end": v(-54.6, 0.19) * mm});
            skLineSegment(sketch, "E1476", {"start": v(-54.6, 0.19) * mm, "end": v(-54.8, -0.54) * mm});
            skLineSegment(sketch, "E1477", {"start": v(-54.8, -0.54) * mm, "end": v(-54.97, -1.31) * mm});
            skLineSegment(sketch, "E1478", {"start": v(-54.97, -1.31) * mm, "end": v(-55.11, -2.13) * mm});
            skLineSegment(sketch, "E1479", {"start": v(-55.11, -2.13) * mm, "end": v(-55.23, -2.98) * mm});
            skLineSegment(sketch, "E1480", {"start": v(-55.23, -2.98) * mm, "end": v(-55.33, -3.88) * mm});
            skLineSegment(sketch, "E1481", {"start": v(-55.33, -3.88) * mm, "end": v(-55.4, -4.82) * mm});
            skLineSegment(sketch, "E1482", {"start": v(-55.4, -4.82) * mm, "end": v(-55.43, -5.8) * mm});
            skLineSegment(sketch, "E1483", {"start": v(-55.43, -5.8) * mm, "end": v(-55.45, -6.82) * mm});
            skLineSegment(sketch, "E1484", {"start": v(-55.45, -6.82) * mm, "end": v(-55.45, -30.56) * mm});
            skLineSegment(sketch, "E1485", {"start": v(-117.12, -24.04) * mm, "end": v(-116.63, -23.97) * mm});
            skLineSegment(sketch, "E1486", {"start": v(-116.63, -23.97) * mm, "end": v(-115.57, -30.48) * mm});
            skLineSegment(sketch, "E1487", {"start": v(-115.57, -30.48) * mm, "end": v(-116.34, -30.63) * mm});
            skLineSegment(sketch, "E1488", {"start": v(-116.34, -30.63) * mm, "end": v(-117.08, -30.76) * mm});
            skLineSegment(sketch, "E1489", {"start": v(-117.08, -30.76) * mm, "end": v(-117.81, -30.88) * mm});
            skLineSegment(sketch, "E1490", {"start": v(-117.81, -30.88) * mm, "end": v(-118.52, -30.97) * mm});
            skLineSegment(sketch, "E1491", {"start": v(-118.52, -30.97) * mm, "end": v(-119.2, -31.04) * mm});
            skLineSegment(sketch, "E1492", {"start": v(-119.2, -31.04) * mm, "end": v(-119.87, -31.1) * mm});
            skLineSegment(sketch, "E1493", {"start": v(-119.87, -31.1) * mm, "end": v(-120.51, -31.12) * mm});
            skLineSegment(sketch, "E1494", {"start": v(-120.51, -31.12) * mm, "end": v(-121.14, -31.13) * mm});
            skLineSegment(sketch, "E1495", {"start": v(-121.14, -31.13) * mm, "end": v(-122.11, -31.11) * mm});
            skLineSegment(sketch, "E1496", {"start": v(-122.11, -31.11) * mm, "end": v(-123.03, -31.05) * mm});
            skLineSegment(sketch, "E1497", {"start": v(-123.03, -31.05) * mm, "end": v(-123.9, -30.95) * mm});
            skLineSegment(sketch, "E1498", {"start": v(-123.9, -30.95) * mm, "end": v(-124.7, -30.82) * mm});
            skLineSegment(sketch, "E1499", {"start": v(-124.7, -30.82) * mm, "end": v(-125.45, -30.64) * mm});
            skLineSegment(sketch, "E1500", {"start": v(-125.45, -30.64) * mm, "end": v(-126.14, -30.42) * mm});
            skLineSegment(sketch, "E1501", {"start": v(-126.14, -30.42) * mm, "end": v(-126.78, -30.16) * mm});
            skLineSegment(sketch, "E1502", {"start": v(-126.78, -30.16) * mm, "end": v(-127.36, -29.86) * mm});
            skLineSegment(sketch, "E1503", {"start": v(-127.36, -29.86) * mm, "end": v(-127.89, -29.53) * mm});
            skLineSegment(sketch, "E1504", {"start": v(-127.89, -29.53) * mm, "end": v(-128.38, -29.18) * mm});
            skLineSegment(sketch, "E1505", {"start": v(-128.38, -29.18) * mm, "end": v(-128.83, -28.8) * mm});
            skLineSegment(sketch, "E1506", {"start": v(-128.83, -28.8) * mm, "end": v(-129.24, -28.4) * mm});
            skLineSegment(sketch, "E1507", {"start": v(-129.24, -28.4) * mm, "end": v(-129.6, -27.97) * mm});
            skLineSegment(sketch, "E1508", {"start": v(-129.6, -27.97) * mm, "end": v(-129.94, -27.51) * mm});
            skLineSegment(sketch, "E1509", {"start": v(-129.94, -27.51) * mm, "end": v(-130.22, -27.03) * mm});
            skLineSegment(sketch, "E1510", {"start": v(-130.22, -27.03) * mm, "end": v(-130.47, -26.53) * mm});
            skLineSegment(sketch, "E1511", {"start": v(-130.47, -26.53) * mm, "end": v(-130.58, -26.25) * mm});
            skLineSegment(sketch, "E1512", {"start": v(-130.58, -26.25) * mm, "end": v(-130.68, -25.94) * mm});
            skLineSegment(sketch, "E1513", {"start": v(-130.68, -25.94) * mm, "end": v(-130.77, -25.6) * mm});
            skLineSegment(sketch, "E1514", {"start": v(-130.77, -25.6) * mm, "end": v(-130.86, -25.2) * mm});
            skLineSegment(sketch, "E1515", {"start": v(-130.86, -25.2) * mm, "end": v(-130.94, -24.8) * mm});
            skLineSegment(sketch, "E1516", {"start": v(-130.94, -24.8) * mm, "end": v(-131.02, -24.34) * mm});
            skLineSegment(sketch, "E1517", {"start": v(-131.02, -24.34) * mm, "end": v(-131.08, -23.85) * mm});
            skLineSegment(sketch, "E1518", {"start": v(-131.08, -23.85) * mm, "end": v(-131.14, -23.32) * mm});
            skLineSegment(sketch, "E1519", {"start": v(-131.14, -23.32) * mm, "end": v(-131.2, -22.76) * mm});
            skLineSegment(sketch, "E1520", {"start": v(-131.2, -22.76) * mm, "end": v(-131.24, -22.16) * mm});
            skLineSegment(sketch, "E1521", {"start": v(-131.24, -22.16) * mm, "end": v(-131.28, -21.53) * mm});
            skLineSegment(sketch, "E1522", {"start": v(-131.28, -21.53) * mm, "end": v(-131.31, -20.86) * mm});
            skLineSegment(sketch, "E1523", {"start": v(-131.31, -20.86) * mm, "end": v(-131.34, -20.16) * mm});
            skLineSegment(sketch, "E1524", {"start": v(-131.34, -20.16) * mm, "end": v(-131.35, -19.42) * mm});
            skLineSegment(sketch, "E1525", {"start": v(-131.35, -19.42) * mm, "end": v(-131.37, -18.64) * mm});
            skLineSegment(sketch, "E1526", {"start": v(-131.37, -18.64) * mm, "end": v(-131.37, -17.83) * mm});
            skLineSegment(sketch, "E1527", {"start": v(-131.37, -17.83) * mm, "end": v(-131.37, 7.18) * mm});
            skLineSegment(sketch, "E1528", {"start": v(-131.37, 7.18) * mm, "end": v(-136.77, 7.18) * mm});
            skLineSegment(sketch, "E1529", {"start": v(-136.77, 7.18) * mm, "end": v(-136.77, 12.9) * mm});
            skLineSegment(sketch, "E1530", {"start": v(-136.77, 12.9) * mm, "end": v(-131.37, 12.9) * mm});
            skLineSegment(sketch, "E1531", {"start": v(-131.37, 12.9) * mm, "end": v(-131.37, 23.67) * mm});
            skLineSegment(sketch, "E1532", {"start": v(-131.37, 23.67) * mm, "end": v(-124.04, 28.09) * mm});
            skLineSegment(sketch, "E1533", {"start": v(-124.04, 28.09) * mm, "end": v(-124.04, 12.9) * mm});
            skLineSegment(sketch, "E1534", {"start": v(-124.04, 12.9) * mm, "end": v(-116.63, 12.9) * mm});
            skLineSegment(sketch, "E1535", {"start": v(-116.63, 12.9) * mm, "end": v(-116.63, 7.18) * mm});
            skLineSegment(sketch, "E1536", {"start": v(-116.63, 7.18) * mm, "end": v(-124.04, 7.18) * mm});
            skLineSegment(sketch, "E1537", {"start": v(-124.04, 7.18) * mm, "end": v(-124.04, -18.24) * mm});
            skLineSegment(sketch, "E1538", {"start": v(-124.04, -18.24) * mm, "end": v(-124.04, -19) * mm});
            skLineSegment(sketch, "E1539", {"start": v(-124.04, -19) * mm, "end": v(-124.02, -19.68) * mm});
            skLineSegment(sketch, "E1540", {"start": v(-124.02, -19.68) * mm, "end": v(-123.99, -20.29) * mm});
            skLineSegment(sketch, "E1541", {"start": v(-123.99, -20.29) * mm, "end": v(-123.95, -20.83) * mm});
            skLineSegment(sketch, "E1542", {"start": v(-123.95, -20.83) * mm, "end": v(-123.9, -21.3) * mm});
            skLineSegment(sketch, "E1543", {"start": v(-123.9, -21.3) * mm, "end": v(-123.82, -21.7) * mm});
            skLineSegment(sketch, "E1544", {"start": v(-123.82, -21.7) * mm, "end": v(-123.74, -22.03) * mm});
            skLineSegment(sketch, "E1545", {"start": v(-123.74, -22.03) * mm, "end": v(-123.65, -22.3) * mm});
            skLineSegment(sketch, "E1546", {"start": v(-123.65, -22.3) * mm, "end": v(-123.43, -22.72) * mm});
            skLineSegment(sketch, "E1547", {"start": v(-123.43, -22.72) * mm, "end": v(-123.14, -23.1) * mm});
            skLineSegment(sketch, "E1548", {"start": v(-123.14, -23.1) * mm, "end": v(-122.8, -23.44) * mm});
            skLineSegment(sketch, "E1549", {"start": v(-122.8, -23.44) * mm, "end": v(-122.38, -23.73) * mm});
            skLineSegment(sketch, "E1550", {"start": v(-122.38, -23.73) * mm, "end": v(-122.15, -23.85) * mm});
            skLineSegment(sketch, "E1551", {"start": v(-122.15, -23.85) * mm, "end": v(-121.9, -23.96) * mm});
            skLineSegment(sketch, "E1552", {"start": v(-121.9, -23.96) * mm, "end": v(-121.62, -24.05) * mm});
            skLineSegment(sketch, "E1553", {"start": v(-121.62, -24.05) * mm, "end": v(-121.32, -24.12) * mm});
            skLineSegment(sketch, "E1554", {"start": v(-121.32, -24.12) * mm, "end": v(-120.99, -24.18) * mm});
            skLineSegment(sketch, "E1555", {"start": v(-120.99, -24.18) * mm, "end": v(-120.64, -24.22) * mm});
            skLineSegment(sketch, "E1556", {"start": v(-120.64, -24.22) * mm, "end": v(-120.27, -24.25) * mm});
            skLineSegment(sketch, "E1557", {"start": v(-120.27, -24.25) * mm, "end": v(-119.87, -24.26) * mm});
            skLineSegment(sketch, "E1558", {"start": v(-119.87, -24.26) * mm, "end": v(-119.55, -24.25) * mm});
            skLineSegment(sketch, "E1559", {"start": v(-119.55, -24.25) * mm, "end": v(-119.2, -24.24) * mm});
            skLineSegment(sketch, "E1560", {"start": v(-119.2, -24.24) * mm, "end": v(-118.84, -24.22) * mm});
            skLineSegment(sketch, "E1561", {"start": v(-118.84, -24.22) * mm, "end": v(-118.45, -24.19) * mm});
            skLineSegment(sketch, "E1562", {"start": v(-118.45, -24.19) * mm, "end": v(-118.03, -24.15) * mm});
            skLineSegment(sketch, "E1563", {"start": v(-118.03, -24.15) * mm, "end": v(-117.59, -24.1) * mm});
            skLineSegment(sketch, "E1564", {"start": v(-117.59, -24.1) * mm, "end": v(-117.12, -24.04) * mm});
            skLineSegment(sketch, "E1565", {"start": v(-144.26, -30.56) * mm, "end": v(-150.85, -30.56) * mm});
            skLineSegment(sketch, "E1566", {"start": v(-150.85, -30.56) * mm, "end": v(-150.85, -24.18) * mm});
            skLineSegment(sketch, "E1567", {"start": v(-150.85, -24.18) * mm, "end": v(-151.5, -25.07) * mm});
            skLineSegment(sketch, "E1568", {"start": v(-151.5, -25.07) * mm, "end": v(-152.18, -25.9) * mm});
            skLineSegment(sketch, "E1569", {"start": v(-152.18, -25.9) * mm, "end": v(-152.88, -26.68) * mm});
            skLineSegment(sketch, "E1570", {"start": v(-152.88, -26.68) * mm, "end": v(-153.62, -27.4) * mm});
            skLineSegment(sketch, "E1571", {"start": v(-153.62, -27.4) * mm, "end": v(-154.38, -28.06) * mm});
            skLineSegment(sketch, "E1572", {"start": v(-154.38, -28.06) * mm, "end": v(-155.17, -28.66) * mm});
            skLineSegment(sketch, "E1573", {"start": v(-155.17, -28.66) * mm, "end": v(-155.99, -29.21) * mm});
            skLineSegment(sketch, "E1574", {"start": v(-155.99, -29.21) * mm, "end": v(-156.84, -29.7) * mm});
            skLineSegment(sketch, "E1575", {"start": v(-156.84, -29.7) * mm, "end": v(-157.71, -30.13) * mm});
            skLineSegment(sketch, "E1576", {"start": v(-157.71, -30.13) * mm, "end": v(-158.62, -30.5) * mm});
            skLineSegment(sketch, "E1577", {"start": v(-158.62, -30.5) * mm, "end": v(-159.55, -30.82) * mm});
            skLineSegment(sketch, "E1578", {"start": v(-159.55, -30.82) * mm, "end": v(-160.51, -31.08) * mm});
            skLineSegment(sketch, "E1579", {"start": v(-160.51, -31.08) * mm, "end": v(-161.5, -31.28) * mm});
            skLineSegment(sketch, "E1580", {"start": v(-161.5, -31.28) * mm, "end": v(-162.52, -31.43) * mm});
            skLineSegment(sketch, "E1581", {"start": v(-162.52, -31.43) * mm, "end": v(-163.57, -31.51) * mm});
            skLineSegment(sketch, "E1582", {"start": v(-163.57, -31.51) * mm, "end": v(-164.64, -31.54) * mm});
            skLineSegment(sketch, "E1583", {"start": v(-164.64, -31.54) * mm, "end": v(-165.6, -31.52) * mm});
            skLineSegment(sketch, "E1584", {"start": v(-165.6, -31.52) * mm, "end": v(-166.53, -31.45) * mm});
            skLineSegment(sketch, "E1585", {"start": v(-166.53, -31.45) * mm, "end": v(-167.46, -31.34) * mm});
            skLineSegment(sketch, "E1586", {"start": v(-167.46, -31.34) * mm, "end": v(-168.36, -31.17) * mm});
            skLineSegment(sketch, "E1587", {"start": v(-168.36, -31.17) * mm, "end": v(-169.25, -30.97) * mm});
            skLineSegment(sketch, "E1588", {"start": v(-169.25, -30.97) * mm, "end": v(-170.13, -30.71) * mm});
            skLineSegment(sketch, "E1589", {"start": v(-170.13, -30.71) * mm, "end": v(-170.98, -30.41) * mm});
            skLineSegment(sketch, "E1590", {"start": v(-170.98, -30.41) * mm, "end": v(-171.83, -30.07) * mm});
            skLineSegment(sketch, "E1591", {"start": v(-171.83, -30.07) * mm, "end": v(-172.63, -29.69) * mm});
            skLineSegment(sketch, "E1592", {"start": v(-172.63, -29.69) * mm, "end": v(-173.39, -29.28) * mm});
            skLineSegment(sketch, "E1593", {"start": v(-173.39, -29.28) * mm, "end": v(-174.09, -28.86) * mm});
            skLineSegment(sketch, "E1594", {"start": v(-174.09, -28.86) * mm, "end": v(-174.73, -28.4) * mm});
            skLineSegment(sketch, "E1595", {"start": v(-174.73, -28.4) * mm, "end": v(-175.32, -27.93) * mm});
            skLineSegment(sketch, "E1596", {"start": v(-175.32, -27.93) * mm, "end": v(-175.86, -27.43) * mm});
            skLineSegment(sketch, "E1597", {"start": v(-175.86, -27.43) * mm, "end": v(-176.35, -26.91) * mm});
            skLineSegment(sketch, "E1598", {"start": v(-176.35, -26.91) * mm, "end": v(-176.78, -26.36) * mm});
            skLineSegment(sketch, "E1599", {"start": v(-176.78, -26.36) * mm, "end": v(-177.17, -25.8) * mm});
            skLineSegment(sketch, "E1600", {"start": v(-177.17, -25.8) * mm, "end": v(-177.53, -25.19) * mm});
            skLineSegment(sketch, "E1601", {"start": v(-177.53, -25.19) * mm, "end": v(-177.86, -24.55) * mm});
            skLineSegment(sketch, "E1602", {"start": v(-177.86, -24.55) * mm, "end": v(-178.15, -23.88) * mm});
            skLineSegment(sketch, "E1603", {"start": v(-178.15, -23.88) * mm, "end": v(-178.42, -23.18) * mm});
            skLineSegment(sketch, "E1604", {"start": v(-178.42, -23.18) * mm, "end": v(-178.66, -22.46) * mm});
            skLineSegment(sketch, "E1605", {"start": v(-178.66, -22.46) * mm, "end": v(-178.87, -21.7) * mm});
            skLineSegment(sketch, "E1606", {"start": v(-178.87, -21.7) * mm, "end": v(-179.05, -20.9) * mm});
            skLineSegment(sketch, "E1607", {"start": v(-179.05, -20.9) * mm, "end": v(-179.15, -20.32) * mm});
            skLineSegment(sketch, "E1608", {"start": v(-179.15, -20.32) * mm, "end": v(-179.25, -19.66) * mm});
            skLineSegment(sketch, "E1609", {"start": v(-179.25, -19.66) * mm, "end": v(-179.32, -18.92) * mm});
            skLineSegment(sketch, "E1610", {"start": v(-179.32, -18.92) * mm, "end": v(-179.39, -18.1) * mm});
            skLineSegment(sketch, "E1611", {"start": v(-179.39, -18.1) * mm, "end": v(-179.44, -17.2) * mm});
            skLineSegment(sketch, "E1612", {"start": v(-179.44, -17.2) * mm, "end": v(-179.47, -16.22) * mm});
            skLineSegment(sketch, "E1613", {"start": v(-179.47, -16.22) * mm, "end": v(-179.5, -15.16) * mm});
            skLineSegment(sketch, "E1614", {"start": v(-179.5, -15.16) * mm, "end": v(-179.5, -14.03) * mm});
            skLineSegment(sketch, "E1615", {"start": v(-179.5, -14.03) * mm, "end": v(-179.5, 12.9) * mm});
            skLineSegment(sketch, "E1616", {"start": v(-179.5, 12.9) * mm, "end": v(-172.13, 12.9) * mm});
            skLineSegment(sketch, "E1617", {"start": v(-172.13, 12.9) * mm, "end": v(-172.13, -11.2) * mm});
            skLineSegment(sketch, "E1618", {"start": v(-172.13, -11.2) * mm, "end": v(-172.13, -11.9) * mm});
            skLineSegment(sketch, "E1619", {"start": v(-172.13, -11.9) * mm, "end": v(-172.13, -12.59) * mm});
            skLineSegment(sketch, "E1620", {"start": v(-172.13, -12.59) * mm, "end": v(-172.12, -13.23) * mm});
            skLineSegment(sketch, "E1621", {"start": v(-172.12, -13.23) * mm, "end": v(-172.1, -13.85) * mm});
            skLineSegment(sketch, "E1622", {"start": v(-172.1, -13.85) * mm, "end": v(-172.09, -14.44) * mm});
            skLineSegment(sketch, "E1623", {"start": v(-172.09, -14.44) * mm, "end": v(-172.07, -15) * mm});
            skLineSegment(sketch, "E1624", {"start": v(-172.07, -15) * mm, "end": v(-172.05, -15.53) * mm});
            skLineSegment(sketch, "E1625", {"start": v(-172.05, -15.53) * mm, "end": v(-172.02, -16.03) * mm});
            skLineSegment(sketch, "E1626", {"start": v(-172.02, -16.03) * mm, "end": v(-172, -16.5) * mm});
            skLineSegment(sketch, "E1627", {"start": v(-172, -16.5) * mm, "end": v(-171.96, -16.94) * mm});
            skLineSegment(sketch, "E1628", {"start": v(-171.96, -16.94) * mm, "end": v(-171.92, -17.36) * mm});
            skLineSegment(sketch, "E1629", {"start": v(-171.92, -17.36) * mm, "end": v(-171.88, -17.74) * mm});
            skLineSegment(sketch, "E1630", {"start": v(-171.88, -17.74) * mm, "end": v(-171.84, -18.1) * mm});
            skLineSegment(sketch, "E1631", {"start": v(-171.84, -18.1) * mm, "end": v(-171.79, -18.42) * mm});
            skLineSegment(sketch, "E1632", {"start": v(-171.79, -18.42) * mm, "end": v(-171.74, -18.71) * mm});
            skLineSegment(sketch, "E1633", {"start": v(-171.74, -18.71) * mm, "end": v(-171.68, -18.98) * mm});
            skLineSegment(sketch, "E1634", {"start": v(-171.68, -18.98) * mm, "end": v(-171.48, -19.68) * mm});
            skLineSegment(sketch, "E1635", {"start": v(-171.48, -19.68) * mm, "end": v(-171.24, -20.35) * mm});
            skLineSegment(sketch, "E1636", {"start": v(-171.24, -20.35) * mm, "end": v(-170.94, -20.98) * mm});
            skLineSegment(sketch, "E1637", {"start": v(-170.94, -20.98) * mm, "end": v(-170.6, -21.57) * mm});
            skLineSegment(sketch, "E1638", {"start": v(-170.6, -21.57) * mm, "end": v(-170.2, -22.12) * mm});
            skLineSegment(sketch, "E1639", {"start": v(-170.2, -22.12) * mm, "end": v(-169.76, -22.63) * mm});
            skLineSegment(sketch, "E1640", {"start": v(-169.76, -22.63) * mm, "end": v(-169.27, -23.1) * mm});
            skLineSegment(sketch, "E1641", {"start": v(-169.27, -23.1) * mm, "end": v(-168.74, -23.54) * mm});
            skLineSegment(sketch, "E1642", {"start": v(-168.74, -23.54) * mm, "end": v(-168.16, -23.93) * mm});
            skLineSegment(sketch, "E1643", {"start": v(-168.16, -23.93) * mm, "end": v(-167.54, -24.27) * mm});
            skLineSegment(sketch, "E1644", {"start": v(-167.54, -24.27) * mm, "end": v(-166.9, -24.55) * mm});
            skLineSegment(sketch, "E1645", {"start": v(-166.9, -24.55) * mm, "end": v(-166.22, -24.78) * mm});
            skLineSegment(sketch, "E1646", {"start": v(-166.22, -24.78) * mm, "end": v(-165.5, -24.97) * mm});
            skLineSegment(sketch, "E1647", {"start": v(-165.5, -24.97) * mm, "end": v(-164.76, -25.1) * mm});
            skLineSegment(sketch, "E1648", {"start": v(-164.76, -25.1) * mm, "end": v(-163.98, -25.17) * mm});
            skLineSegment(sketch, "E1649", {"start": v(-163.98, -25.17) * mm, "end": v(-163.17, -25.2) * mm});
            skLineSegment(sketch, "E1650", {"start": v(-163.17, -25.2) * mm, "end": v(-162.35, -25.17) * mm});
            skLineSegment(sketch, "E1651", {"start": v(-162.35, -25.17) * mm, "end": v(-161.54, -25.1) * mm});
            skLineSegment(sketch, "E1652", {"start": v(-161.54, -25.1) * mm, "end": v(-160.74, -24.96) * mm});
            skLineSegment(sketch, "E1653", {"start": v(-160.74, -24.96) * mm, "end": v(-159.96, -24.77) * mm});
            skLineSegment(sketch, "E1654", {"start": v(-159.96, -24.77) * mm, "end": v(-159.19, -24.53) * mm});
            skLineSegment(sketch, "E1655", {"start": v(-159.19, -24.53) * mm, "end": v(-158.43, -24.24) * mm});
            skLineSegment(sketch, "E1656", {"start": v(-158.43, -24.24) * mm, "end": v(-157.68, -23.9) * mm});
            skLineSegment(sketch, "E1657", {"start": v(-157.68, -23.9) * mm, "end": v(-156.95, -23.5) * mm});
            skLineSegment(sketch, "E1658", {"start": v(-156.95, -23.5) * mm, "end": v(-156.25, -23.06) * mm});
            skLineSegment(sketch, "E1659", {"start": v(-156.25, -23.06) * mm, "end": v(-155.6, -22.57) * mm});
            skLineSegment(sketch, "E1660", {"start": v(-155.6, -22.57) * mm, "end": v(-155, -22.05) * mm});
            skLineSegment(sketch, "E1661", {"start": v(-155, -22.05) * mm, "end": v(-154.47, -21.5) * mm});
            skLineSegment(sketch, "E1662", {"start": v(-154.47, -21.5) * mm, "end": v(-153.98, -20.9) * mm});
            skLineSegment(sketch, "E1663", {"start": v(-153.98, -20.9) * mm, "end": v(-153.54, -20.26) * mm});
            skLineSegment(sketch, "E1664", {"start": v(-153.54, -20.26) * mm, "end": v(-153.16, -19.59) * mm});
            skLineSegment(sketch, "E1665", {"start": v(-153.16, -19.59) * mm, "end": v(-152.84, -18.88) * mm});
            skLineSegment(sketch, "E1666", {"start": v(-152.84, -18.88) * mm, "end": v(-152.55, -18.1) * mm});
            skLineSegment(sketch, "E1667", {"start": v(-152.55, -18.1) * mm, "end": v(-152.3, -17.25) * mm});
            skLineSegment(sketch, "E1668", {"start": v(-152.3, -17.25) * mm, "end": v(-152.1, -16.3) * mm});
            skLineSegment(sketch, "E1669", {"start": v(-152.1, -16.3) * mm, "end": v(-151.93, -15.29) * mm});
            skLineSegment(sketch, "E1670", {"start": v(-151.93, -15.29) * mm, "end": v(-151.8, -14.19) * mm});
            skLineSegment(sketch, "E1671", {"start": v(-151.8, -14.19) * mm, "end": v(-151.7, -13) * mm});
            skLineSegment(sketch, "E1672", {"start": v(-151.7, -13) * mm, "end": v(-151.65, -11.73) * mm});
            skLineSegment(sketch, "E1673", {"start": v(-151.65, -11.73) * mm, "end": v(-151.63, -10.38) * mm});
            skLineSegment(sketch, "E1674", {"start": v(-151.63, -10.38) * mm, "end": v(-151.63, 12.9) * mm});
            skLineSegment(sketch, "E1675", {"start": v(-151.63, 12.9) * mm, "end": v(-144.26, 12.9) * mm});
            skLineSegment(sketch, "E1676", {"start": v(-144.26, 12.9) * mm, "end": v(-144.26, -30.56) * mm});
            skLineSegment(sketch, "E1677", {"start": v(-206.39, -30.56) * mm, "end": v(-214.33, -30.56) * mm});
            skLineSegment(sketch, "E1678", {"start": v(-214.33, -30.56) * mm, "end": v(-214.33, 22.36) * mm});
            skLineSegment(sketch, "E1679", {"start": v(-214.33, 22.36) * mm, "end": v(-234.1, 22.36) * mm});
            skLineSegment(sketch, "E1680", {"start": v(-234.1, 22.36) * mm, "end": v(-234.1, 29.44) * mm});
            skLineSegment(sketch, "E1681", {"start": v(-234.1, 29.44) * mm, "end": v(-186.54, 29.44) * mm});
            skLineSegment(sketch, "E1682", {"start": v(-186.54, 29.44) * mm, "end": v(-186.54, 22.36) * mm});
            skLineSegment(sketch, "E1683", {"start": v(-186.54, 22.36) * mm, "end": v(-206.39, 22.36) * mm});
            skLineSegment(sketch, "E1684", {"start": v(-206.39, 22.36) * mm, "end": v(-206.39, -30.56) * mm});
            skSolve(sketch);
        }
        {
            var Q0;
            Q0=makeQuery(id+"F0.imprint","IMPRINT",FACE,{"disambiguationData":[TD([[makeQuery(id+"F0.imprint","IMPRINT",EDGE,{"derivedFrom":sQuery(id+"F0.wireOp",EDGE,"E0")}),-1.0]])]});
            extrude(context, id + "F1", {"entities" : qUnion([Q0]), "depth" : 3 * mm});
        }
    });
